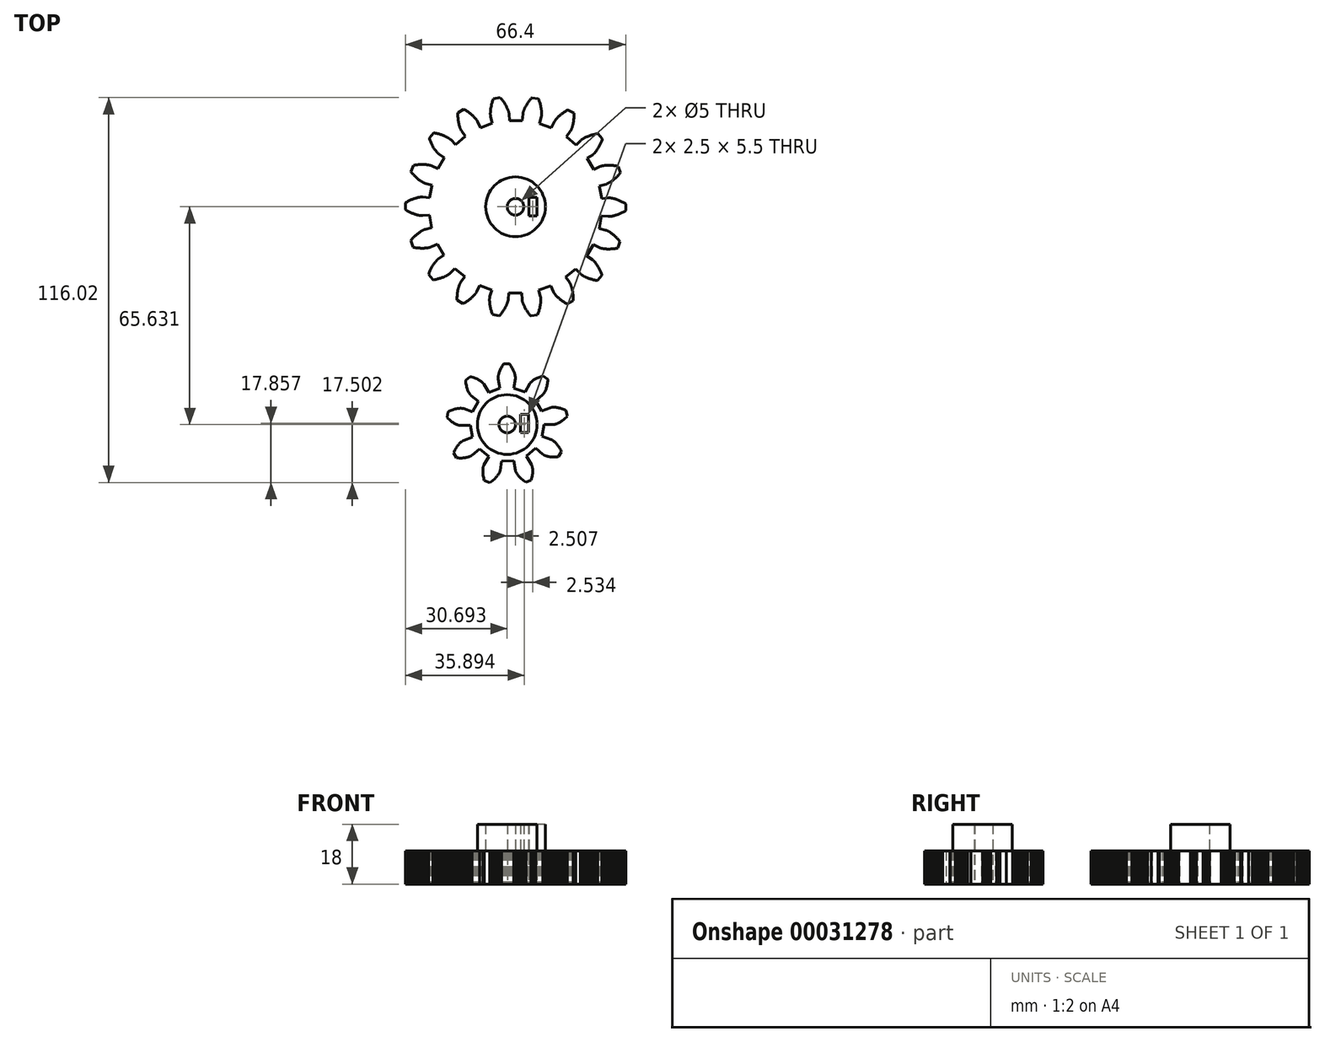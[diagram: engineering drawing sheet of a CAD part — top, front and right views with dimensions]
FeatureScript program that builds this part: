
annotation { "Feature Type Name" : "Feature", "Feature Type Description" : "" }
export const myFeature = defineFeature(function(context is Context, id is Id, definition is map)
    precondition{}
    {
        {
            var Q0;
            Q0=qCreatedBy(makeId("Top.planeOp"),FACE);
            var sketch = newSketch(context, id + "F0", { "sketchPlane" : qUnion([Q0])});
            skLineSegment(sketch, "E0", {"start": v(8.62, -40.5) * mm, "end": v(11.54, -40.5) * mm});
            skLineSegment(sketch, "E1", {"start": v(11.54, -40.5) * mm, "end": v(11.56, -40.5) * mm});
            skLineSegment(sketch, "E2", {"start": v(11.56, -40.5) * mm, "end": v(11.6, -40.5) * mm});
            skLineSegment(sketch, "E3", {"start": v(11.6, -40.5) * mm, "end": v(11.66, -40.5) * mm});
            skLineSegment(sketch, "E4", {"start": v(11.66, -40.5) * mm, "end": v(11.74, -40.48) * mm});
            skLineSegment(sketch, "E5", {"start": v(11.74, -40.48) * mm, "end": v(11.85, -40.46) * mm});
            skLineSegment(sketch, "E6", {"start": v(11.85, -40.46) * mm, "end": v(11.97, -40.43) * mm});
            skLineSegment(sketch, "E7", {"start": v(11.97, -40.43) * mm, "end": v(12.1, -40.4) * mm});
            skLineSegment(sketch, "E8", {"start": v(12.1, -40.4) * mm, "end": v(12.27, -40.34) * mm});
            skLineSegment(sketch, "E9", {"start": v(12.27, -40.34) * mm, "end": v(12.45, -40.28) * mm});
            skLineSegment(sketch, "E10", {"start": v(12.45, -40.28) * mm, "end": v(12.64, -40.2) * mm});
            skLineSegment(sketch, "E11", {"start": v(12.64, -40.2) * mm, "end": v(12.85, -40.1) * mm});
            skLineSegment(sketch, "E12", {"start": v(12.85, -40.1) * mm, "end": v(13.08, -40) * mm});
            skLineSegment(sketch, "E13", {"start": v(13.08, -40) * mm, "end": v(13.32, -39.86) * mm});
            skLineSegment(sketch, "E14", {"start": v(13.32, -39.86) * mm, "end": v(13.57, -39.7) * mm});
            skLineSegment(sketch, "E15", {"start": v(13.57, -39.7) * mm, "end": v(13.83, -39.54) * mm});
            skLineSegment(sketch, "E16", {"start": v(13.83, -39.54) * mm, "end": v(14.1, -39.34) * mm});
            skLineSegment(sketch, "E17", {"start": v(14.1, -39.34) * mm, "end": v(14.4, -39.12) * mm});
            skLineSegment(sketch, "E18", {"start": v(14.4, -39.12) * mm, "end": v(14.68, -38.88) * mm});
            skLineSegment(sketch, "E19", {"start": v(14.68, -38.88) * mm, "end": v(14.98, -38.61) * mm});
            skLineSegment(sketch, "E20", {"start": v(14.98, -38.61) * mm, "end": v(15.28, -38.32) * mm});
            skLineSegment(sketch, "E21", {"start": v(15.28, -38.32) * mm, "end": v(15.58, -38) * mm});
            skLineSegment(sketch, "E22", {"start": v(15.58, -38) * mm, "end": v(15.26, -36.29) * mm});
            skLineSegment(sketch, "E23", {"start": v(15.26, -36.29) * mm, "end": v(14.87, -36.1) * mm});
            skLineSegment(sketch, "E24", {"start": v(14.87, -36.1) * mm, "end": v(14.48, -35.93) * mm});
            skLineSegment(sketch, "E25", {"start": v(14.48, -35.93) * mm, "end": v(14.1, -35.8) * mm});
            skLineSegment(sketch, "E26", {"start": v(14.1, -35.8) * mm, "end": v(13.74, -35.67) * mm});
            skLineSegment(sketch, "E27", {"start": v(13.74, -35.67) * mm, "end": v(13.4, -35.57) * mm});
            skLineSegment(sketch, "E28", {"start": v(13.4, -35.57) * mm, "end": v(13.07, -35.49) * mm});
            skLineSegment(sketch, "E29", {"start": v(13.07, -35.49) * mm, "end": v(12.77, -35.42) * mm});
            skLineSegment(sketch, "E30", {"start": v(12.77, -35.42) * mm, "end": v(12.48, -35.37) * mm});
            skLineSegment(sketch, "E31", {"start": v(12.48, -35.37) * mm, "end": v(12.2, -35.34) * mm});
            skLineSegment(sketch, "E32", {"start": v(12.2, -35.34) * mm, "end": v(11.95, -35.31) * mm});
            skLineSegment(sketch, "E33", {"start": v(11.95, -35.31) * mm, "end": v(11.72, -35.3) * mm});
            skLineSegment(sketch, "E34", {"start": v(11.72, -35.3) * mm, "end": v(11.51, -35.3) * mm});
            skLineSegment(sketch, "E35", {"start": v(11.51, -35.3) * mm, "end": v(11.32, -35.3) * mm});
            skLineSegment(sketch, "E36", {"start": v(11.32, -35.3) * mm, "end": v(11.15, -35.31) * mm});
            skLineSegment(sketch, "E37", {"start": v(11.15, -35.31) * mm, "end": v(11, -35.33) * mm});
            skLineSegment(sketch, "E38", {"start": v(11, -35.33) * mm, "end": v(10.88, -35.34) * mm});
            skLineSegment(sketch, "E39", {"start": v(10.88, -35.34) * mm, "end": v(10.78, -35.36) * mm});
            skLineSegment(sketch, "E40", {"start": v(10.78, -35.36) * mm, "end": v(10.7, -35.38) * mm});
            skLineSegment(sketch, "E41", {"start": v(10.7, -35.38) * mm, "end": v(10.64, -35.4) * mm});
            skLineSegment(sketch, "E42", {"start": v(10.64, -35.4) * mm, "end": v(10.6, -35.4) * mm});
            skLineSegment(sketch, "E43", {"start": v(10.6, -35.4) * mm, "end": v(10.58, -35.41) * mm});
            skLineSegment(sketch, "E44", {"start": v(10.58, -35.41) * mm, "end": v(7.86, -36.47) * mm});
            skLineSegment(sketch, "E45", {"start": v(7.86, -36.47) * mm, "end": v(6.01, -33.36) * mm});
            skLineSegment(sketch, "E46", {"start": v(6.01, -33.36) * mm, "end": v(8.25, -31.48) * mm});
            skLineSegment(sketch, "E47", {"start": v(8.25, -31.48) * mm, "end": v(8.27, -31.47) * mm});
            skLineSegment(sketch, "E48", {"start": v(8.27, -31.47) * mm, "end": v(8.3, -31.44) * mm});
            skLineSegment(sketch, "E49", {"start": v(8.3, -31.44) * mm, "end": v(8.34, -31.4) * mm});
            skLineSegment(sketch, "E50", {"start": v(8.34, -31.4) * mm, "end": v(8.4, -31.33) * mm});
            skLineSegment(sketch, "E51", {"start": v(8.4, -31.33) * mm, "end": v(8.46, -31.25) * mm});
            skLineSegment(sketch, "E52", {"start": v(8.46, -31.25) * mm, "end": v(8.53, -31.15) * mm});
            skLineSegment(sketch, "E53", {"start": v(8.53, -31.15) * mm, "end": v(8.62, -31.03) * mm});
            skLineSegment(sketch, "E54", {"start": v(8.62, -31.03) * mm, "end": v(8.7, -30.88) * mm});
            skLineSegment(sketch, "E55", {"start": v(8.7, -30.88) * mm, "end": v(8.8, -30.72) * mm});
            skLineSegment(sketch, "E56", {"start": v(8.8, -30.72) * mm, "end": v(8.9, -30.54) * mm});
            skLineSegment(sketch, "E57", {"start": v(8.9, -30.54) * mm, "end": v(9, -30.33) * mm});
            skLineSegment(sketch, "E58", {"start": v(9, -30.33) * mm, "end": v(9.1, -30.1) * mm});
            skLineSegment(sketch, "E59", {"start": v(9.1, -30.1) * mm, "end": v(9.2, -29.84) * mm});
            skLineSegment(sketch, "E60", {"start": v(9.2, -29.84) * mm, "end": v(9.3, -29.56) * mm});
            skLineSegment(sketch, "E61", {"start": v(9.3, -29.56) * mm, "end": v(9.39, -29.26) * mm});
            skLineSegment(sketch, "E62", {"start": v(9.39, -29.26) * mm, "end": v(9.47, -28.93) * mm});
            skLineSegment(sketch, "E63", {"start": v(9.47, -28.93) * mm, "end": v(9.55, -28.58) * mm});
            skLineSegment(sketch, "E64", {"start": v(9.55, -28.58) * mm, "end": v(9.61, -28.21) * mm});
            skLineSegment(sketch, "E65", {"start": v(9.61, -28.21) * mm, "end": v(9.67, -27.81) * mm});
            skLineSegment(sketch, "E66", {"start": v(9.67, -27.81) * mm, "end": v(9.71, -27.4) * mm});
            skLineSegment(sketch, "E67", {"start": v(9.71, -27.4) * mm, "end": v(9.74, -26.95) * mm});
            skLineSegment(sketch, "E68", {"start": v(9.74, -26.95) * mm, "end": v(8.4, -25.85) * mm});
            skLineSegment(sketch, "E69", {"start": v(8.4, -25.85) * mm, "end": v(7.97, -25.96) * mm});
            skLineSegment(sketch, "E70", {"start": v(7.97, -25.96) * mm, "end": v(7.56, -26.09) * mm});
            skLineSegment(sketch, "E71", {"start": v(7.56, -26.09) * mm, "end": v(7.19, -26.22) * mm});
            skLineSegment(sketch, "E72", {"start": v(7.19, -26.22) * mm, "end": v(6.83, -26.36) * mm});
            skLineSegment(sketch, "E73", {"start": v(6.83, -26.36) * mm, "end": v(6.5, -26.5) * mm});
            skLineSegment(sketch, "E74", {"start": v(6.5, -26.5) * mm, "end": v(6.2, -26.65) * mm});
            skLineSegment(sketch, "E75", {"start": v(6.2, -26.65) * mm, "end": v(5.92, -26.8) * mm});
            skLineSegment(sketch, "E76", {"start": v(5.92, -26.8) * mm, "end": v(5.67, -26.94) * mm});
            skLineSegment(sketch, "E77", {"start": v(5.67, -26.94) * mm, "end": v(5.44, -27.09) * mm});
            skLineSegment(sketch, "E78", {"start": v(5.44, -27.09) * mm, "end": v(5.23, -27.23) * mm});
            skLineSegment(sketch, "E79", {"start": v(5.23, -27.23) * mm, "end": v(5.04, -27.37) * mm});
            skLineSegment(sketch, "E80", {"start": v(5.04, -27.37) * mm, "end": v(4.88, -27.5) * mm});
            skLineSegment(sketch, "E81", {"start": v(4.88, -27.5) * mm, "end": v(4.74, -27.63) * mm});
            skLineSegment(sketch, "E82", {"start": v(4.74, -27.63) * mm, "end": v(4.62, -27.75) * mm});
            skLineSegment(sketch, "E83", {"start": v(4.62, -27.75) * mm, "end": v(4.52, -27.85) * mm});
            skLineSegment(sketch, "E84", {"start": v(4.52, -27.85) * mm, "end": v(4.43, -27.94) * mm});
            skLineSegment(sketch, "E85", {"start": v(4.43, -27.94) * mm, "end": v(4.37, -28.02) * mm});
            skLineSegment(sketch, "E86", {"start": v(4.37, -28.02) * mm, "end": v(4.31, -28.1) * mm});
            skLineSegment(sketch, "E87", {"start": v(4.31, -28.1) * mm, "end": v(4.28, -28.14) * mm});
            skLineSegment(sketch, "E88", {"start": v(4.28, -28.14) * mm, "end": v(4.26, -28.18) * mm});
            skLineSegment(sketch, "E89", {"start": v(4.26, -28.18) * mm, "end": v(4.25, -28.2) * mm});
            skLineSegment(sketch, "E90", {"start": v(4.25, -28.2) * mm, "end": v(2.84, -30.75) * mm});
            skLineSegment(sketch, "E91", {"start": v(2.84, -30.75) * mm, "end": v(-0.58, -29.55) * mm});
            skLineSegment(sketch, "E92", {"start": v(-0.58, -29.55) * mm, "end": v(-0.07, -26.68) * mm});
            skLineSegment(sketch, "E93", {"start": v(-0.07, -26.68) * mm, "end": v(-0.07, -26.66) * mm});
            skLineSegment(sketch, "E94", {"start": v(-0.07, -26.66) * mm, "end": v(-0.06, -26.62) * mm});
            skLineSegment(sketch, "E95", {"start": v(-0.06, -26.62) * mm, "end": v(-0.06, -26.55) * mm});
            skLineSegment(sketch, "E96", {"start": v(-0.06, -26.55) * mm, "end": v(-0.06, -26.47) * mm});
            skLineSegment(sketch, "E97", {"start": v(-0.06, -26.47) * mm, "end": v(-0.06, -26.37) * mm});
            skLineSegment(sketch, "E98", {"start": v(-0.06, -26.37) * mm, "end": v(-0.07, -26.24) * mm});
            skLineSegment(sketch, "E99", {"start": v(-0.07, -26.24) * mm, "end": v(-0.08, -26.1) * mm});
            skLineSegment(sketch, "E100", {"start": v(-0.08, -26.1) * mm, "end": v(-0.1, -25.93) * mm});
            skLineSegment(sketch, "E101", {"start": v(-0.1, -25.93) * mm, "end": v(-0.13, -25.74) * mm});
            skLineSegment(sketch, "E102", {"start": v(-0.13, -25.74) * mm, "end": v(-0.18, -25.54) * mm});
            skLineSegment(sketch, "E103", {"start": v(-0.18, -25.54) * mm, "end": v(-0.24, -25.31) * mm});
            skLineSegment(sketch, "E104", {"start": v(-0.24, -25.31) * mm, "end": v(-0.3, -25.07) * mm});
            skLineSegment(sketch, "E105", {"start": v(-0.3, -25.07) * mm, "end": v(-0.4, -24.81) * mm});
            skLineSegment(sketch, "E106", {"start": v(-0.4, -24.81) * mm, "end": v(-0.5, -24.54) * mm});
            skLineSegment(sketch, "E107", {"start": v(-0.5, -24.54) * mm, "end": v(-0.63, -24.25) * mm});
            skLineSegment(sketch, "E108", {"start": v(-0.63, -24.25) * mm, "end": v(-0.77, -23.94) * mm});
            skLineSegment(sketch, "E109", {"start": v(-0.77, -23.94) * mm, "end": v(-0.94, -23.62) * mm});
            skLineSegment(sketch, "E110", {"start": v(-0.94, -23.62) * mm, "end": v(-1.13, -23.3) * mm});
            skLineSegment(sketch, "E111", {"start": v(-1.13, -23.3) * mm, "end": v(-1.34, -22.96) * mm});
            skLineSegment(sketch, "E112", {"start": v(-1.34, -22.96) * mm, "end": v(-1.58, -22.6) * mm});
            skLineSegment(sketch, "E113", {"start": v(-1.58, -22.6) * mm, "end": v(-1.84, -22.26) * mm});
            skLineSegment(sketch, "E114", {"start": v(-1.84, -22.26) * mm, "end": v(-3.58, -22.27) * mm});
            skLineSegment(sketch, "E115", {"start": v(-3.58, -22.27) * mm, "end": v(-3.83, -22.63) * mm});
            skLineSegment(sketch, "E116", {"start": v(-3.83, -22.63) * mm, "end": v(-4.06, -22.99) * mm});
            skLineSegment(sketch, "E117", {"start": v(-4.06, -22.99) * mm, "end": v(-4.27, -23.33) * mm});
            skLineSegment(sketch, "E118", {"start": v(-4.27, -23.33) * mm, "end": v(-4.45, -23.66) * mm});
            skLineSegment(sketch, "E119", {"start": v(-4.45, -23.66) * mm, "end": v(-4.6, -23.98) * mm});
            skLineSegment(sketch, "E120", {"start": v(-4.6, -23.98) * mm, "end": v(-4.75, -24.3) * mm});
            skLineSegment(sketch, "E121", {"start": v(-4.75, -24.3) * mm, "end": v(-4.86, -24.58) * mm});
            skLineSegment(sketch, "E122", {"start": v(-4.86, -24.58) * mm, "end": v(-4.96, -24.86) * mm});
            skLineSegment(sketch, "E123", {"start": v(-4.96, -24.86) * mm, "end": v(-5.05, -25.12) * mm});
            skLineSegment(sketch, "E124", {"start": v(-5.05, -25.12) * mm, "end": v(-5.11, -25.37) * mm});
            skLineSegment(sketch, "E125", {"start": v(-5.11, -25.37) * mm, "end": v(-5.17, -25.6) * mm});
            skLineSegment(sketch, "E126", {"start": v(-5.17, -25.6) * mm, "end": v(-5.2, -25.8) * mm});
            skLineSegment(sketch, "E127", {"start": v(-5.2, -25.8) * mm, "end": v(-5.23, -25.98) * mm});
            skLineSegment(sketch, "E128", {"start": v(-5.23, -25.98) * mm, "end": v(-5.25, -26.15) * mm});
            skLineSegment(sketch, "E129", {"start": v(-5.25, -26.15) * mm, "end": v(-5.26, -26.3) * mm});
            skLineSegment(sketch, "E130", {"start": v(-5.26, -26.3) * mm, "end": v(-5.27, -26.42) * mm});
            skLineSegment(sketch, "E131", {"start": v(-5.27, -26.42) * mm, "end": v(-5.27, -26.53) * mm});
            skLineSegment(sketch, "E132", {"start": v(-5.27, -26.53) * mm, "end": v(-5.26, -26.61) * mm});
            skLineSegment(sketch, "E133", {"start": v(-5.26, -26.61) * mm, "end": v(-5.26, -26.67) * mm});
            skLineSegment(sketch, "E134", {"start": v(-5.26, -26.67) * mm, "end": v(-5.25, -26.71) * mm});
            skLineSegment(sketch, "E135", {"start": v(-5.25, -26.71) * mm, "end": v(-5.25, -26.73) * mm});
            skLineSegment(sketch, "E136", {"start": v(-5.25, -26.73) * mm, "end": v(-4.68, -29.6) * mm});
            skLineSegment(sketch, "E137", {"start": v(-4.68, -29.6) * mm, "end": v(-8.07, -30.87) * mm});
            skLineSegment(sketch, "E138", {"start": v(-8.07, -30.87) * mm, "end": v(-9.53, -28.34) * mm});
            skLineSegment(sketch, "E139", {"start": v(-9.53, -28.34) * mm, "end": v(-9.54, -28.33) * mm});
            skLineSegment(sketch, "E140", {"start": v(-9.54, -28.33) * mm, "end": v(-9.56, -28.3) * mm});
            skLineSegment(sketch, "E141", {"start": v(-9.56, -28.3) * mm, "end": v(-9.6, -28.24) * mm});
            skLineSegment(sketch, "E142", {"start": v(-9.6, -28.24) * mm, "end": v(-9.65, -28.18) * mm});
            skLineSegment(sketch, "E143", {"start": v(-9.65, -28.18) * mm, "end": v(-9.72, -28.1) * mm});
            skLineSegment(sketch, "E144", {"start": v(-9.72, -28.1) * mm, "end": v(-9.8, -28) * mm});
            skLineSegment(sketch, "E145", {"start": v(-9.8, -28) * mm, "end": v(-9.91, -27.9) * mm});
            skLineSegment(sketch, "E146", {"start": v(-9.91, -27.9) * mm, "end": v(-10.04, -27.8) * mm});
            skLineSegment(sketch, "E147", {"start": v(-10.04, -27.8) * mm, "end": v(-10.18, -27.67) * mm});
            skLineSegment(sketch, "E148", {"start": v(-10.18, -27.67) * mm, "end": v(-10.35, -27.54) * mm});
            skLineSegment(sketch, "E149", {"start": v(-10.35, -27.54) * mm, "end": v(-10.54, -27.4) * mm});
            skLineSegment(sketch, "E150", {"start": v(-10.54, -27.4) * mm, "end": v(-10.75, -27.27) * mm});
            skLineSegment(sketch, "E151", {"start": v(-10.75, -27.27) * mm, "end": v(-10.98, -27.13) * mm});
            skLineSegment(sketch, "E152", {"start": v(-10.98, -27.13) * mm, "end": v(-11.24, -26.98) * mm});
            skLineSegment(sketch, "E153", {"start": v(-11.24, -26.98) * mm, "end": v(-11.52, -26.84) * mm});
            skLineSegment(sketch, "E154", {"start": v(-11.52, -26.84) * mm, "end": v(-11.83, -26.7) * mm});
            skLineSegment(sketch, "E155", {"start": v(-11.83, -26.7) * mm, "end": v(-12.16, -26.57) * mm});
            skLineSegment(sketch, "E156", {"start": v(-12.16, -26.57) * mm, "end": v(-12.51, -26.43) * mm});
            skLineSegment(sketch, "E157", {"start": v(-12.51, -26.43) * mm, "end": v(-12.9, -26.31) * mm});
            skLineSegment(sketch, "E158", {"start": v(-12.9, -26.31) * mm, "end": v(-13.3, -26.2) * mm});
            skLineSegment(sketch, "E159", {"start": v(-13.3, -26.2) * mm, "end": v(-13.73, -26.1) * mm});
            skLineSegment(sketch, "E160", {"start": v(-13.73, -26.1) * mm, "end": v(-15.05, -27.23) * mm});
            skLineSegment(sketch, "E161", {"start": v(-15.05, -27.23) * mm, "end": v(-15.01, -27.67) * mm});
            skLineSegment(sketch, "E162", {"start": v(-15.01, -27.67) * mm, "end": v(-14.96, -28.09) * mm});
            skLineSegment(sketch, "E163", {"start": v(-14.96, -28.09) * mm, "end": v(-14.9, -28.48) * mm});
            skLineSegment(sketch, "E164", {"start": v(-14.9, -28.48) * mm, "end": v(-14.82, -28.85) * mm});
            skLineSegment(sketch, "E165", {"start": v(-14.82, -28.85) * mm, "end": v(-14.74, -29.2) * mm});
            skLineSegment(sketch, "E166", {"start": v(-14.74, -29.2) * mm, "end": v(-14.65, -29.52) * mm});
            skLineSegment(sketch, "E167", {"start": v(-14.65, -29.52) * mm, "end": v(-14.55, -29.82) * mm});
            skLineSegment(sketch, "E168", {"start": v(-14.55, -29.82) * mm, "end": v(-14.45, -30.1) * mm});
            skLineSegment(sketch, "E169", {"start": v(-14.45, -30.1) * mm, "end": v(-14.34, -30.35) * mm});
            skLineSegment(sketch, "E170", {"start": v(-14.34, -30.35) * mm, "end": v(-14.24, -30.58) * mm});
            skLineSegment(sketch, "E171", {"start": v(-14.24, -30.58) * mm, "end": v(-14.13, -30.79) * mm});
            skLineSegment(sketch, "E172", {"start": v(-14.13, -30.79) * mm, "end": v(-14.03, -30.97) * mm});
            skLineSegment(sketch, "E173", {"start": v(-14.03, -30.97) * mm, "end": v(-13.93, -31.13) * mm});
            skLineSegment(sketch, "E174", {"start": v(-13.93, -31.13) * mm, "end": v(-13.84, -31.27) * mm});
            skLineSegment(sketch, "E175", {"start": v(-13.84, -31.27) * mm, "end": v(-13.75, -31.4) * mm});
            skLineSegment(sketch, "E176", {"start": v(-13.75, -31.4) * mm, "end": v(-13.68, -31.5) * mm});
            skLineSegment(sketch, "E177", {"start": v(-13.68, -31.5) * mm, "end": v(-13.6, -31.57) * mm});
            skLineSegment(sketch, "E178", {"start": v(-13.6, -31.57) * mm, "end": v(-13.55, -31.63) * mm});
            skLineSegment(sketch, "E179", {"start": v(-13.55, -31.63) * mm, "end": v(-13.5, -31.68) * mm});
            skLineSegment(sketch, "E180", {"start": v(-13.5, -31.68) * mm, "end": v(-13.48, -31.7) * mm});
            skLineSegment(sketch, "E181", {"start": v(-13.48, -31.7) * mm, "end": v(-13.46, -31.72) * mm});
            skLineSegment(sketch, "E182", {"start": v(-13.46, -31.72) * mm, "end": v(-11.18, -33.55) * mm});
            skLineSegment(sketch, "E183", {"start": v(-11.18, -33.55) * mm, "end": v(-12.96, -36.7) * mm});
            skLineSegment(sketch, "E184", {"start": v(-12.96, -36.7) * mm, "end": v(-15.7, -35.7) * mm});
            skLineSegment(sketch, "E185", {"start": v(-15.7, -35.7) * mm, "end": v(-15.72, -35.7) * mm});
            skLineSegment(sketch, "E186", {"start": v(-15.72, -35.7) * mm, "end": v(-15.76, -35.69) * mm});
            skLineSegment(sketch, "E187", {"start": v(-15.76, -35.69) * mm, "end": v(-15.82, -35.67) * mm});
            skLineSegment(sketch, "E188", {"start": v(-15.82, -35.67) * mm, "end": v(-15.9, -35.66) * mm});
            skLineSegment(sketch, "E189", {"start": v(-15.9, -35.66) * mm, "end": v(-16, -35.64) * mm});
            skLineSegment(sketch, "E190", {"start": v(-16, -35.64) * mm, "end": v(-16.13, -35.63) * mm});
            skLineSegment(sketch, "E191", {"start": v(-16.13, -35.63) * mm, "end": v(-16.28, -35.61) * mm});
            skLineSegment(sketch, "E192", {"start": v(-16.28, -35.61) * mm, "end": v(-16.45, -35.6) * mm});
            skLineSegment(sketch, "E193", {"start": v(-16.45, -35.6) * mm, "end": v(-16.64, -35.6) * mm});
            skLineSegment(sketch, "E194", {"start": v(-16.64, -35.6) * mm, "end": v(-16.85, -35.61) * mm});
            skLineSegment(sketch, "E195", {"start": v(-16.85, -35.61) * mm, "end": v(-17.08, -35.63) * mm});
            skLineSegment(sketch, "E196", {"start": v(-17.08, -35.63) * mm, "end": v(-17.33, -35.66) * mm});
            skLineSegment(sketch, "E197", {"start": v(-17.33, -35.66) * mm, "end": v(-17.6, -35.7) * mm});
            skLineSegment(sketch, "E198", {"start": v(-17.6, -35.7) * mm, "end": v(-17.89, -35.76) * mm});
            skLineSegment(sketch, "E199", {"start": v(-17.89, -35.76) * mm, "end": v(-18.2, -35.83) * mm});
            skLineSegment(sketch, "E200", {"start": v(-18.2, -35.83) * mm, "end": v(-18.52, -35.92) * mm});
            skLineSegment(sketch, "E201", {"start": v(-18.52, -35.92) * mm, "end": v(-18.86, -36.03) * mm});
            skLineSegment(sketch, "E202", {"start": v(-18.86, -36.03) * mm, "end": v(-19.22, -36.16) * mm});
            skLineSegment(sketch, "E203", {"start": v(-19.22, -36.16) * mm, "end": v(-19.59, -36.3) * mm});
            skLineSegment(sketch, "E204", {"start": v(-19.59, -36.3) * mm, "end": v(-19.97, -36.48) * mm});
            skLineSegment(sketch, "E205", {"start": v(-19.97, -36.48) * mm, "end": v(-20.37, -36.68) * mm});
            skLineSegment(sketch, "E206", {"start": v(-20.37, -36.68) * mm, "end": v(-20.65, -38.4) * mm});
            skLineSegment(sketch, "E207", {"start": v(-20.65, -38.4) * mm, "end": v(-20.34, -38.7) * mm});
            skLineSegment(sketch, "E208", {"start": v(-20.34, -38.7) * mm, "end": v(-20.03, -39) * mm});
            skLineSegment(sketch, "E209", {"start": v(-20.03, -39) * mm, "end": v(-19.73, -39.26) * mm});
            skLineSegment(sketch, "E210", {"start": v(-19.73, -39.26) * mm, "end": v(-19.43, -39.5) * mm});
            skLineSegment(sketch, "E211", {"start": v(-19.43, -39.5) * mm, "end": v(-19.15, -39.7) * mm});
            skLineSegment(sketch, "E212", {"start": v(-19.15, -39.7) * mm, "end": v(-18.87, -39.9) * mm});
            skLineSegment(sketch, "E213", {"start": v(-18.87, -39.9) * mm, "end": v(-18.6, -40.06) * mm});
            skLineSegment(sketch, "E214", {"start": v(-18.6, -40.06) * mm, "end": v(-18.34, -40.21) * mm});
            skLineSegment(sketch, "E215", {"start": v(-18.34, -40.21) * mm, "end": v(-18.1, -40.34) * mm});
            skLineSegment(sketch, "E216", {"start": v(-18.1, -40.34) * mm, "end": v(-17.87, -40.44) * mm});
            skLineSegment(sketch, "E217", {"start": v(-17.87, -40.44) * mm, "end": v(-17.66, -40.54) * mm});
            skLineSegment(sketch, "E218", {"start": v(-17.66, -40.54) * mm, "end": v(-17.46, -40.61) * mm});
            skLineSegment(sketch, "E219", {"start": v(-17.46, -40.61) * mm, "end": v(-17.28, -40.67) * mm});
            skLineSegment(sketch, "E220", {"start": v(-17.28, -40.67) * mm, "end": v(-17.12, -40.72) * mm});
            skLineSegment(sketch, "E221", {"start": v(-17.12, -40.72) * mm, "end": v(-16.98, -40.75) * mm});
            skLineSegment(sketch, "E222", {"start": v(-16.98, -40.75) * mm, "end": v(-16.86, -40.78) * mm});
            skLineSegment(sketch, "E223", {"start": v(-16.86, -40.78) * mm, "end": v(-16.75, -40.8) * mm});
            skLineSegment(sketch, "E224", {"start": v(-16.75, -40.8) * mm, "end": v(-16.67, -40.8) * mm});
            skLineSegment(sketch, "E225", {"start": v(-16.67, -40.8) * mm, "end": v(-16.6, -40.81) * mm});
            skLineSegment(sketch, "E226", {"start": v(-16.6, -40.81) * mm, "end": v(-16.57, -40.82) * mm});
            skLineSegment(sketch, "E227", {"start": v(-16.57, -40.82) * mm, "end": v(-16.55, -40.82) * mm});
            skLineSegment(sketch, "E228", {"start": v(-16.55, -40.82) * mm, "end": v(-13.63, -40.75) * mm});
            skLineSegment(sketch, "E229", {"start": v(-13.63, -40.75) * mm, "end": v(-12.96, -44.31) * mm});
            skLineSegment(sketch, "E230", {"start": v(-12.96, -44.31) * mm, "end": v(-15.7, -45.31) * mm});
            skLineSegment(sketch, "E231", {"start": v(-15.7, -45.31) * mm, "end": v(-15.72, -45.32) * mm});
            skLineSegment(sketch, "E232", {"start": v(-15.72, -45.32) * mm, "end": v(-15.76, -45.34) * mm});
            skLineSegment(sketch, "E233", {"start": v(-15.76, -45.34) * mm, "end": v(-15.82, -45.36) * mm});
            skLineSegment(sketch, "E234", {"start": v(-15.82, -45.36) * mm, "end": v(-15.89, -45.4) * mm});
            skLineSegment(sketch, "E235", {"start": v(-15.89, -45.4) * mm, "end": v(-15.98, -45.46) * mm});
            skLineSegment(sketch, "E236", {"start": v(-15.98, -45.46) * mm, "end": v(-16.08, -45.53) * mm});
            skLineSegment(sketch, "E237", {"start": v(-16.08, -45.53) * mm, "end": v(-16.2, -45.61) * mm});
            skLineSegment(sketch, "E238", {"start": v(-16.2, -45.61) * mm, "end": v(-16.34, -45.71) * mm});
            skLineSegment(sketch, "E239", {"start": v(-16.34, -45.71) * mm, "end": v(-16.48, -45.84) * mm});
            skLineSegment(sketch, "E240", {"start": v(-16.48, -45.84) * mm, "end": v(-16.64, -45.98) * mm});
            skLineSegment(sketch, "E241", {"start": v(-16.64, -45.98) * mm, "end": v(-16.8, -46.14) * mm});
            skLineSegment(sketch, "E242", {"start": v(-16.8, -46.14) * mm, "end": v(-16.98, -46.32) * mm});
            skLineSegment(sketch, "E243", {"start": v(-16.98, -46.32) * mm, "end": v(-17.16, -46.53) * mm});
            skLineSegment(sketch, "E244", {"start": v(-17.16, -46.53) * mm, "end": v(-17.34, -46.76) * mm});
            skLineSegment(sketch, "E245", {"start": v(-17.34, -46.76) * mm, "end": v(-17.53, -47) * mm});
            skLineSegment(sketch, "E246", {"start": v(-17.53, -47) * mm, "end": v(-17.72, -47.29) * mm});
            skLineSegment(sketch, "E247", {"start": v(-17.72, -47.29) * mm, "end": v(-17.91, -47.59) * mm});
            skLineSegment(sketch, "E248", {"start": v(-17.91, -47.59) * mm, "end": v(-18.1, -47.92) * mm});
            skLineSegment(sketch, "E249", {"start": v(-18.1, -47.92) * mm, "end": v(-18.3, -48.27) * mm});
            skLineSegment(sketch, "E250", {"start": v(-18.3, -48.27) * mm, "end": v(-18.47, -48.65) * mm});
            skLineSegment(sketch, "E251", {"start": v(-18.47, -48.65) * mm, "end": v(-18.65, -49.06) * mm});
            skLineSegment(sketch, "E252", {"start": v(-18.65, -49.06) * mm, "end": v(-17.76, -50.55) * mm});
            skLineSegment(sketch, "E253", {"start": v(-17.76, -50.55) * mm, "end": v(-17.32, -50.6) * mm});
            skLineSegment(sketch, "E254", {"start": v(-17.32, -50.6) * mm, "end": v(-16.9, -50.61) * mm});
            skLineSegment(sketch, "E255", {"start": v(-16.9, -50.61) * mm, "end": v(-16.5, -50.62) * mm});
            skLineSegment(sketch, "E256", {"start": v(-16.5, -50.62) * mm, "end": v(-16.12, -50.61) * mm});
            skLineSegment(sketch, "E257", {"start": v(-16.12, -50.61) * mm, "end": v(-15.77, -50.59) * mm});
            skLineSegment(sketch, "E258", {"start": v(-15.77, -50.59) * mm, "end": v(-15.43, -50.56) * mm});
            skLineSegment(sketch, "E259", {"start": v(-15.43, -50.56) * mm, "end": v(-15.12, -50.51) * mm});
            skLineSegment(sketch, "E260", {"start": v(-15.12, -50.51) * mm, "end": v(-14.83, -50.46) * mm});
            skLineSegment(sketch, "E261", {"start": v(-14.83, -50.46) * mm, "end": v(-14.56, -50.4) * mm});
            skLineSegment(sketch, "E262", {"start": v(-14.56, -50.4) * mm, "end": v(-14.32, -50.34) * mm});
            skLineSegment(sketch, "E263", {"start": v(-14.32, -50.34) * mm, "end": v(-14.1, -50.27) * mm});
            skLineSegment(sketch, "E264", {"start": v(-14.1, -50.27) * mm, "end": v(-13.9, -50.2) * mm});
            skLineSegment(sketch, "E265", {"start": v(-13.9, -50.2) * mm, "end": v(-13.72, -50.13) * mm});
            skLineSegment(sketch, "E266", {"start": v(-13.72, -50.13) * mm, "end": v(-13.57, -50.06) * mm});
            skLineSegment(sketch, "E267", {"start": v(-13.57, -50.06) * mm, "end": v(-13.44, -50) * mm});
            skLineSegment(sketch, "E268", {"start": v(-13.44, -50) * mm, "end": v(-13.32, -49.94) * mm});
            skLineSegment(sketch, "E269", {"start": v(-13.32, -49.94) * mm, "end": v(-13.23, -49.89) * mm});
            skLineSegment(sketch, "E270", {"start": v(-13.23, -49.89) * mm, "end": v(-13.16, -49.84) * mm});
            skLineSegment(sketch, "E271", {"start": v(-13.16, -49.84) * mm, "end": v(-13.11, -49.8) * mm});
            skLineSegment(sketch, "E272", {"start": v(-13.11, -49.8) * mm, "end": v(-13.08, -49.78) * mm});
            skLineSegment(sketch, "E273", {"start": v(-13.08, -49.78) * mm, "end": v(-13.06, -49.77) * mm});
            skLineSegment(sketch, "E274", {"start": v(-13.06, -49.77) * mm, "end": v(-10.87, -47.84) * mm});
            skLineSegment(sketch, "E275", {"start": v(-10.87, -47.84) * mm, "end": v(-8.07, -50.14) * mm});
            skLineSegment(sketch, "E276", {"start": v(-8.07, -50.14) * mm, "end": v(-9.53, -52.67) * mm});
            skLineSegment(sketch, "E277", {"start": v(-9.53, -52.67) * mm, "end": v(-9.54, -52.69) * mm});
            skLineSegment(sketch, "E278", {"start": v(-9.54, -52.69) * mm, "end": v(-9.56, -52.73) * mm});
            skLineSegment(sketch, "E279", {"start": v(-9.56, -52.73) * mm, "end": v(-9.58, -52.78) * mm});
            skLineSegment(sketch, "E280", {"start": v(-9.58, -52.78) * mm, "end": v(-9.61, -52.86) * mm});
            skLineSegment(sketch, "E281", {"start": v(-9.61, -52.86) * mm, "end": v(-9.65, -52.96) * mm});
            skLineSegment(sketch, "E282", {"start": v(-9.65, -52.96) * mm, "end": v(-9.68, -53.08) * mm});
            skLineSegment(sketch, "E283", {"start": v(-9.68, -53.08) * mm, "end": v(-9.72, -53.22) * mm});
            skLineSegment(sketch, "E284", {"start": v(-9.72, -53.22) * mm, "end": v(-9.75, -53.39) * mm});
            skLineSegment(sketch, "E285", {"start": v(-9.75, -53.39) * mm, "end": v(-9.79, -53.57) * mm});
            skLineSegment(sketch, "E286", {"start": v(-9.79, -53.57) * mm, "end": v(-9.82, -53.78) * mm});
            skLineSegment(sketch, "E287", {"start": v(-9.82, -53.78) * mm, "end": v(-9.84, -54.01) * mm});
            skLineSegment(sketch, "E288", {"start": v(-9.84, -54.01) * mm, "end": v(-9.85, -54.26) * mm});
            skLineSegment(sketch, "E289", {"start": v(-9.85, -54.26) * mm, "end": v(-9.86, -54.54) * mm});
            skLineSegment(sketch, "E290", {"start": v(-9.86, -54.54) * mm, "end": v(-9.85, -54.83) * mm});
            skLineSegment(sketch, "E291", {"start": v(-9.85, -54.83) * mm, "end": v(-9.84, -55.15) * mm});
            skLineSegment(sketch, "E292", {"start": v(-9.84, -55.15) * mm, "end": v(-9.8, -55.48) * mm});
            skLineSegment(sketch, "E293", {"start": v(-9.8, -55.48) * mm, "end": v(-9.76, -55.84) * mm});
            skLineSegment(sketch, "E294", {"start": v(-9.76, -55.84) * mm, "end": v(-9.7, -56.2) * mm});
            skLineSegment(sketch, "E295", {"start": v(-9.7, -56.2) * mm, "end": v(-9.6, -56.6) * mm});
            skLineSegment(sketch, "E296", {"start": v(-9.6, -56.6) * mm, "end": v(-9.5, -57) * mm});
            skLineSegment(sketch, "E297", {"start": v(-9.5, -57) * mm, "end": v(-9.38, -57.43) * mm});
            skLineSegment(sketch, "E298", {"start": v(-9.38, -57.43) * mm, "end": v(-7.74, -58) * mm});
            skLineSegment(sketch, "E299", {"start": v(-7.74, -58) * mm, "end": v(-7.38, -57.76) * mm});
            skLineSegment(sketch, "E300", {"start": v(-7.38, -57.76) * mm, "end": v(-7.04, -57.5) * mm});
            skLineSegment(sketch, "E301", {"start": v(-7.04, -57.5) * mm, "end": v(-6.73, -57.25) * mm});
            skLineSegment(sketch, "E302", {"start": v(-6.73, -57.25) * mm, "end": v(-6.44, -57) * mm});
            skLineSegment(sketch, "E303", {"start": v(-6.44, -57) * mm, "end": v(-6.18, -56.75) * mm});
            skLineSegment(sketch, "E304", {"start": v(-6.18, -56.75) * mm, "end": v(-5.95, -56.51) * mm});
            skLineSegment(sketch, "E305", {"start": v(-5.95, -56.51) * mm, "end": v(-5.74, -56.28) * mm});
            skLineSegment(sketch, "E306", {"start": v(-5.74, -56.28) * mm, "end": v(-5.55, -56.05) * mm});
            skLineSegment(sketch, "E307", {"start": v(-5.55, -56.05) * mm, "end": v(-5.38, -55.83) * mm});
            skLineSegment(sketch, "E308", {"start": v(-5.38, -55.83) * mm, "end": v(-5.24, -55.63) * mm});
            skLineSegment(sketch, "E309", {"start": v(-5.24, -55.63) * mm, "end": v(-5.11, -55.43) * mm});
            skLineSegment(sketch, "E310", {"start": v(-5.11, -55.43) * mm, "end": v(-5, -55.25) * mm});
            skLineSegment(sketch, "E311", {"start": v(-5, -55.25) * mm, "end": v(-4.91, -55.09) * mm});
            skLineSegment(sketch, "E312", {"start": v(-4.91, -55.09) * mm, "end": v(-4.84, -54.94) * mm});
            skLineSegment(sketch, "E313", {"start": v(-4.84, -54.94) * mm, "end": v(-4.78, -54.8) * mm});
            skLineSegment(sketch, "E314", {"start": v(-4.78, -54.8) * mm, "end": v(-4.73, -54.69) * mm});
            skLineSegment(sketch, "E315", {"start": v(-4.73, -54.69) * mm, "end": v(-4.7, -54.59) * mm});
            skLineSegment(sketch, "E316", {"start": v(-4.7, -54.59) * mm, "end": v(-4.67, -54.5) * mm});
            skLineSegment(sketch, "E317", {"start": v(-4.67, -54.5) * mm, "end": v(-4.65, -54.45) * mm});
            skLineSegment(sketch, "E318", {"start": v(-4.65, -54.45) * mm, "end": v(-4.64, -54.4) * mm});
            skLineSegment(sketch, "E319", {"start": v(-4.64, -54.4) * mm, "end": v(-4.64, -54.39) * mm});
            skLineSegment(sketch, "E320", {"start": v(-4.64, -54.39) * mm, "end": v(-4.2, -51.5) * mm});
            skLineSegment(sketch, "E321", {"start": v(-4.2, -51.5) * mm, "end": v(-0.58, -51.46) * mm});
            skLineSegment(sketch, "E322", {"start": v(-0.58, -51.46) * mm, "end": v(-0.07, -54.34) * mm});
            skLineSegment(sketch, "E323", {"start": v(-0.07, -54.34) * mm, "end": v(-0.06, -54.36) * mm});
            skLineSegment(sketch, "E324", {"start": v(-0.06, -54.36) * mm, "end": v(-0.05, -54.4) * mm});
            skLineSegment(sketch, "E325", {"start": v(-0.05, -54.4) * mm, "end": v(-0.04, -54.46) * mm});
            skLineSegment(sketch, "E326", {"start": v(-0.04, -54.46) * mm, "end": v(0, -54.54) * mm});
            skLineSegment(sketch, "E327", {"start": v(0, -54.54) * mm, "end": v(0.03, -54.63) * mm});
            skLineSegment(sketch, "E328", {"start": v(0.03, -54.63) * mm, "end": v(0.08, -54.75) * mm});
            skLineSegment(sketch, "E329", {"start": v(0.08, -54.75) * mm, "end": v(0.14, -54.88) * mm});
            skLineSegment(sketch, "E330", {"start": v(0.14, -54.88) * mm, "end": v(0.22, -55.03) * mm});
            skLineSegment(sketch, "E331", {"start": v(0.22, -55.03) * mm, "end": v(0.31, -55.2) * mm});
            skLineSegment(sketch, "E332", {"start": v(0.31, -55.2) * mm, "end": v(0.43, -55.37) * mm});
            skLineSegment(sketch, "E333", {"start": v(0.43, -55.37) * mm, "end": v(0.56, -55.56) * mm});
            skLineSegment(sketch, "E334", {"start": v(0.56, -55.56) * mm, "end": v(0.7, -55.77) * mm});
            skLineSegment(sketch, "E335", {"start": v(0.7, -55.77) * mm, "end": v(0.88, -55.98) * mm});
            skLineSegment(sketch, "E336", {"start": v(0.88, -55.98) * mm, "end": v(1.07, -56.2) * mm});
            skLineSegment(sketch, "E337", {"start": v(1.07, -56.2) * mm, "end": v(1.29, -56.43) * mm});
            skLineSegment(sketch, "E338", {"start": v(1.29, -56.43) * mm, "end": v(1.53, -56.67) * mm});
            skLineSegment(sketch, "E339", {"start": v(1.53, -56.67) * mm, "end": v(1.8, -56.9) * mm});
            skLineSegment(sketch, "E340", {"start": v(1.8, -56.9) * mm, "end": v(2.08, -57.15) * mm});
            skLineSegment(sketch, "E341", {"start": v(2.08, -57.15) * mm, "end": v(2.4, -57.4) * mm});
            skLineSegment(sketch, "E342", {"start": v(2.4, -57.4) * mm, "end": v(2.74, -57.65) * mm});
            skLineSegment(sketch, "E343", {"start": v(2.74, -57.65) * mm, "end": v(3.1, -57.89) * mm});
            skLineSegment(sketch, "E344", {"start": v(3.1, -57.89) * mm, "end": v(4.73, -57.28) * mm});
            skLineSegment(sketch, "E345", {"start": v(4.73, -57.28) * mm, "end": v(4.85, -56.85) * mm});
            skLineSegment(sketch, "E346", {"start": v(4.85, -56.85) * mm, "end": v(4.95, -56.44) * mm});
            skLineSegment(sketch, "E347", {"start": v(4.95, -56.44) * mm, "end": v(5.02, -56.05) * mm});
            skLineSegment(sketch, "E348", {"start": v(5.02, -56.05) * mm, "end": v(5.08, -55.67) * mm});
            skLineSegment(sketch, "E349", {"start": v(5.08, -55.67) * mm, "end": v(5.12, -55.32) * mm});
            skLineSegment(sketch, "E350", {"start": v(5.12, -55.32) * mm, "end": v(5.14, -54.98) * mm});
            skLineSegment(sketch, "E351", {"start": v(5.14, -54.98) * mm, "end": v(5.15, -54.67) * mm});
            skLineSegment(sketch, "E352", {"start": v(5.15, -54.67) * mm, "end": v(5.15, -54.37) * mm});
            skLineSegment(sketch, "E353", {"start": v(5.15, -54.37) * mm, "end": v(5.14, -54.1) * mm});
            skLineSegment(sketch, "E354", {"start": v(5.14, -54.1) * mm, "end": v(5.12, -53.85) * mm});
            skLineSegment(sketch, "E355", {"start": v(5.12, -53.85) * mm, "end": v(5.1, -53.62) * mm});
            skLineSegment(sketch, "E356", {"start": v(5.1, -53.62) * mm, "end": v(5.06, -53.4) * mm});
            skLineSegment(sketch, "E357", {"start": v(5.06, -53.4) * mm, "end": v(5.02, -53.22) * mm});
            skLineSegment(sketch, "E358", {"start": v(5.02, -53.22) * mm, "end": v(4.98, -53.06) * mm});
            skLineSegment(sketch, "E359", {"start": v(4.98, -53.06) * mm, "end": v(4.94, -52.92) * mm});
            skLineSegment(sketch, "E360", {"start": v(4.94, -52.92) * mm, "end": v(4.9, -52.8) * mm});
            skLineSegment(sketch, "E361", {"start": v(4.9, -52.8) * mm, "end": v(4.87, -52.7) * mm});
            skLineSegment(sketch, "E362", {"start": v(4.87, -52.7) * mm, "end": v(4.84, -52.62) * mm});
            skLineSegment(sketch, "E363", {"start": v(4.84, -52.62) * mm, "end": v(4.81, -52.57) * mm});
            skLineSegment(sketch, "E364", {"start": v(4.81, -52.57) * mm, "end": v(4.8, -52.53) * mm});
            skLineSegment(sketch, "E365", {"start": v(4.8, -52.53) * mm, "end": v(4.78, -52.51) * mm});
            skLineSegment(sketch, "E366", {"start": v(4.78, -52.51) * mm, "end": v(3.27, -50.02) * mm});
            skLineSegment(sketch, "E367", {"start": v(3.27, -50.02) * mm, "end": v(6.01, -47.66) * mm});
            skLineSegment(sketch, "E368", {"start": v(6.01, -47.66) * mm, "end": v(8.25, -49.54) * mm});
            skLineSegment(sketch, "E369", {"start": v(8.25, -49.54) * mm, "end": v(8.27, -49.55) * mm});
            skLineSegment(sketch, "E370", {"start": v(8.27, -49.55) * mm, "end": v(8.3, -49.57) * mm});
            skLineSegment(sketch, "E371", {"start": v(8.3, -49.57) * mm, "end": v(8.35, -49.6) * mm});
            skLineSegment(sketch, "E372", {"start": v(8.35, -49.6) * mm, "end": v(8.42, -49.65) * mm});
            skLineSegment(sketch, "E373", {"start": v(8.42, -49.65) * mm, "end": v(8.52, -49.7) * mm});
            skLineSegment(sketch, "E374", {"start": v(8.52, -49.7) * mm, "end": v(8.63, -49.76) * mm});
            skLineSegment(sketch, "E375", {"start": v(8.63, -49.76) * mm, "end": v(8.76, -49.82) * mm});
            skLineSegment(sketch, "E376", {"start": v(8.76, -49.82) * mm, "end": v(8.92, -49.88) * mm});
            skLineSegment(sketch, "E377", {"start": v(8.92, -49.88) * mm, "end": v(9.1, -49.95) * mm});
            skLineSegment(sketch, "E378", {"start": v(9.1, -49.95) * mm, "end": v(9.3, -50.01) * mm});
            skLineSegment(sketch, "E379", {"start": v(9.3, -50.01) * mm, "end": v(9.52, -50.07) * mm});
            skLineSegment(sketch, "E380", {"start": v(9.52, -50.07) * mm, "end": v(9.76, -50.13) * mm});
            skLineSegment(sketch, "E381", {"start": v(9.76, -50.13) * mm, "end": v(10.03, -50.18) * mm});
            skLineSegment(sketch, "E382", {"start": v(10.03, -50.18) * mm, "end": v(10.32, -50.23) * mm});
            skLineSegment(sketch, "E383", {"start": v(10.32, -50.23) * mm, "end": v(10.64, -50.27) * mm});
            skLineSegment(sketch, "E384", {"start": v(10.64, -50.27) * mm, "end": v(10.97, -50.3) * mm});
            skLineSegment(sketch, "E385", {"start": v(10.97, -50.3) * mm, "end": v(11.33, -50.3) * mm});
            skLineSegment(sketch, "E386", {"start": v(11.33, -50.3) * mm, "end": v(11.7, -50.3) * mm});
            skLineSegment(sketch, "E387", {"start": v(11.7, -50.3) * mm, "end": v(12.1, -50.3) * mm});
            skLineSegment(sketch, "E388", {"start": v(12.1, -50.3) * mm, "end": v(12.53, -50.26) * mm});
            skLineSegment(sketch, "E389", {"start": v(12.53, -50.26) * mm, "end": v(12.97, -50.21) * mm});
            skLineSegment(sketch, "E390", {"start": v(12.97, -50.21) * mm, "end": v(13.82, -48.7) * mm});
            skLineSegment(sketch, "E391", {"start": v(13.82, -48.7) * mm, "end": v(13.63, -48.3) * mm});
            skLineSegment(sketch, "E392", {"start": v(13.63, -48.3) * mm, "end": v(13.44, -47.92) * mm});
            skLineSegment(sketch, "E393", {"start": v(13.44, -47.92) * mm, "end": v(13.25, -47.57) * mm});
            skLineSegment(sketch, "E394", {"start": v(13.25, -47.57) * mm, "end": v(13.05, -47.25) * mm});
            skLineSegment(sketch, "E395", {"start": v(13.05, -47.25) * mm, "end": v(12.85, -46.95) * mm});
            skLineSegment(sketch, "E396", {"start": v(12.85, -46.95) * mm, "end": v(12.66, -46.68) * mm});
            skLineSegment(sketch, "E397", {"start": v(12.66, -46.68) * mm, "end": v(12.46, -46.43) * mm});
            skLineSegment(sketch, "E398", {"start": v(12.46, -46.43) * mm, "end": v(12.27, -46.2) * mm});
            skLineSegment(sketch, "E399", {"start": v(12.27, -46.2) * mm, "end": v(12.09, -46) * mm});
            skLineSegment(sketch, "E400", {"start": v(12.09, -46) * mm, "end": v(11.9, -45.82) * mm});
            skLineSegment(sketch, "E401", {"start": v(11.9, -45.82) * mm, "end": v(11.74, -45.66) * mm});
            skLineSegment(sketch, "E402", {"start": v(11.74, -45.66) * mm, "end": v(11.58, -45.53) * mm});
            skLineSegment(sketch, "E403", {"start": v(11.58, -45.53) * mm, "end": v(11.43, -45.4) * mm});
            skLineSegment(sketch, "E404", {"start": v(11.43, -45.4) * mm, "end": v(11.3, -45.3) * mm});
            skLineSegment(sketch, "E405", {"start": v(11.3, -45.3) * mm, "end": v(11.18, -45.23) * mm});
            skLineSegment(sketch, "E406", {"start": v(11.18, -45.23) * mm, "end": v(11.07, -45.16) * mm});
            skLineSegment(sketch, "E407", {"start": v(11.07, -45.16) * mm, "end": v(10.98, -45.1) * mm});
            skLineSegment(sketch, "E408", {"start": v(10.98, -45.1) * mm, "end": v(10.9, -45.07) * mm});
            skLineSegment(sketch, "E409", {"start": v(10.9, -45.07) * mm, "end": v(10.85, -45.04) * mm});
            skLineSegment(sketch, "E410", {"start": v(10.85, -45.04) * mm, "end": v(10.81, -45.03) * mm});
            skLineSegment(sketch, "E411", {"start": v(10.81, -45.03) * mm, "end": v(10.8, -45.02) * mm});
            skLineSegment(sketch, "E412", {"start": v(10.8, -45.02) * mm, "end": v(8.03, -44.08) * mm});
            skLineSegment(sketch, "E413", {"start": v(8.03, -44.08) * mm, "end": v(8.62, -40.5) * mm});
            skLineSegment(sketch, "E414", {"start": v(-0.51, -40.5) * mm, "end": v(-4.5, -40.5) * mm});
            skLineSegment(sketch, "E415", {"start": v(-2.5, -42.5) * mm, "end": v(-2.5, -38.52) * mm});
            skLineSegment(sketch, "E416", {"start": v(25.93, 22.4) * mm, "end": v(27.94, 22.19) * mm});
            skLineSegment(sketch, "E417", {"start": v(27.94, 22.19) * mm, "end": v(27.95, 22.19) * mm});
            skLineSegment(sketch, "E418", {"start": v(27.95, 22.19) * mm, "end": v(27.98, 22.18) * mm});
            skLineSegment(sketch, "E419", {"start": v(27.98, 22.18) * mm, "end": v(28.01, 22.18) * mm});
            skLineSegment(sketch, "E420", {"start": v(28.01, 22.18) * mm, "end": v(28.06, 22.18) * mm});
            skLineSegment(sketch, "E421", {"start": v(28.06, 22.18) * mm, "end": v(28.11, 22.18) * mm});
            skLineSegment(sketch, "E422", {"start": v(28.11, 22.18) * mm, "end": v(28.18, 22.18) * mm});
            skLineSegment(sketch, "E423", {"start": v(28.18, 22.18) * mm, "end": v(28.26, 22.19) * mm});
            skLineSegment(sketch, "E424", {"start": v(28.26, 22.19) * mm, "end": v(28.35, 22.2) * mm});
            skLineSegment(sketch, "E425", {"start": v(28.35, 22.2) * mm, "end": v(28.45, 22.2) * mm});
            skLineSegment(sketch, "E426", {"start": v(28.45, 22.2) * mm, "end": v(28.56, 22.21) * mm});
            skLineSegment(sketch, "E427", {"start": v(28.56, 22.21) * mm, "end": v(28.68, 22.22) * mm});
            skLineSegment(sketch, "E428", {"start": v(28.68, 22.22) * mm, "end": v(28.8, 22.24) * mm});
            skLineSegment(sketch, "E429", {"start": v(28.8, 22.24) * mm, "end": v(28.95, 22.26) * mm});
            skLineSegment(sketch, "E430", {"start": v(28.95, 22.26) * mm, "end": v(29.1, 22.3) * mm});
            skLineSegment(sketch, "E431", {"start": v(29.1, 22.3) * mm, "end": v(29.26, 22.32) * mm});
            skLineSegment(sketch, "E432", {"start": v(29.26, 22.32) * mm, "end": v(29.43, 22.36) * mm});
            skLineSegment(sketch, "E433", {"start": v(29.43, 22.36) * mm, "end": v(29.6, 22.4) * mm});
            skLineSegment(sketch, "E434", {"start": v(29.6, 22.4) * mm, "end": v(29.8, 22.45) * mm});
            skLineSegment(sketch, "E435", {"start": v(29.8, 22.45) * mm, "end": v(29.99, 22.5) * mm});
            skLineSegment(sketch, "E436", {"start": v(29.99, 22.5) * mm, "end": v(30.2, 22.57) * mm});
            skLineSegment(sketch, "E437", {"start": v(30.2, 22.57) * mm, "end": v(30.41, 22.64) * mm});
            skLineSegment(sketch, "E438", {"start": v(30.41, 22.64) * mm, "end": v(30.64, 22.71) * mm});
            skLineSegment(sketch, "E439", {"start": v(30.64, 22.71) * mm, "end": v(30.87, 22.8) * mm});
            skLineSegment(sketch, "E440", {"start": v(30.87, 22.8) * mm, "end": v(31.1, 22.89) * mm});
            skLineSegment(sketch, "E441", {"start": v(31.1, 22.89) * mm, "end": v(31.36, 23) * mm});
            skLineSegment(sketch, "E442", {"start": v(31.36, 23) * mm, "end": v(31.61, 23.1) * mm});
            skLineSegment(sketch, "E443", {"start": v(31.61, 23.1) * mm, "end": v(31.88, 23.22) * mm});
            skLineSegment(sketch, "E444", {"start": v(31.88, 23.22) * mm, "end": v(32.15, 23.35) * mm});
            skLineSegment(sketch, "E445", {"start": v(32.15, 23.35) * mm, "end": v(32.42, 23.49) * mm});
            skLineSegment(sketch, "E446", {"start": v(32.42, 23.49) * mm, "end": v(32.7, 23.64) * mm});
            skLineSegment(sketch, "E447", {"start": v(32.7, 23.64) * mm, "end": v(33, 23.8) * mm});
            skLineSegment(sketch, "E448", {"start": v(33, 23.8) * mm, "end": v(33.19, 23.97) * mm});
            skLineSegment(sketch, "E449", {"start": v(33.19, 23.97) * mm, "end": v(33.2, 25.98) * mm});
            skLineSegment(sketch, "E450", {"start": v(33.2, 25.98) * mm, "end": v(33, 26.15) * mm});
            skLineSegment(sketch, "E451", {"start": v(33, 26.15) * mm, "end": v(32.72, 26.32) * mm});
            skLineSegment(sketch, "E452", {"start": v(32.72, 26.32) * mm, "end": v(32.44, 26.47) * mm});
            skLineSegment(sketch, "E453", {"start": v(32.44, 26.47) * mm, "end": v(32.16, 26.61) * mm});
            skLineSegment(sketch, "E454", {"start": v(32.16, 26.61) * mm, "end": v(31.9, 26.74) * mm});
            skLineSegment(sketch, "E455", {"start": v(31.9, 26.74) * mm, "end": v(31.63, 26.86) * mm});
            skLineSegment(sketch, "E456", {"start": v(31.63, 26.86) * mm, "end": v(31.37, 26.98) * mm});
            skLineSegment(sketch, "E457", {"start": v(31.37, 26.98) * mm, "end": v(31.13, 27.08) * mm});
            skLineSegment(sketch, "E458", {"start": v(31.13, 27.08) * mm, "end": v(30.89, 27.18) * mm});
            skLineSegment(sketch, "E459", {"start": v(30.89, 27.18) * mm, "end": v(30.66, 27.26) * mm});
            skLineSegment(sketch, "E460", {"start": v(30.66, 27.26) * mm, "end": v(30.43, 27.34) * mm});
            skLineSegment(sketch, "E461", {"start": v(30.43, 27.34) * mm, "end": v(30.22, 27.41) * mm});
            skLineSegment(sketch, "E462", {"start": v(30.22, 27.41) * mm, "end": v(30.01, 27.48) * mm});
            skLineSegment(sketch, "E463", {"start": v(30.01, 27.48) * mm, "end": v(29.81, 27.53) * mm});
            skLineSegment(sketch, "E464", {"start": v(29.81, 27.53) * mm, "end": v(29.63, 27.58) * mm});
            skLineSegment(sketch, "E465", {"start": v(29.63, 27.58) * mm, "end": v(29.45, 27.63) * mm});
            skLineSegment(sketch, "E466", {"start": v(29.45, 27.63) * mm, "end": v(29.28, 27.66) * mm});
            skLineSegment(sketch, "E467", {"start": v(29.28, 27.66) * mm, "end": v(29.12, 27.7) * mm});
            skLineSegment(sketch, "E468", {"start": v(29.12, 27.7) * mm, "end": v(28.97, 27.73) * mm});
            skLineSegment(sketch, "E469", {"start": v(28.97, 27.73) * mm, "end": v(28.83, 27.75) * mm});
            skLineSegment(sketch, "E470", {"start": v(28.83, 27.75) * mm, "end": v(28.7, 27.77) * mm});
            skLineSegment(sketch, "E471", {"start": v(28.7, 27.77) * mm, "end": v(28.58, 27.78) * mm});
            skLineSegment(sketch, "E472", {"start": v(28.58, 27.78) * mm, "end": v(28.47, 27.8) * mm});
            skLineSegment(sketch, "E473", {"start": v(28.47, 27.8) * mm, "end": v(28.37, 27.8) * mm});
            skLineSegment(sketch, "E474", {"start": v(28.37, 27.8) * mm, "end": v(28.29, 27.8) * mm});
            skLineSegment(sketch, "E475", {"start": v(28.29, 27.8) * mm, "end": v(28.2, 27.81) * mm});
            skLineSegment(sketch, "E476", {"start": v(28.2, 27.81) * mm, "end": v(28.14, 27.81) * mm});
            skLineSegment(sketch, "E477", {"start": v(28.14, 27.81) * mm, "end": v(28.08, 27.81) * mm});
            skLineSegment(sketch, "E478", {"start": v(28.08, 27.81) * mm, "end": v(28.04, 27.81) * mm});
            skLineSegment(sketch, "E479", {"start": v(28.04, 27.81) * mm, "end": v(28, 27.81) * mm});
            skLineSegment(sketch, "E480", {"start": v(28, 27.81) * mm, "end": v(27.98, 27.81) * mm});
            skLineSegment(sketch, "E481", {"start": v(27.98, 27.81) * mm, "end": v(27.96, 27.81) * mm});
            skLineSegment(sketch, "E482", {"start": v(27.96, 27.81) * mm, "end": v(25.95, 27.62) * mm});
            skLineSegment(sketch, "E483", {"start": v(25.95, 27.62) * mm, "end": v(25.3, 31.43) * mm});
            skLineSegment(sketch, "E484", {"start": v(25.3, 31.43) * mm, "end": v(27.25, 31.92) * mm});
            skLineSegment(sketch, "E485", {"start": v(27.25, 31.92) * mm, "end": v(27.27, 31.92) * mm});
            skLineSegment(sketch, "E486", {"start": v(27.27, 31.92) * mm, "end": v(27.3, 31.93) * mm});
            skLineSegment(sketch, "E487", {"start": v(27.3, 31.93) * mm, "end": v(27.33, 31.94) * mm});
            skLineSegment(sketch, "E488", {"start": v(27.33, 31.94) * mm, "end": v(27.37, 31.96) * mm});
            skLineSegment(sketch, "E489", {"start": v(27.37, 31.96) * mm, "end": v(27.43, 31.98) * mm});
            skLineSegment(sketch, "E490", {"start": v(27.43, 31.98) * mm, "end": v(27.49, 32) * mm});
            skLineSegment(sketch, "E491", {"start": v(27.49, 32) * mm, "end": v(27.56, 32.03) * mm});
            skLineSegment(sketch, "E492", {"start": v(27.56, 32.03) * mm, "end": v(27.64, 32.06) * mm});
            skLineSegment(sketch, "E493", {"start": v(27.64, 32.06) * mm, "end": v(27.73, 32.1) * mm});
            skLineSegment(sketch, "E494", {"start": v(27.73, 32.1) * mm, "end": v(27.83, 32.15) * mm});
            skLineSegment(sketch, "E495", {"start": v(27.83, 32.15) * mm, "end": v(27.94, 32.2) * mm});
            skLineSegment(sketch, "E496", {"start": v(27.94, 32.2) * mm, "end": v(28.05, 32.27) * mm});
            skLineSegment(sketch, "E497", {"start": v(28.05, 32.27) * mm, "end": v(28.18, 32.34) * mm});
            skLineSegment(sketch, "E498", {"start": v(28.18, 32.34) * mm, "end": v(28.31, 32.41) * mm});
            skLineSegment(sketch, "E499", {"start": v(28.31, 32.41) * mm, "end": v(28.45, 32.5) * mm});
            skLineSegment(sketch, "E500", {"start": v(28.45, 32.5) * mm, "end": v(28.6, 32.59) * mm});
            skLineSegment(sketch, "E501", {"start": v(28.6, 32.59) * mm, "end": v(28.75, 32.7) * mm});
            skLineSegment(sketch, "E502", {"start": v(28.75, 32.7) * mm, "end": v(28.91, 32.8) * mm});
            skLineSegment(sketch, "E503", {"start": v(28.91, 32.8) * mm, "end": v(29.08, 32.92) * mm});
            skLineSegment(sketch, "E504", {"start": v(29.08, 32.92) * mm, "end": v(29.25, 33.05) * mm});
            skLineSegment(sketch, "E505", {"start": v(29.25, 33.05) * mm, "end": v(29.43, 33.19) * mm});
            skLineSegment(sketch, "E506", {"start": v(29.43, 33.19) * mm, "end": v(29.61, 33.33) * mm});
            skLineSegment(sketch, "E507", {"start": v(29.61, 33.33) * mm, "end": v(29.8, 33.5) * mm});
            skLineSegment(sketch, "E508", {"start": v(29.8, 33.5) * mm, "end": v(30, 33.66) * mm});
            skLineSegment(sketch, "E509", {"start": v(30, 33.66) * mm, "end": v(30.2, 33.84) * mm});
            skLineSegment(sketch, "E510", {"start": v(30.2, 33.84) * mm, "end": v(30.4, 34.03) * mm});
            skLineSegment(sketch, "E511", {"start": v(30.4, 34.03) * mm, "end": v(30.6, 34.24) * mm});
            skLineSegment(sketch, "E512", {"start": v(30.6, 34.24) * mm, "end": v(30.81, 34.45) * mm});
            skLineSegment(sketch, "E513", {"start": v(30.81, 34.45) * mm, "end": v(31.03, 34.68) * mm});
            skLineSegment(sketch, "E514", {"start": v(31.03, 34.68) * mm, "end": v(31.24, 34.92) * mm});
            skLineSegment(sketch, "E515", {"start": v(31.24, 34.92) * mm, "end": v(31.46, 35.17) * mm});
            skLineSegment(sketch, "E516", {"start": v(31.46, 35.17) * mm, "end": v(31.58, 35.4) * mm});
            skLineSegment(sketch, "E517", {"start": v(31.58, 35.4) * mm, "end": v(30.9, 37.28) * mm});
            skLineSegment(sketch, "E518", {"start": v(30.9, 37.28) * mm, "end": v(30.67, 37.38) * mm});
            skLineSegment(sketch, "E519", {"start": v(30.67, 37.38) * mm, "end": v(30.34, 37.44) * mm});
            skLineSegment(sketch, "E520", {"start": v(30.34, 37.44) * mm, "end": v(30.02, 37.48) * mm});
            skLineSegment(sketch, "E521", {"start": v(30.02, 37.48) * mm, "end": v(29.71, 37.52) * mm});
            skLineSegment(sketch, "E522", {"start": v(29.71, 37.52) * mm, "end": v(29.41, 37.55) * mm});
            skLineSegment(sketch, "E523", {"start": v(29.41, 37.55) * mm, "end": v(29.13, 37.58) * mm});
            skLineSegment(sketch, "E524", {"start": v(29.13, 37.58) * mm, "end": v(28.85, 37.6) * mm});
            skLineSegment(sketch, "E525", {"start": v(28.85, 37.6) * mm, "end": v(28.58, 37.6) * mm});
            skLineSegment(sketch, "E526", {"start": v(28.58, 37.6) * mm, "end": v(28.32, 37.62) * mm});
            skLineSegment(sketch, "E527", {"start": v(28.32, 37.62) * mm, "end": v(28.07, 37.62) * mm});
            skLineSegment(sketch, "E528", {"start": v(28.07, 37.62) * mm, "end": v(27.84, 37.62) * mm});
            skLineSegment(sketch, "E529", {"start": v(27.84, 37.62) * mm, "end": v(27.61, 37.6) * mm});
            skLineSegment(sketch, "E530", {"start": v(27.61, 37.6) * mm, "end": v(27.4, 37.6) * mm});
            skLineSegment(sketch, "E531", {"start": v(27.4, 37.6) * mm, "end": v(27.2, 37.58) * mm});
            skLineSegment(sketch, "E532", {"start": v(27.2, 37.58) * mm, "end": v(27, 37.57) * mm});
            skLineSegment(sketch, "E533", {"start": v(27, 37.57) * mm, "end": v(26.82, 37.55) * mm});
            skLineSegment(sketch, "E534", {"start": v(26.82, 37.55) * mm, "end": v(26.64, 37.53) * mm});
            skLineSegment(sketch, "E535", {"start": v(26.64, 37.53) * mm, "end": v(26.48, 37.5) * mm});
            skLineSegment(sketch, "E536", {"start": v(26.48, 37.5) * mm, "end": v(26.33, 37.48) * mm});
            skLineSegment(sketch, "E537", {"start": v(26.33, 37.48) * mm, "end": v(26.2, 37.45) * mm});
            skLineSegment(sketch, "E538", {"start": v(26.2, 37.45) * mm, "end": v(26.07, 37.42) * mm});
            skLineSegment(sketch, "E539", {"start": v(26.07, 37.42) * mm, "end": v(25.95, 37.4) * mm});
            skLineSegment(sketch, "E540", {"start": v(25.95, 37.4) * mm, "end": v(25.84, 37.37) * mm});
            skLineSegment(sketch, "E541", {"start": v(25.84, 37.37) * mm, "end": v(25.75, 37.35) * mm});
            skLineSegment(sketch, "E542", {"start": v(25.75, 37.35) * mm, "end": v(25.66, 37.32) * mm});
            skLineSegment(sketch, "E543", {"start": v(25.66, 37.32) * mm, "end": v(25.59, 37.3) * mm});
            skLineSegment(sketch, "E544", {"start": v(25.59, 37.3) * mm, "end": v(25.52, 37.28) * mm});
            skLineSegment(sketch, "E545", {"start": v(25.52, 37.28) * mm, "end": v(25.47, 37.26) * mm});
            skLineSegment(sketch, "E546", {"start": v(25.47, 37.26) * mm, "end": v(25.43, 37.24) * mm});
            skLineSegment(sketch, "E547", {"start": v(25.43, 37.24) * mm, "end": v(25.4, 37.23) * mm});
            skLineSegment(sketch, "E548", {"start": v(25.4, 37.23) * mm, "end": v(25.37, 37.22) * mm});
            skLineSegment(sketch, "E549", {"start": v(25.37, 37.22) * mm, "end": v(25.35, 37.21) * mm});
            skLineSegment(sketch, "E550", {"start": v(25.35, 37.21) * mm, "end": v(23.53, 36.34) * mm});
            skLineSegment(sketch, "E551", {"start": v(23.53, 36.34) * mm, "end": v(21.61, 39.7) * mm});
            skLineSegment(sketch, "E552", {"start": v(21.61, 39.7) * mm, "end": v(23.29, 40.83) * mm});
            skLineSegment(sketch, "E553", {"start": v(23.29, 40.83) * mm, "end": v(23.3, 40.84) * mm});
            skLineSegment(sketch, "E554", {"start": v(23.3, 40.84) * mm, "end": v(23.32, 40.85) * mm});
            skLineSegment(sketch, "E555", {"start": v(23.32, 40.85) * mm, "end": v(23.35, 40.88) * mm});
            skLineSegment(sketch, "E556", {"start": v(23.35, 40.88) * mm, "end": v(23.38, 40.9) * mm});
            skLineSegment(sketch, "E557", {"start": v(23.38, 40.9) * mm, "end": v(23.43, 40.94) * mm});
            skLineSegment(sketch, "E558", {"start": v(23.43, 40.94) * mm, "end": v(23.48, 40.99) * mm});
            skLineSegment(sketch, "E559", {"start": v(23.48, 40.99) * mm, "end": v(23.54, 41.04) * mm});
            skLineSegment(sketch, "E560", {"start": v(23.54, 41.04) * mm, "end": v(23.6, 41.1) * mm});
            skLineSegment(sketch, "E561", {"start": v(23.6, 41.1) * mm, "end": v(23.67, 41.17) * mm});
            skLineSegment(sketch, "E562", {"start": v(23.67, 41.17) * mm, "end": v(23.75, 41.25) * mm});
            skLineSegment(sketch, "E563", {"start": v(23.75, 41.25) * mm, "end": v(23.83, 41.34) * mm});
            skLineSegment(sketch, "E564", {"start": v(23.83, 41.34) * mm, "end": v(23.92, 41.43) * mm});
            skLineSegment(sketch, "E565", {"start": v(23.92, 41.43) * mm, "end": v(24.01, 41.54) * mm});
            skLineSegment(sketch, "E566", {"start": v(24.01, 41.54) * mm, "end": v(24.11, 41.66) * mm});
            skLineSegment(sketch, "E567", {"start": v(24.11, 41.66) * mm, "end": v(24.21, 41.78) * mm});
            skLineSegment(sketch, "E568", {"start": v(24.21, 41.78) * mm, "end": v(24.32, 41.92) * mm});
            skLineSegment(sketch, "E569", {"start": v(24.32, 41.92) * mm, "end": v(24.43, 42.07) * mm});
            skLineSegment(sketch, "E570", {"start": v(24.43, 42.07) * mm, "end": v(24.54, 42.22) * mm});
            skLineSegment(sketch, "E571", {"start": v(24.54, 42.22) * mm, "end": v(24.66, 42.4) * mm});
            skLineSegment(sketch, "E572", {"start": v(24.66, 42.4) * mm, "end": v(24.78, 42.57) * mm});
            skLineSegment(sketch, "E573", {"start": v(24.78, 42.57) * mm, "end": v(24.9, 42.77) * mm});
            skLineSegment(sketch, "E574", {"start": v(24.9, 42.77) * mm, "end": v(25.02, 42.97) * mm});
            skLineSegment(sketch, "E575", {"start": v(25.02, 42.97) * mm, "end": v(25.14, 43.18) * mm});
            skLineSegment(sketch, "E576", {"start": v(25.14, 43.18) * mm, "end": v(25.27, 43.4) * mm});
            skLineSegment(sketch, "E577", {"start": v(25.27, 43.4) * mm, "end": v(25.4, 43.64) * mm});
            skLineSegment(sketch, "E578", {"start": v(25.4, 43.64) * mm, "end": v(25.52, 43.9) * mm});
            skLineSegment(sketch, "E579", {"start": v(25.52, 43.9) * mm, "end": v(25.64, 44.16) * mm});
            skLineSegment(sketch, "E580", {"start": v(25.64, 44.16) * mm, "end": v(25.77, 44.43) * mm});
            skLineSegment(sketch, "E581", {"start": v(25.77, 44.43) * mm, "end": v(25.89, 44.71) * mm});
            skLineSegment(sketch, "E582", {"start": v(25.89, 44.71) * mm, "end": v(26, 45.01) * mm});
            skLineSegment(sketch, "E583", {"start": v(26, 45.01) * mm, "end": v(26.13, 45.32) * mm});
            skLineSegment(sketch, "E584", {"start": v(26.13, 45.32) * mm, "end": v(26.16, 45.58) * mm});
            skLineSegment(sketch, "E585", {"start": v(26.16, 45.58) * mm, "end": v(24.88, 47.12) * mm});
            skLineSegment(sketch, "E586", {"start": v(24.88, 47.12) * mm, "end": v(24.62, 47.13) * mm});
            skLineSegment(sketch, "E587", {"start": v(24.62, 47.13) * mm, "end": v(24.3, 47.07) * mm});
            skLineSegment(sketch, "E588", {"start": v(24.3, 47.07) * mm, "end": v(23.98, 47) * mm});
            skLineSegment(sketch, "E589", {"start": v(23.98, 47) * mm, "end": v(23.68, 46.94) * mm});
            skLineSegment(sketch, "E590", {"start": v(23.68, 46.94) * mm, "end": v(23.39, 46.86) * mm});
            skLineSegment(sketch, "E591", {"start": v(23.39, 46.86) * mm, "end": v(23.1, 46.79) * mm});
            skLineSegment(sketch, "E592", {"start": v(23.1, 46.79) * mm, "end": v(22.84, 46.71) * mm});
            skLineSegment(sketch, "E593", {"start": v(22.84, 46.71) * mm, "end": v(22.59, 46.63) * mm});
            skLineSegment(sketch, "E594", {"start": v(22.59, 46.63) * mm, "end": v(22.34, 46.55) * mm});
            skLineSegment(sketch, "E595", {"start": v(22.34, 46.55) * mm, "end": v(22.1, 46.47) * mm});
            skLineSegment(sketch, "E596", {"start": v(22.1, 46.47) * mm, "end": v(21.89, 46.38) * mm});
            skLineSegment(sketch, "E597", {"start": v(21.89, 46.38) * mm, "end": v(21.68, 46.3) * mm});
            skLineSegment(sketch, "E598", {"start": v(21.68, 46.3) * mm, "end": v(21.48, 46.22) * mm});
            skLineSegment(sketch, "E599", {"start": v(21.48, 46.22) * mm, "end": v(21.3, 46.13) * mm});
            skLineSegment(sketch, "E600", {"start": v(21.3, 46.13) * mm, "end": v(21.11, 46.05) * mm});
            skLineSegment(sketch, "E601", {"start": v(21.11, 46.05) * mm, "end": v(20.95, 45.97) * mm});
            skLineSegment(sketch, "E602", {"start": v(20.95, 45.97) * mm, "end": v(20.8, 45.9) * mm});
            skLineSegment(sketch, "E603", {"start": v(20.8, 45.9) * mm, "end": v(20.65, 45.81) * mm});
            skLineSegment(sketch, "E604", {"start": v(20.65, 45.81) * mm, "end": v(20.52, 45.74) * mm});
            skLineSegment(sketch, "E605", {"start": v(20.52, 45.74) * mm, "end": v(20.4, 45.67) * mm});
            skLineSegment(sketch, "E606", {"start": v(20.4, 45.67) * mm, "end": v(20.29, 45.6) * mm});
            skLineSegment(sketch, "E607", {"start": v(20.29, 45.6) * mm, "end": v(20.19, 45.53) * mm});
            skLineSegment(sketch, "E608", {"start": v(20.19, 45.53) * mm, "end": v(20.1, 45.47) * mm});
            skLineSegment(sketch, "E609", {"start": v(20.1, 45.47) * mm, "end": v(20.01, 45.41) * mm});
            skLineSegment(sketch, "E610", {"start": v(20.01, 45.41) * mm, "end": v(19.94, 45.36) * mm});
            skLineSegment(sketch, "E611", {"start": v(19.94, 45.36) * mm, "end": v(19.88, 45.31) * mm});
            skLineSegment(sketch, "E612", {"start": v(19.88, 45.31) * mm, "end": v(19.83, 45.27) * mm});
            skLineSegment(sketch, "E613", {"start": v(19.83, 45.27) * mm, "end": v(19.78, 45.24) * mm});
            skLineSegment(sketch, "E614", {"start": v(19.78, 45.24) * mm, "end": v(19.75, 45.2) * mm});
            skLineSegment(sketch, "E615", {"start": v(19.75, 45.2) * mm, "end": v(19.72, 45.18) * mm});
            skLineSegment(sketch, "E616", {"start": v(19.72, 45.18) * mm, "end": v(19.7, 45.17) * mm});
            skLineSegment(sketch, "E617", {"start": v(19.7, 45.17) * mm, "end": v(19.7, 45.15) * mm});
            skLineSegment(sketch, "E618", {"start": v(19.7, 45.15) * mm, "end": v(18.27, 43.71) * mm});
            skLineSegment(sketch, "E619", {"start": v(18.27, 43.71) * mm, "end": v(15.32, 46.21) * mm});
            skLineSegment(sketch, "E620", {"start": v(15.32, 46.21) * mm, "end": v(16.51, 47.85) * mm});
            skLineSegment(sketch, "E621", {"start": v(16.51, 47.85) * mm, "end": v(16.52, 47.86) * mm});
            skLineSegment(sketch, "E622", {"start": v(16.52, 47.86) * mm, "end": v(16.53, 47.88) * mm});
            skLineSegment(sketch, "E623", {"start": v(16.53, 47.88) * mm, "end": v(16.55, 47.91) * mm});
            skLineSegment(sketch, "E624", {"start": v(16.55, 47.91) * mm, "end": v(16.58, 47.95) * mm});
            skLineSegment(sketch, "E625", {"start": v(16.58, 47.95) * mm, "end": v(16.6, 48) * mm});
            skLineSegment(sketch, "E626", {"start": v(16.6, 48) * mm, "end": v(16.64, 48.06) * mm});
            skLineSegment(sketch, "E627", {"start": v(16.64, 48.06) * mm, "end": v(16.67, 48.13) * mm});
            skLineSegment(sketch, "E628", {"start": v(16.67, 48.13) * mm, "end": v(16.71, 48.2) * mm});
            skLineSegment(sketch, "E629", {"start": v(16.71, 48.2) * mm, "end": v(16.76, 48.3) * mm});
            skLineSegment(sketch, "E630", {"start": v(16.76, 48.3) * mm, "end": v(16.8, 48.4) * mm});
            skLineSegment(sketch, "E631", {"start": v(16.8, 48.4) * mm, "end": v(16.85, 48.5) * mm});
            skLineSegment(sketch, "E632", {"start": v(16.85, 48.5) * mm, "end": v(16.9, 48.63) * mm});
            skLineSegment(sketch, "E633", {"start": v(16.9, 48.63) * mm, "end": v(16.95, 48.76) * mm});
            skLineSegment(sketch, "E634", {"start": v(16.95, 48.76) * mm, "end": v(17, 48.9) * mm});
            skLineSegment(sketch, "E635", {"start": v(17, 48.9) * mm, "end": v(17.05, 49.06) * mm});
            skLineSegment(sketch, "E636", {"start": v(17.05, 49.06) * mm, "end": v(17.1, 49.22) * mm});
            skLineSegment(sketch, "E637", {"start": v(17.1, 49.22) * mm, "end": v(17.16, 49.4) * mm});
            skLineSegment(sketch, "E638", {"start": v(17.16, 49.4) * mm, "end": v(17.21, 49.59) * mm});
            skLineSegment(sketch, "E639", {"start": v(17.21, 49.59) * mm, "end": v(17.26, 49.79) * mm});
            skLineSegment(sketch, "E640", {"start": v(17.26, 49.79) * mm, "end": v(17.31, 50) * mm});
            skLineSegment(sketch, "E641", {"start": v(17.31, 50) * mm, "end": v(17.36, 50.22) * mm});
            skLineSegment(sketch, "E642", {"start": v(17.36, 50.22) * mm, "end": v(17.4, 50.45) * mm});
            skLineSegment(sketch, "E643", {"start": v(17.4, 50.45) * mm, "end": v(17.45, 50.7) * mm});
            skLineSegment(sketch, "E644", {"start": v(17.45, 50.7) * mm, "end": v(17.49, 50.95) * mm});
            skLineSegment(sketch, "E645", {"start": v(17.49, 50.95) * mm, "end": v(17.53, 51.21) * mm});
            skLineSegment(sketch, "E646", {"start": v(17.53, 51.21) * mm, "end": v(17.56, 51.49) * mm});
            skLineSegment(sketch, "E647", {"start": v(17.56, 51.49) * mm, "end": v(17.59, 51.78) * mm});
            skLineSegment(sketch, "E648", {"start": v(17.59, 51.78) * mm, "end": v(17.6, 52.08) * mm});
            skLineSegment(sketch, "E649", {"start": v(17.6, 52.08) * mm, "end": v(17.63, 52.39) * mm});
            skLineSegment(sketch, "E650", {"start": v(17.63, 52.39) * mm, "end": v(17.64, 52.7) * mm});
            skLineSegment(sketch, "E651", {"start": v(17.64, 52.7) * mm, "end": v(17.65, 53.04) * mm});
            skLineSegment(sketch, "E652", {"start": v(17.65, 53.04) * mm, "end": v(17.59, 53.3) * mm});
            skLineSegment(sketch, "E653", {"start": v(17.59, 53.3) * mm, "end": v(15.86, 54.3) * mm});
            skLineSegment(sketch, "E654", {"start": v(15.86, 54.3) * mm, "end": v(15.61, 54.22) * mm});
            skLineSegment(sketch, "E655", {"start": v(15.61, 54.22) * mm, "end": v(15.33, 54.06) * mm});
            skLineSegment(sketch, "E656", {"start": v(15.33, 54.06) * mm, "end": v(15.05, 53.89) * mm});
            skLineSegment(sketch, "E657", {"start": v(15.05, 53.89) * mm, "end": v(14.8, 53.72) * mm});
            skLineSegment(sketch, "E658", {"start": v(14.8, 53.72) * mm, "end": v(14.54, 53.55) * mm});
            skLineSegment(sketch, "E659", {"start": v(14.54, 53.55) * mm, "end": v(14.3, 53.39) * mm});
            skLineSegment(sketch, "E660", {"start": v(14.3, 53.39) * mm, "end": v(14.08, 53.22) * mm});
            skLineSegment(sketch, "E661", {"start": v(14.08, 53.22) * mm, "end": v(13.87, 53.06) * mm});
            skLineSegment(sketch, "E662", {"start": v(13.87, 53.06) * mm, "end": v(13.67, 52.9) * mm});
            skLineSegment(sketch, "E663", {"start": v(13.67, 52.9) * mm, "end": v(13.47, 52.74) * mm});
            skLineSegment(sketch, "E664", {"start": v(13.47, 52.74) * mm, "end": v(13.3, 52.59) * mm});
            skLineSegment(sketch, "E665", {"start": v(13.3, 52.59) * mm, "end": v(13.13, 52.44) * mm});
            skLineSegment(sketch, "E666", {"start": v(13.13, 52.44) * mm, "end": v(12.97, 52.3) * mm});
            skLineSegment(sketch, "E667", {"start": v(12.97, 52.3) * mm, "end": v(12.82, 52.15) * mm});
            skLineSegment(sketch, "E668", {"start": v(12.82, 52.15) * mm, "end": v(12.68, 52.01) * mm});
            skLineSegment(sketch, "E669", {"start": v(12.68, 52.01) * mm, "end": v(12.56, 51.88) * mm});
            skLineSegment(sketch, "E670", {"start": v(12.56, 51.88) * mm, "end": v(12.44, 51.75) * mm});
            skLineSegment(sketch, "E671", {"start": v(12.44, 51.75) * mm, "end": v(12.33, 51.63) * mm});
            skLineSegment(sketch, "E672", {"start": v(12.33, 51.63) * mm, "end": v(12.23, 51.51) * mm});
            skLineSegment(sketch, "E673", {"start": v(12.23, 51.51) * mm, "end": v(12.14, 51.4) * mm});
            skLineSegment(sketch, "E674", {"start": v(12.14, 51.4) * mm, "end": v(12.06, 51.3) * mm});
            skLineSegment(sketch, "E675", {"start": v(12.06, 51.3) * mm, "end": v(11.99, 51.2) * mm});
            skLineSegment(sketch, "E676", {"start": v(11.99, 51.2) * mm, "end": v(11.92, 51.12) * mm});
            skLineSegment(sketch, "E677", {"start": v(11.92, 51.12) * mm, "end": v(11.87, 51.04) * mm});
            skLineSegment(sketch, "E678", {"start": v(11.87, 51.04) * mm, "end": v(11.82, 50.96) * mm});
            skLineSegment(sketch, "E679", {"start": v(11.82, 50.96) * mm, "end": v(11.77, 50.9) * mm});
            skLineSegment(sketch, "E680", {"start": v(11.77, 50.9) * mm, "end": v(11.74, 50.84) * mm});
            skLineSegment(sketch, "E681", {"start": v(11.74, 50.84) * mm, "end": v(11.71, 50.79) * mm});
            skLineSegment(sketch, "E682", {"start": v(11.71, 50.79) * mm, "end": v(11.69, 50.75) * mm});
            skLineSegment(sketch, "E683", {"start": v(11.69, 50.75) * mm, "end": v(11.67, 50.72) * mm});
            skLineSegment(sketch, "E684", {"start": v(11.67, 50.72) * mm, "end": v(11.66, 50.7) * mm});
            skLineSegment(sketch, "E685", {"start": v(11.66, 50.7) * mm, "end": v(11.65, 50.68) * mm});
            skLineSegment(sketch, "E686", {"start": v(11.65, 50.68) * mm, "end": v(10.81, 48.84) * mm});
            skLineSegment(sketch, "E687", {"start": v(10.81, 48.84) * mm, "end": v(7.19, 50.18) * mm});
            skLineSegment(sketch, "E688", {"start": v(7.19, 50.18) * mm, "end": v(7.74, 52.12) * mm});
            skLineSegment(sketch, "E689", {"start": v(7.74, 52.12) * mm, "end": v(7.75, 52.14) * mm});
            skLineSegment(sketch, "E690", {"start": v(7.75, 52.14) * mm, "end": v(7.75, 52.16) * mm});
            skLineSegment(sketch, "E691", {"start": v(7.75, 52.16) * mm, "end": v(7.76, 52.2) * mm});
            skLineSegment(sketch, "E692", {"start": v(7.76, 52.2) * mm, "end": v(7.77, 52.24) * mm});
            skLineSegment(sketch, "E693", {"start": v(7.77, 52.24) * mm, "end": v(7.78, 52.3) * mm});
            skLineSegment(sketch, "E694", {"start": v(7.78, 52.3) * mm, "end": v(7.79, 52.37) * mm});
            skLineSegment(sketch, "E695", {"start": v(7.79, 52.37) * mm, "end": v(7.8, 52.44) * mm});
            skLineSegment(sketch, "E696", {"start": v(7.8, 52.44) * mm, "end": v(7.8, 52.53) * mm});
            skLineSegment(sketch, "E697", {"start": v(7.8, 52.53) * mm, "end": v(7.82, 52.63) * mm});
            skLineSegment(sketch, "E698", {"start": v(7.82, 52.63) * mm, "end": v(7.83, 52.74) * mm});
            skLineSegment(sketch, "E699", {"start": v(7.83, 52.74) * mm, "end": v(7.83, 52.86) * mm});
            skLineSegment(sketch, "E700", {"start": v(7.83, 52.86) * mm, "end": v(7.84, 53) * mm});
            skLineSegment(sketch, "E701", {"start": v(7.84, 53) * mm, "end": v(7.84, 53.13) * mm});
            skLineSegment(sketch, "E702", {"start": v(7.84, 53.13) * mm, "end": v(7.84, 53.29) * mm});
            skLineSegment(sketch, "E703", {"start": v(7.84, 53.29) * mm, "end": v(7.84, 53.45) * mm});
            skLineSegment(sketch, "E704", {"start": v(7.84, 53.45) * mm, "end": v(7.83, 53.62) * mm});
            skLineSegment(sketch, "E705", {"start": v(7.83, 53.62) * mm, "end": v(7.82, 53.8) * mm});
            skLineSegment(sketch, "E706", {"start": v(7.82, 53.8) * mm, "end": v(7.8, 54) * mm});
            skLineSegment(sketch, "E707", {"start": v(7.8, 54) * mm, "end": v(7.79, 54.2) * mm});
            skLineSegment(sketch, "E708", {"start": v(7.79, 54.2) * mm, "end": v(7.76, 54.42) * mm});
            skLineSegment(sketch, "E709", {"start": v(7.76, 54.42) * mm, "end": v(7.73, 54.64) * mm});
            skLineSegment(sketch, "E710", {"start": v(7.73, 54.64) * mm, "end": v(7.7, 54.87) * mm});
            skLineSegment(sketch, "E711", {"start": v(7.7, 54.87) * mm, "end": v(7.65, 55.12) * mm});
            skLineSegment(sketch, "E712", {"start": v(7.65, 55.12) * mm, "end": v(7.6, 55.37) * mm});
            skLineSegment(sketch, "E713", {"start": v(7.6, 55.37) * mm, "end": v(7.55, 55.63) * mm});
            skLineSegment(sketch, "E714", {"start": v(7.55, 55.63) * mm, "end": v(7.48, 55.9) * mm});
            skLineSegment(sketch, "E715", {"start": v(7.48, 55.9) * mm, "end": v(7.4, 56.18) * mm});
            skLineSegment(sketch, "E716", {"start": v(7.4, 56.18) * mm, "end": v(7.33, 56.47) * mm});
            skLineSegment(sketch, "E717", {"start": v(7.33, 56.47) * mm, "end": v(7.24, 56.77) * mm});
            skLineSegment(sketch, "E718", {"start": v(7.24, 56.77) * mm, "end": v(7.14, 57.08) * mm});
            skLineSegment(sketch, "E719", {"start": v(7.14, 57.08) * mm, "end": v(7.03, 57.4) * mm});
            skLineSegment(sketch, "E720", {"start": v(7.03, 57.4) * mm, "end": v(6.9, 57.6) * mm});
            skLineSegment(sketch, "E721", {"start": v(6.9, 57.6) * mm, "end": v(4.92, 57.96) * mm});
            skLineSegment(sketch, "E722", {"start": v(4.92, 57.96) * mm, "end": v(4.72, 57.8) * mm});
            skLineSegment(sketch, "E723", {"start": v(4.72, 57.8) * mm, "end": v(4.5, 57.55) * mm});
            skLineSegment(sketch, "E724", {"start": v(4.5, 57.55) * mm, "end": v(4.3, 57.3) * mm});
            skLineSegment(sketch, "E725", {"start": v(4.3, 57.3) * mm, "end": v(4.12, 57.05) * mm});
            skLineSegment(sketch, "E726", {"start": v(4.12, 57.05) * mm, "end": v(3.94, 56.81) * mm});
            skLineSegment(sketch, "E727", {"start": v(3.94, 56.81) * mm, "end": v(3.78, 56.57) * mm});
            skLineSegment(sketch, "E728", {"start": v(3.78, 56.57) * mm, "end": v(3.62, 56.34) * mm});
            skLineSegment(sketch, "E729", {"start": v(3.62, 56.34) * mm, "end": v(3.48, 56.12) * mm});
            skLineSegment(sketch, "E730", {"start": v(3.48, 56.12) * mm, "end": v(3.34, 55.9) * mm});
            skLineSegment(sketch, "E731", {"start": v(3.34, 55.9) * mm, "end": v(3.22, 55.68) * mm});
            skLineSegment(sketch, "E732", {"start": v(3.22, 55.68) * mm, "end": v(3.1, 55.48) * mm});
            skLineSegment(sketch, "E733", {"start": v(3.1, 55.48) * mm, "end": v(3, 55.28) * mm});
            skLineSegment(sketch, "E734", {"start": v(3, 55.28) * mm, "end": v(2.9, 55.09) * mm});
            skLineSegment(sketch, "E735", {"start": v(2.9, 55.09) * mm, "end": v(2.8, 54.9) * mm});
            skLineSegment(sketch, "E736", {"start": v(2.8, 54.9) * mm, "end": v(2.72, 54.73) * mm});
            skLineSegment(sketch, "E737", {"start": v(2.72, 54.73) * mm, "end": v(2.65, 54.56) * mm});
            skLineSegment(sketch, "E738", {"start": v(2.65, 54.56) * mm, "end": v(2.58, 54.4) * mm});
            skLineSegment(sketch, "E739", {"start": v(2.58, 54.4) * mm, "end": v(2.52, 54.25) * mm});
            skLineSegment(sketch, "E740", {"start": v(2.52, 54.25) * mm, "end": v(2.47, 54.1) * mm});
            skLineSegment(sketch, "E741", {"start": v(2.47, 54.1) * mm, "end": v(2.42, 53.97) * mm});
            skLineSegment(sketch, "E742", {"start": v(2.42, 53.97) * mm, "end": v(2.38, 53.85) * mm});
            skLineSegment(sketch, "E743", {"start": v(2.38, 53.85) * mm, "end": v(2.34, 53.73) * mm});
            skLineSegment(sketch, "E744", {"start": v(2.34, 53.73) * mm, "end": v(2.31, 53.63) * mm});
            skLineSegment(sketch, "E745", {"start": v(2.31, 53.63) * mm, "end": v(2.29, 53.53) * mm});
            skLineSegment(sketch, "E746", {"start": v(2.29, 53.53) * mm, "end": v(2.27, 53.45) * mm});
            skLineSegment(sketch, "E747", {"start": v(2.27, 53.45) * mm, "end": v(2.25, 53.37) * mm});
            skLineSegment(sketch, "E748", {"start": v(2.25, 53.37) * mm, "end": v(2.24, 53.3) * mm});
            skLineSegment(sketch, "E749", {"start": v(2.24, 53.3) * mm, "end": v(2.23, 53.25) * mm});
            skLineSegment(sketch, "E750", {"start": v(2.23, 53.25) * mm, "end": v(2.22, 53.2) * mm});
            skLineSegment(sketch, "E751", {"start": v(2.22, 53.2) * mm, "end": v(2.21, 53.17) * mm});
            skLineSegment(sketch, "E752", {"start": v(2.21, 53.17) * mm, "end": v(2.2, 53.14) * mm});
            skLineSegment(sketch, "E753", {"start": v(2.2, 53.14) * mm, "end": v(2.2, 53.13) * mm});
            skLineSegment(sketch, "E754", {"start": v(2.2, 53.13) * mm, "end": v(2.05, 51.11) * mm});
            skLineSegment(sketch, "E755", {"start": v(2.05, 51.11) * mm, "end": v(-1.82, 51.13) * mm});
            skLineSegment(sketch, "E756", {"start": v(-1.82, 51.13) * mm, "end": v(-1.96, 53.14) * mm});
            skLineSegment(sketch, "E757", {"start": v(-1.96, 53.14) * mm, "end": v(-1.96, 53.16) * mm});
            skLineSegment(sketch, "E758", {"start": v(-1.96, 53.16) * mm, "end": v(-1.96, 53.18) * mm});
            skLineSegment(sketch, "E759", {"start": v(-1.96, 53.18) * mm, "end": v(-1.97, 53.22) * mm});
            skLineSegment(sketch, "E760", {"start": v(-1.97, 53.22) * mm, "end": v(-1.98, 53.27) * mm});
            skLineSegment(sketch, "E761", {"start": v(-1.98, 53.27) * mm, "end": v(-1.99, 53.32) * mm});
            skLineSegment(sketch, "E762", {"start": v(-1.99, 53.32) * mm, "end": v(-2, 53.39) * mm});
            skLineSegment(sketch, "E763", {"start": v(-2, 53.39) * mm, "end": v(-2.02, 53.46) * mm});
            skLineSegment(sketch, "E764", {"start": v(-2.02, 53.46) * mm, "end": v(-2.04, 53.55) * mm});
            skLineSegment(sketch, "E765", {"start": v(-2.04, 53.55) * mm, "end": v(-2.06, 53.65) * mm});
            skLineSegment(sketch, "E766", {"start": v(-2.06, 53.65) * mm, "end": v(-2.1, 53.75) * mm});
            skLineSegment(sketch, "E767", {"start": v(-2.1, 53.75) * mm, "end": v(-2.12, 53.87) * mm});
            skLineSegment(sketch, "E768", {"start": v(-2.12, 53.87) * mm, "end": v(-2.16, 54) * mm});
            skLineSegment(sketch, "E769", {"start": v(-2.16, 54) * mm, "end": v(-2.21, 54.13) * mm});
            skLineSegment(sketch, "E770", {"start": v(-2.21, 54.13) * mm, "end": v(-2.26, 54.27) * mm});
            skLineSegment(sketch, "E771", {"start": v(-2.26, 54.27) * mm, "end": v(-2.32, 54.42) * mm});
            skLineSegment(sketch, "E772", {"start": v(-2.32, 54.42) * mm, "end": v(-2.39, 54.58) * mm});
            skLineSegment(sketch, "E773", {"start": v(-2.39, 54.58) * mm, "end": v(-2.46, 54.75) * mm});
            skLineSegment(sketch, "E774", {"start": v(-2.46, 54.75) * mm, "end": v(-2.54, 54.93) * mm});
            skLineSegment(sketch, "E775", {"start": v(-2.54, 54.93) * mm, "end": v(-2.63, 55.11) * mm});
            skLineSegment(sketch, "E776", {"start": v(-2.63, 55.11) * mm, "end": v(-2.73, 55.3) * mm});
            skLineSegment(sketch, "E777", {"start": v(-2.73, 55.3) * mm, "end": v(-2.83, 55.5) * mm});
            skLineSegment(sketch, "E778", {"start": v(-2.83, 55.5) * mm, "end": v(-2.94, 55.71) * mm});
            skLineSegment(sketch, "E779", {"start": v(-2.94, 55.71) * mm, "end": v(-3.07, 55.93) * mm});
            skLineSegment(sketch, "E780", {"start": v(-3.07, 55.93) * mm, "end": v(-3.2, 56.15) * mm});
            skLineSegment(sketch, "E781", {"start": v(-3.2, 56.15) * mm, "end": v(-3.34, 56.37) * mm});
            skLineSegment(sketch, "E782", {"start": v(-3.34, 56.37) * mm, "end": v(-3.5, 56.6) * mm});
            skLineSegment(sketch, "E783", {"start": v(-3.5, 56.6) * mm, "end": v(-3.66, 56.84) * mm});
            skLineSegment(sketch, "E784", {"start": v(-3.66, 56.84) * mm, "end": v(-3.84, 57.09) * mm});
            skLineSegment(sketch, "E785", {"start": v(-3.84, 57.09) * mm, "end": v(-4.02, 57.34) * mm});
            skLineSegment(sketch, "E786", {"start": v(-4.02, 57.34) * mm, "end": v(-4.22, 57.6) * mm});
            skLineSegment(sketch, "E787", {"start": v(-4.22, 57.6) * mm, "end": v(-4.43, 57.85) * mm});
            skLineSegment(sketch, "E788", {"start": v(-4.43, 57.85) * mm, "end": v(-4.63, 58) * mm});
            skLineSegment(sketch, "E789", {"start": v(-4.63, 58) * mm, "end": v(-6.6, 57.67) * mm});
            skLineSegment(sketch, "E790", {"start": v(-6.6, 57.67) * mm, "end": v(-6.75, 57.45) * mm});
            skLineSegment(sketch, "E791", {"start": v(-6.75, 57.45) * mm, "end": v(-6.86, 57.14) * mm});
            skLineSegment(sketch, "E792", {"start": v(-6.86, 57.14) * mm, "end": v(-6.96, 56.83) * mm});
            skLineSegment(sketch, "E793", {"start": v(-6.96, 56.83) * mm, "end": v(-7.05, 56.54) * mm});
            skLineSegment(sketch, "E794", {"start": v(-7.05, 56.54) * mm, "end": v(-7.13, 56.25) * mm});
            skLineSegment(sketch, "E795", {"start": v(-7.13, 56.25) * mm, "end": v(-7.2, 55.97) * mm});
            skLineSegment(sketch, "E796", {"start": v(-7.2, 55.97) * mm, "end": v(-7.27, 55.7) * mm});
            skLineSegment(sketch, "E797", {"start": v(-7.27, 55.7) * mm, "end": v(-7.33, 55.44) * mm});
            skLineSegment(sketch, "E798", {"start": v(-7.33, 55.44) * mm, "end": v(-7.39, 55.18) * mm});
            skLineSegment(sketch, "E799", {"start": v(-7.39, 55.18) * mm, "end": v(-7.43, 54.94) * mm});
            skLineSegment(sketch, "E800", {"start": v(-7.43, 54.94) * mm, "end": v(-7.47, 54.7) * mm});
            skLineSegment(sketch, "E801", {"start": v(-7.47, 54.7) * mm, "end": v(-7.5, 54.48) * mm});
            skLineSegment(sketch, "E802", {"start": v(-7.5, 54.48) * mm, "end": v(-7.53, 54.27) * mm});
            skLineSegment(sketch, "E803", {"start": v(-7.53, 54.27) * mm, "end": v(-7.55, 54.07) * mm});
            skLineSegment(sketch, "E804", {"start": v(-7.55, 54.07) * mm, "end": v(-7.57, 53.87) * mm});
            skLineSegment(sketch, "E805", {"start": v(-7.57, 53.87) * mm, "end": v(-7.58, 53.69) * mm});
            skLineSegment(sketch, "E806", {"start": v(-7.58, 53.69) * mm, "end": v(-7.59, 53.52) * mm});
            skLineSegment(sketch, "E807", {"start": v(-7.59, 53.52) * mm, "end": v(-7.6, 53.35) * mm});
            skLineSegment(sketch, "E808", {"start": v(-7.6, 53.35) * mm, "end": v(-7.6, 53.2) * mm});
            skLineSegment(sketch, "E809", {"start": v(-7.6, 53.2) * mm, "end": v(-7.6, 53.06) * mm});
            skLineSegment(sketch, "E810", {"start": v(-7.6, 53.06) * mm, "end": v(-7.59, 52.93) * mm});
            skLineSegment(sketch, "E811", {"start": v(-7.59, 52.93) * mm, "end": v(-7.58, 52.8) * mm});
            skLineSegment(sketch, "E812", {"start": v(-7.58, 52.8) * mm, "end": v(-7.57, 52.7) * mm});
            skLineSegment(sketch, "E813", {"start": v(-7.57, 52.7) * mm, "end": v(-7.57, 52.6) * mm});
            skLineSegment(sketch, "E814", {"start": v(-7.57, 52.6) * mm, "end": v(-7.56, 52.51) * mm});
            skLineSegment(sketch, "E815", {"start": v(-7.56, 52.51) * mm, "end": v(-7.55, 52.44) * mm});
            skLineSegment(sketch, "E816", {"start": v(-7.55, 52.44) * mm, "end": v(-7.54, 52.37) * mm});
            skLineSegment(sketch, "E817", {"start": v(-7.54, 52.37) * mm, "end": v(-7.53, 52.31) * mm});
            skLineSegment(sketch, "E818", {"start": v(-7.53, 52.31) * mm, "end": v(-7.52, 52.27) * mm});
            skLineSegment(sketch, "E819", {"start": v(-7.52, 52.27) * mm, "end": v(-7.51, 52.23) * mm});
            skLineSegment(sketch, "E820", {"start": v(-7.51, 52.23) * mm, "end": v(-7.5, 52.2) * mm});
            skLineSegment(sketch, "E821", {"start": v(-7.5, 52.2) * mm, "end": v(-7.5, 52.2) * mm});
            skLineSegment(sketch, "E822", {"start": v(-7.5, 52.2) * mm, "end": v(-6.96, 50.24) * mm});
            skLineSegment(sketch, "E823", {"start": v(-6.96, 50.24) * mm, "end": v(-10.6, 48.94) * mm});
            skLineSegment(sketch, "E824", {"start": v(-10.6, 48.94) * mm, "end": v(-11.43, 50.78) * mm});
            skLineSegment(sketch, "E825", {"start": v(-11.43, 50.78) * mm, "end": v(-11.43, 50.8) * mm});
            skLineSegment(sketch, "E826", {"start": v(-11.43, 50.8) * mm, "end": v(-11.44, 50.82) * mm});
            skLineSegment(sketch, "E827", {"start": v(-11.44, 50.82) * mm, "end": v(-11.46, 50.85) * mm});
            skLineSegment(sketch, "E828", {"start": v(-11.46, 50.85) * mm, "end": v(-11.48, 50.9) * mm});
            skLineSegment(sketch, "E829", {"start": v(-11.48, 50.9) * mm, "end": v(-11.51, 50.94) * mm});
            skLineSegment(sketch, "E830", {"start": v(-11.51, 50.94) * mm, "end": v(-11.55, 51) * mm});
            skLineSegment(sketch, "E831", {"start": v(-11.55, 51) * mm, "end": v(-11.59, 51.07) * mm});
            skLineSegment(sketch, "E832", {"start": v(-11.59, 51.07) * mm, "end": v(-11.64, 51.14) * mm});
            skLineSegment(sketch, "E833", {"start": v(-11.64, 51.14) * mm, "end": v(-11.7, 51.22) * mm});
            skLineSegment(sketch, "E834", {"start": v(-11.7, 51.22) * mm, "end": v(-11.76, 51.31) * mm});
            skLineSegment(sketch, "E835", {"start": v(-11.76, 51.31) * mm, "end": v(-11.83, 51.4) * mm});
            skLineSegment(sketch, "E836", {"start": v(-11.83, 51.4) * mm, "end": v(-11.9, 51.51) * mm});
            skLineSegment(sketch, "E837", {"start": v(-11.9, 51.51) * mm, "end": v(-12, 51.62) * mm});
            skLineSegment(sketch, "E838", {"start": v(-12, 51.62) * mm, "end": v(-12.1, 51.74) * mm});
            skLineSegment(sketch, "E839", {"start": v(-12.1, 51.74) * mm, "end": v(-12.2, 51.86) * mm});
            skLineSegment(sketch, "E840", {"start": v(-12.2, 51.86) * mm, "end": v(-12.32, 51.99) * mm});
            skLineSegment(sketch, "E841", {"start": v(-12.32, 51.99) * mm, "end": v(-12.44, 52.12) * mm});
            skLineSegment(sketch, "E842", {"start": v(-12.44, 52.12) * mm, "end": v(-12.58, 52.26) * mm});
            skLineSegment(sketch, "E843", {"start": v(-12.58, 52.26) * mm, "end": v(-12.73, 52.4) * mm});
            skLineSegment(sketch, "E844", {"start": v(-12.73, 52.4) * mm, "end": v(-12.88, 52.55) * mm});
            skLineSegment(sketch, "E845", {"start": v(-12.88, 52.55) * mm, "end": v(-13.05, 52.7) * mm});
            skLineSegment(sketch, "E846", {"start": v(-13.05, 52.7) * mm, "end": v(-13.23, 52.86) * mm});
            skLineSegment(sketch, "E847", {"start": v(-13.23, 52.86) * mm, "end": v(-13.42, 53.02) * mm});
            skLineSegment(sketch, "E848", {"start": v(-13.42, 53.02) * mm, "end": v(-13.62, 53.18) * mm});
            skLineSegment(sketch, "E849", {"start": v(-13.62, 53.18) * mm, "end": v(-13.83, 53.34) * mm});
            skLineSegment(sketch, "E850", {"start": v(-13.83, 53.34) * mm, "end": v(-14.05, 53.51) * mm});
            skLineSegment(sketch, "E851", {"start": v(-14.05, 53.51) * mm, "end": v(-14.3, 53.68) * mm});
            skLineSegment(sketch, "E852", {"start": v(-14.3, 53.68) * mm, "end": v(-14.54, 53.85) * mm});
            skLineSegment(sketch, "E853", {"start": v(-14.54, 53.85) * mm, "end": v(-14.8, 54.02) * mm});
            skLineSegment(sketch, "E854", {"start": v(-14.8, 54.02) * mm, "end": v(-15.07, 54.2) * mm});
            skLineSegment(sketch, "E855", {"start": v(-15.07, 54.2) * mm, "end": v(-15.35, 54.36) * mm});
            skLineSegment(sketch, "E856", {"start": v(-15.35, 54.36) * mm, "end": v(-15.6, 54.44) * mm});
            skLineSegment(sketch, "E857", {"start": v(-15.6, 54.44) * mm, "end": v(-17.34, 53.45) * mm});
            skLineSegment(sketch, "E858", {"start": v(-17.34, 53.45) * mm, "end": v(-17.4, 53.2) * mm});
            skLineSegment(sketch, "E859", {"start": v(-17.4, 53.2) * mm, "end": v(-17.4, 52.86) * mm});
            skLineSegment(sketch, "E860", {"start": v(-17.4, 52.86) * mm, "end": v(-17.38, 52.54) * mm});
            skLineSegment(sketch, "E861", {"start": v(-17.38, 52.54) * mm, "end": v(-17.37, 52.23) * mm});
            skLineSegment(sketch, "E862", {"start": v(-17.37, 52.23) * mm, "end": v(-17.35, 51.93) * mm});
            skLineSegment(sketch, "E863", {"start": v(-17.35, 51.93) * mm, "end": v(-17.32, 51.64) * mm});
            skLineSegment(sketch, "E864", {"start": v(-17.32, 51.64) * mm, "end": v(-17.3, 51.37) * mm});
            skLineSegment(sketch, "E865", {"start": v(-17.3, 51.37) * mm, "end": v(-17.26, 51.1) * mm});
            skLineSegment(sketch, "E866", {"start": v(-17.26, 51.1) * mm, "end": v(-17.22, 50.85) * mm});
            skLineSegment(sketch, "E867", {"start": v(-17.22, 50.85) * mm, "end": v(-17.18, 50.6) * mm});
            skLineSegment(sketch, "E868", {"start": v(-17.18, 50.6) * mm, "end": v(-17.14, 50.37) * mm});
            skLineSegment(sketch, "E869", {"start": v(-17.14, 50.37) * mm, "end": v(-17.1, 50.15) * mm});
            skLineSegment(sketch, "E870", {"start": v(-17.1, 50.15) * mm, "end": v(-17.04, 49.94) * mm});
            skLineSegment(sketch, "E871", {"start": v(-17.04, 49.94) * mm, "end": v(-17, 49.74) * mm});
            skLineSegment(sketch, "E872", {"start": v(-17, 49.74) * mm, "end": v(-16.94, 49.55) * mm});
            skLineSegment(sketch, "E873", {"start": v(-16.94, 49.55) * mm, "end": v(-16.9, 49.37) * mm});
            skLineSegment(sketch, "E874", {"start": v(-16.9, 49.37) * mm, "end": v(-16.84, 49.2) * mm});
            skLineSegment(sketch, "E875", {"start": v(-16.84, 49.2) * mm, "end": v(-16.79, 49.06) * mm});
            skLineSegment(sketch, "E876", {"start": v(-16.79, 49.06) * mm, "end": v(-16.74, 48.91) * mm});
            skLineSegment(sketch, "E877", {"start": v(-16.74, 48.91) * mm, "end": v(-16.69, 48.78) * mm});
            skLineSegment(sketch, "E878", {"start": v(-16.69, 48.78) * mm, "end": v(-16.64, 48.66) * mm});
            skLineSegment(sketch, "E879", {"start": v(-16.64, 48.66) * mm, "end": v(-16.6, 48.55) * mm});
            skLineSegment(sketch, "E880", {"start": v(-16.6, 48.55) * mm, "end": v(-16.55, 48.45) * mm});
            skLineSegment(sketch, "E881", {"start": v(-16.55, 48.45) * mm, "end": v(-16.5, 48.36) * mm});
            skLineSegment(sketch, "E882", {"start": v(-16.5, 48.36) * mm, "end": v(-16.47, 48.28) * mm});
            skLineSegment(sketch, "E883", {"start": v(-16.47, 48.28) * mm, "end": v(-16.43, 48.2) * mm});
            skLineSegment(sketch, "E884", {"start": v(-16.43, 48.2) * mm, "end": v(-16.4, 48.15) * mm});
            skLineSegment(sketch, "E885", {"start": v(-16.4, 48.15) * mm, "end": v(-16.37, 48.1) * mm});
            skLineSegment(sketch, "E886", {"start": v(-16.37, 48.1) * mm, "end": v(-16.35, 48.06) * mm});
            skLineSegment(sketch, "E887", {"start": v(-16.35, 48.06) * mm, "end": v(-16.33, 48.03) * mm});
            skLineSegment(sketch, "E888", {"start": v(-16.33, 48.03) * mm, "end": v(-16.32, 48) * mm});
            skLineSegment(sketch, "E889", {"start": v(-16.32, 48) * mm, "end": v(-16.3, 48) * mm});
            skLineSegment(sketch, "E890", {"start": v(-16.3, 48) * mm, "end": v(-15.13, 46.35) * mm});
            skLineSegment(sketch, "E891", {"start": v(-15.13, 46.35) * mm, "end": v(-18.1, 43.88) * mm});
            skLineSegment(sketch, "E892", {"start": v(-18.1, 43.88) * mm, "end": v(-19.51, 45.33) * mm});
            skLineSegment(sketch, "E893", {"start": v(-19.51, 45.33) * mm, "end": v(-19.52, 45.34) * mm});
            skLineSegment(sketch, "E894", {"start": v(-19.52, 45.34) * mm, "end": v(-19.54, 45.36) * mm});
            skLineSegment(sketch, "E895", {"start": v(-19.54, 45.36) * mm, "end": v(-19.57, 45.38) * mm});
            skLineSegment(sketch, "E896", {"start": v(-19.57, 45.38) * mm, "end": v(-19.6, 45.41) * mm});
            skLineSegment(sketch, "E897", {"start": v(-19.6, 45.41) * mm, "end": v(-19.65, 45.45) * mm});
            skLineSegment(sketch, "E898", {"start": v(-19.65, 45.45) * mm, "end": v(-19.7, 45.5) * mm});
            skLineSegment(sketch, "E899", {"start": v(-19.7, 45.5) * mm, "end": v(-19.76, 45.54) * mm});
            skLineSegment(sketch, "E900", {"start": v(-19.76, 45.54) * mm, "end": v(-19.83, 45.6) * mm});
            skLineSegment(sketch, "E901", {"start": v(-19.83, 45.6) * mm, "end": v(-19.91, 45.65) * mm});
            skLineSegment(sketch, "E902", {"start": v(-19.91, 45.65) * mm, "end": v(-20, 45.71) * mm});
            skLineSegment(sketch, "E903", {"start": v(-20, 45.71) * mm, "end": v(-20.1, 45.78) * mm});
            skLineSegment(sketch, "E904", {"start": v(-20.1, 45.78) * mm, "end": v(-20.22, 45.85) * mm});
            skLineSegment(sketch, "E905", {"start": v(-20.22, 45.85) * mm, "end": v(-20.34, 45.92) * mm});
            skLineSegment(sketch, "E906", {"start": v(-20.34, 45.92) * mm, "end": v(-20.47, 46) * mm});
            skLineSegment(sketch, "E907", {"start": v(-20.47, 46) * mm, "end": v(-20.61, 46.07) * mm});
            skLineSegment(sketch, "E908", {"start": v(-20.61, 46.07) * mm, "end": v(-20.76, 46.16) * mm});
            skLineSegment(sketch, "E909", {"start": v(-20.76, 46.16) * mm, "end": v(-20.93, 46.24) * mm});
            skLineSegment(sketch, "E910", {"start": v(-20.93, 46.24) * mm, "end": v(-21.1, 46.32) * mm});
            skLineSegment(sketch, "E911", {"start": v(-21.1, 46.32) * mm, "end": v(-21.29, 46.4) * mm});
            skLineSegment(sketch, "E912", {"start": v(-21.29, 46.4) * mm, "end": v(-21.49, 46.5) * mm});
            skLineSegment(sketch, "E913", {"start": v(-21.49, 46.5) * mm, "end": v(-21.7, 46.58) * mm});
            skLineSegment(sketch, "E914", {"start": v(-21.7, 46.58) * mm, "end": v(-21.92, 46.66) * mm});
            skLineSegment(sketch, "E915", {"start": v(-21.92, 46.66) * mm, "end": v(-22.15, 46.75) * mm});
            skLineSegment(sketch, "E916", {"start": v(-22.15, 46.75) * mm, "end": v(-22.4, 46.83) * mm});
            skLineSegment(sketch, "E917", {"start": v(-22.4, 46.83) * mm, "end": v(-22.65, 46.91) * mm});
            skLineSegment(sketch, "E918", {"start": v(-22.65, 46.91) * mm, "end": v(-22.92, 47) * mm});
            skLineSegment(sketch, "E919", {"start": v(-22.92, 47) * mm, "end": v(-23.2, 47.07) * mm});
            skLineSegment(sketch, "E920", {"start": v(-23.2, 47.07) * mm, "end": v(-23.49, 47.14) * mm});
            skLineSegment(sketch, "E921", {"start": v(-23.49, 47.14) * mm, "end": v(-23.79, 47.22) * mm});
            skLineSegment(sketch, "E922", {"start": v(-23.79, 47.22) * mm, "end": v(-24.1, 47.28) * mm});
            skLineSegment(sketch, "E923", {"start": v(-24.1, 47.28) * mm, "end": v(-24.43, 47.35) * mm});
            skLineSegment(sketch, "E924", {"start": v(-24.43, 47.35) * mm, "end": v(-24.69, 47.34) * mm});
            skLineSegment(sketch, "E925", {"start": v(-24.69, 47.34) * mm, "end": v(-25.98, 45.8) * mm});
            skLineSegment(sketch, "E926", {"start": v(-25.98, 45.8) * mm, "end": v(-25.95, 45.55) * mm});
            skLineSegment(sketch, "E927", {"start": v(-25.95, 45.55) * mm, "end": v(-25.83, 45.24) * mm});
            skLineSegment(sketch, "E928", {"start": v(-25.83, 45.24) * mm, "end": v(-25.71, 44.94) * mm});
            skLineSegment(sketch, "E929", {"start": v(-25.71, 44.94) * mm, "end": v(-25.6, 44.66) * mm});
            skLineSegment(sketch, "E930", {"start": v(-25.6, 44.66) * mm, "end": v(-25.47, 44.38) * mm});
            skLineSegment(sketch, "E931", {"start": v(-25.47, 44.38) * mm, "end": v(-25.35, 44.12) * mm});
            skLineSegment(sketch, "E932", {"start": v(-25.35, 44.12) * mm, "end": v(-25.23, 43.87) * mm});
            skLineSegment(sketch, "E933", {"start": v(-25.23, 43.87) * mm, "end": v(-25.1, 43.63) * mm});
            skLineSegment(sketch, "E934", {"start": v(-25.1, 43.63) * mm, "end": v(-24.98, 43.4) * mm});
            skLineSegment(sketch, "E935", {"start": v(-24.98, 43.4) * mm, "end": v(-24.86, 43.19) * mm});
            skLineSegment(sketch, "E936", {"start": v(-24.86, 43.19) * mm, "end": v(-24.74, 42.99) * mm});
            skLineSegment(sketch, "E937", {"start": v(-24.74, 42.99) * mm, "end": v(-24.62, 42.8) * mm});
            skLineSegment(sketch, "E938", {"start": v(-24.62, 42.8) * mm, "end": v(-24.5, 42.61) * mm});
            skLineSegment(sketch, "E939", {"start": v(-24.5, 42.61) * mm, "end": v(-24.39, 42.44) * mm});
            skLineSegment(sketch, "E940", {"start": v(-24.39, 42.44) * mm, "end": v(-24.28, 42.28) * mm});
            skLineSegment(sketch, "E941", {"start": v(-24.28, 42.28) * mm, "end": v(-24.17, 42.13) * mm});
            skLineSegment(sketch, "E942", {"start": v(-24.17, 42.13) * mm, "end": v(-24.06, 42) * mm});
            skLineSegment(sketch, "E943", {"start": v(-24.06, 42) * mm, "end": v(-23.96, 41.87) * mm});
            skLineSegment(sketch, "E944", {"start": v(-23.96, 41.87) * mm, "end": v(-23.87, 41.75) * mm});
            skLineSegment(sketch, "E945", {"start": v(-23.87, 41.75) * mm, "end": v(-23.77, 41.64) * mm});
            skLineSegment(sketch, "E946", {"start": v(-23.77, 41.64) * mm, "end": v(-23.69, 41.55) * mm});
            skLineSegment(sketch, "E947", {"start": v(-23.69, 41.55) * mm, "end": v(-23.6, 41.46) * mm});
            skLineSegment(sketch, "E948", {"start": v(-23.6, 41.46) * mm, "end": v(-23.53, 41.38) * mm});
            skLineSegment(sketch, "E949", {"start": v(-23.53, 41.38) * mm, "end": v(-23.46, 41.3) * mm});
            skLineSegment(sketch, "E950", {"start": v(-23.46, 41.3) * mm, "end": v(-23.4, 41.25) * mm});
            skLineSegment(sketch, "E951", {"start": v(-23.4, 41.25) * mm, "end": v(-23.34, 41.2) * mm});
            skLineSegment(sketch, "E952", {"start": v(-23.34, 41.2) * mm, "end": v(-23.29, 41.15) * mm});
            skLineSegment(sketch, "E953", {"start": v(-23.29, 41.15) * mm, "end": v(-23.24, 41.11) * mm});
            skLineSegment(sketch, "E954", {"start": v(-23.24, 41.11) * mm, "end": v(-23.2, 41.08) * mm});
            skLineSegment(sketch, "E955", {"start": v(-23.2, 41.08) * mm, "end": v(-23.18, 41.06) * mm});
            skLineSegment(sketch, "E956", {"start": v(-23.18, 41.06) * mm, "end": v(-23.16, 41.05) * mm});
            skLineSegment(sketch, "E957", {"start": v(-23.16, 41.05) * mm, "end": v(-23.15, 41.04) * mm});
            skLineSegment(sketch, "E958", {"start": v(-23.15, 41.04) * mm, "end": v(-21.48, 39.9) * mm});
            skLineSegment(sketch, "E959", {"start": v(-21.48, 39.9) * mm, "end": v(-23.43, 36.55) * mm});
            skLineSegment(sketch, "E960", {"start": v(-23.43, 36.55) * mm, "end": v(-25.25, 37.44) * mm});
            skLineSegment(sketch, "E961", {"start": v(-25.25, 37.44) * mm, "end": v(-25.26, 37.44) * mm});
            skLineSegment(sketch, "E962", {"start": v(-25.26, 37.44) * mm, "end": v(-25.28, 37.45) * mm});
            skLineSegment(sketch, "E963", {"start": v(-25.28, 37.45) * mm, "end": v(-25.32, 37.47) * mm});
            skLineSegment(sketch, "E964", {"start": v(-25.32, 37.47) * mm, "end": v(-25.36, 37.48) * mm});
            skLineSegment(sketch, "E965", {"start": v(-25.36, 37.48) * mm, "end": v(-25.41, 37.5) * mm});
            skLineSegment(sketch, "E966", {"start": v(-25.41, 37.5) * mm, "end": v(-25.48, 37.52) * mm});
            skLineSegment(sketch, "E967", {"start": v(-25.48, 37.52) * mm, "end": v(-25.55, 37.55) * mm});
            skLineSegment(sketch, "E968", {"start": v(-25.55, 37.55) * mm, "end": v(-25.64, 37.57) * mm});
            skLineSegment(sketch, "E969", {"start": v(-25.64, 37.57) * mm, "end": v(-25.73, 37.6) * mm});
            skLineSegment(sketch, "E970", {"start": v(-25.73, 37.6) * mm, "end": v(-25.84, 37.63) * mm});
            skLineSegment(sketch, "E971", {"start": v(-25.84, 37.63) * mm, "end": v(-25.96, 37.66) * mm});
            skLineSegment(sketch, "E972", {"start": v(-25.96, 37.66) * mm, "end": v(-26.08, 37.68) * mm});
            skLineSegment(sketch, "E973", {"start": v(-26.08, 37.68) * mm, "end": v(-26.22, 37.71) * mm});
            skLineSegment(sketch, "E974", {"start": v(-26.22, 37.71) * mm, "end": v(-26.37, 37.74) * mm});
            skLineSegment(sketch, "E975", {"start": v(-26.37, 37.74) * mm, "end": v(-26.53, 37.76) * mm});
            skLineSegment(sketch, "E976", {"start": v(-26.53, 37.76) * mm, "end": v(-26.7, 37.79) * mm});
            skLineSegment(sketch, "E977", {"start": v(-26.7, 37.79) * mm, "end": v(-26.89, 37.8) * mm});
            skLineSegment(sketch, "E978", {"start": v(-26.89, 37.8) * mm, "end": v(-27.08, 37.83) * mm});
            skLineSegment(sketch, "E979", {"start": v(-27.08, 37.83) * mm, "end": v(-27.29, 37.84) * mm});
            skLineSegment(sketch, "E980", {"start": v(-27.29, 37.84) * mm, "end": v(-27.5, 37.85) * mm});
            skLineSegment(sketch, "E981", {"start": v(-27.5, 37.85) * mm, "end": v(-27.73, 37.86) * mm});
            skLineSegment(sketch, "E982", {"start": v(-27.73, 37.86) * mm, "end": v(-27.96, 37.87) * mm});
            skLineSegment(sketch, "E983", {"start": v(-27.96, 37.87) * mm, "end": v(-28.2, 37.87) * mm});
            skLineSegment(sketch, "E984", {"start": v(-28.2, 37.87) * mm, "end": v(-28.47, 37.86) * mm});
            skLineSegment(sketch, "E985", {"start": v(-28.47, 37.86) * mm, "end": v(-28.74, 37.85) * mm});
            skLineSegment(sketch, "E986", {"start": v(-28.74, 37.85) * mm, "end": v(-29.01, 37.84) * mm});
            skLineSegment(sketch, "E987", {"start": v(-29.01, 37.84) * mm, "end": v(-29.3, 37.81) * mm});
            skLineSegment(sketch, "E988", {"start": v(-29.3, 37.81) * mm, "end": v(-29.6, 37.78) * mm});
            skLineSegment(sketch, "E989", {"start": v(-29.6, 37.78) * mm, "end": v(-29.9, 37.75) * mm});
            skLineSegment(sketch, "E990", {"start": v(-29.9, 37.75) * mm, "end": v(-30.23, 37.7) * mm});
            skLineSegment(sketch, "E991", {"start": v(-30.23, 37.7) * mm, "end": v(-30.56, 37.65) * mm});
            skLineSegment(sketch, "E992", {"start": v(-30.56, 37.65) * mm, "end": v(-30.8, 37.55) * mm});
            skLineSegment(sketch, "E993", {"start": v(-30.8, 37.55) * mm, "end": v(-31.49, 35.67) * mm});
            skLineSegment(sketch, "E994", {"start": v(-31.49, 35.67) * mm, "end": v(-31.37, 35.44) * mm});
            skLineSegment(sketch, "E995", {"start": v(-31.37, 35.44) * mm, "end": v(-31.15, 35.2) * mm});
            skLineSegment(sketch, "E996", {"start": v(-31.15, 35.2) * mm, "end": v(-30.94, 34.95) * mm});
            skLineSegment(sketch, "E997", {"start": v(-30.94, 34.95) * mm, "end": v(-30.73, 34.72) * mm});
            skLineSegment(sketch, "E998", {"start": v(-30.73, 34.72) * mm, "end": v(-30.52, 34.5) * mm});
            skLineSegment(sketch, "E999", {"start": v(-30.52, 34.5) * mm, "end": v(-30.32, 34.3) * mm});
            skLineSegment(sketch, "E1000", {"start": v(-30.32, 34.3) * mm, "end": v(-30.12, 34.11) * mm});
            skLineSegment(sketch, "E1001", {"start": v(-30.12, 34.11) * mm, "end": v(-29.92, 33.93) * mm});
            skLineSegment(sketch, "E1002", {"start": v(-29.92, 33.93) * mm, "end": v(-29.73, 33.76) * mm});
            skLineSegment(sketch, "E1003", {"start": v(-29.73, 33.76) * mm, "end": v(-29.54, 33.6) * mm});
            skLineSegment(sketch, "E1004", {"start": v(-29.54, 33.6) * mm, "end": v(-29.36, 33.45) * mm});
            skLineSegment(sketch, "E1005", {"start": v(-29.36, 33.45) * mm, "end": v(-29.18, 33.3) * mm});
            skLineSegment(sketch, "E1006", {"start": v(-29.18, 33.3) * mm, "end": v(-29, 33.18) * mm});
            skLineSegment(sketch, "E1007", {"start": v(-29, 33.18) * mm, "end": v(-28.84, 33.06) * mm});
            skLineSegment(sketch, "E1008", {"start": v(-28.84, 33.06) * mm, "end": v(-28.68, 32.95) * mm});
            skLineSegment(sketch, "E1009", {"start": v(-28.68, 32.95) * mm, "end": v(-28.53, 32.84) * mm});
            skLineSegment(sketch, "E1010", {"start": v(-28.53, 32.84) * mm, "end": v(-28.38, 32.75) * mm});
            skLineSegment(sketch, "E1011", {"start": v(-28.38, 32.75) * mm, "end": v(-28.24, 32.66) * mm});
            skLineSegment(sketch, "E1012", {"start": v(-28.24, 32.66) * mm, "end": v(-28.11, 32.59) * mm});
            skLineSegment(sketch, "E1013", {"start": v(-28.11, 32.59) * mm, "end": v(-28, 32.52) * mm});
            skLineSegment(sketch, "E1014", {"start": v(-28, 32.52) * mm, "end": v(-27.88, 32.46) * mm});
            skLineSegment(sketch, "E1015", {"start": v(-27.88, 32.46) * mm, "end": v(-27.77, 32.4) * mm});
            skLineSegment(sketch, "E1016", {"start": v(-27.77, 32.4) * mm, "end": v(-27.67, 32.35) * mm});
            skLineSegment(sketch, "E1017", {"start": v(-27.67, 32.35) * mm, "end": v(-27.58, 32.3) * mm});
            skLineSegment(sketch, "E1018", {"start": v(-27.58, 32.3) * mm, "end": v(-27.5, 32.27) * mm});
            skLineSegment(sketch, "E1019", {"start": v(-27.5, 32.27) * mm, "end": v(-27.43, 32.24) * mm});
            skLineSegment(sketch, "E1020", {"start": v(-27.43, 32.24) * mm, "end": v(-27.36, 32.22) * mm});
            skLineSegment(sketch, "E1021", {"start": v(-27.36, 32.22) * mm, "end": v(-27.3, 32.2) * mm});
            skLineSegment(sketch, "E1022", {"start": v(-27.3, 32.2) * mm, "end": v(-27.27, 32.18) * mm});
            skLineSegment(sketch, "E1023", {"start": v(-27.27, 32.18) * mm, "end": v(-27.23, 32.17) * mm});
            skLineSegment(sketch, "E1024", {"start": v(-27.23, 32.17) * mm, "end": v(-27.2, 32.16) * mm});
            skLineSegment(sketch, "E1025", {"start": v(-27.2, 32.16) * mm, "end": v(-27.2, 32.16) * mm});
            skLineSegment(sketch, "E1026", {"start": v(-27.2, 32.16) * mm, "end": v(-25.24, 31.65) * mm});
            skLineSegment(sketch, "E1027", {"start": v(-25.24, 31.65) * mm, "end": v(-25.93, 27.85) * mm});
            skLineSegment(sketch, "E1028", {"start": v(-25.93, 27.85) * mm, "end": v(-27.94, 28.06) * mm});
            skLineSegment(sketch, "E1029", {"start": v(-27.94, 28.06) * mm, "end": v(-27.95, 28.06) * mm});
            skLineSegment(sketch, "E1030", {"start": v(-27.95, 28.06) * mm, "end": v(-27.98, 28.06) * mm});
            skLineSegment(sketch, "E1031", {"start": v(-27.98, 28.06) * mm, "end": v(-28.01, 28.06) * mm});
            skLineSegment(sketch, "E1032", {"start": v(-28.01, 28.06) * mm, "end": v(-28.06, 28.06) * mm});
            skLineSegment(sketch, "E1033", {"start": v(-28.06, 28.06) * mm, "end": v(-28.11, 28.06) * mm});
            skLineSegment(sketch, "E1034", {"start": v(-28.11, 28.06) * mm, "end": v(-28.18, 28.06) * mm});
            skLineSegment(sketch, "E1035", {"start": v(-28.18, 28.06) * mm, "end": v(-28.26, 28.06) * mm});
            skLineSegment(sketch, "E1036", {"start": v(-28.26, 28.06) * mm, "end": v(-28.35, 28.05) * mm});
            skLineSegment(sketch, "E1037", {"start": v(-28.35, 28.05) * mm, "end": v(-28.45, 28.05) * mm});
            skLineSegment(sketch, "E1038", {"start": v(-28.45, 28.05) * mm, "end": v(-28.56, 28.04) * mm});
            skLineSegment(sketch, "E1039", {"start": v(-28.56, 28.04) * mm, "end": v(-28.68, 28.02) * mm});
            skLineSegment(sketch, "E1040", {"start": v(-28.68, 28.02) * mm, "end": v(-28.8, 28) * mm});
            skLineSegment(sketch, "E1041", {"start": v(-28.8, 28) * mm, "end": v(-28.95, 27.98) * mm});
            skLineSegment(sketch, "E1042", {"start": v(-28.95, 27.98) * mm, "end": v(-29.1, 27.96) * mm});
            skLineSegment(sketch, "E1043", {"start": v(-29.1, 27.96) * mm, "end": v(-29.26, 27.92) * mm});
            skLineSegment(sketch, "E1044", {"start": v(-29.26, 27.92) * mm, "end": v(-29.43, 27.89) * mm});
            skLineSegment(sketch, "E1045", {"start": v(-29.43, 27.89) * mm, "end": v(-29.6, 27.85) * mm});
            skLineSegment(sketch, "E1046", {"start": v(-29.6, 27.85) * mm, "end": v(-29.8, 27.8) * mm});
            skLineSegment(sketch, "E1047", {"start": v(-29.8, 27.8) * mm, "end": v(-29.99, 27.74) * mm});
            skLineSegment(sketch, "E1048", {"start": v(-29.99, 27.74) * mm, "end": v(-30.2, 27.68) * mm});
            skLineSegment(sketch, "E1049", {"start": v(-30.2, 27.68) * mm, "end": v(-30.41, 27.61) * mm});
            skLineSegment(sketch, "E1050", {"start": v(-30.41, 27.61) * mm, "end": v(-30.64, 27.53) * mm});
            skLineSegment(sketch, "E1051", {"start": v(-30.64, 27.53) * mm, "end": v(-30.87, 27.45) * mm});
            skLineSegment(sketch, "E1052", {"start": v(-30.87, 27.45) * mm, "end": v(-31.1, 27.36) * mm});
            skLineSegment(sketch, "E1053", {"start": v(-31.1, 27.36) * mm, "end": v(-31.36, 27.26) * mm});
            skLineSegment(sketch, "E1054", {"start": v(-31.36, 27.26) * mm, "end": v(-31.61, 27.15) * mm});
            skLineSegment(sketch, "E1055", {"start": v(-31.61, 27.15) * mm, "end": v(-31.88, 27.03) * mm});
            skLineSegment(sketch, "E1056", {"start": v(-31.88, 27.03) * mm, "end": v(-32.15, 26.9) * mm});
            skLineSegment(sketch, "E1057", {"start": v(-32.15, 26.9) * mm, "end": v(-32.42, 26.76) * mm});
            skLineSegment(sketch, "E1058", {"start": v(-32.42, 26.76) * mm, "end": v(-32.7, 26.6) * mm});
            skLineSegment(sketch, "E1059", {"start": v(-32.7, 26.6) * mm, "end": v(-33, 26.45) * mm});
            skLineSegment(sketch, "E1060", {"start": v(-33, 26.45) * mm, "end": v(-33.19, 26.27) * mm});
            skLineSegment(sketch, "E1061", {"start": v(-33.19, 26.27) * mm, "end": v(-33.2, 24.27) * mm});
            skLineSegment(sketch, "E1062", {"start": v(-33.2, 24.27) * mm, "end": v(-33, 24.1) * mm});
            skLineSegment(sketch, "E1063", {"start": v(-33, 24.1) * mm, "end": v(-32.72, 23.93) * mm});
            skLineSegment(sketch, "E1064", {"start": v(-32.72, 23.93) * mm, "end": v(-32.44, 23.78) * mm});
            skLineSegment(sketch, "E1065", {"start": v(-32.44, 23.78) * mm, "end": v(-32.16, 23.64) * mm});
            skLineSegment(sketch, "E1066", {"start": v(-32.16, 23.64) * mm, "end": v(-31.9, 23.5) * mm});
            skLineSegment(sketch, "E1067", {"start": v(-31.9, 23.5) * mm, "end": v(-31.63, 23.38) * mm});
            skLineSegment(sketch, "E1068", {"start": v(-31.63, 23.38) * mm, "end": v(-31.37, 23.27) * mm});
            skLineSegment(sketch, "E1069", {"start": v(-31.37, 23.27) * mm, "end": v(-31.13, 23.17) * mm});
            skLineSegment(sketch, "E1070", {"start": v(-31.13, 23.17) * mm, "end": v(-30.89, 23.07) * mm});
            skLineSegment(sketch, "E1071", {"start": v(-30.89, 23.07) * mm, "end": v(-30.66, 22.98) * mm});
            skLineSegment(sketch, "E1072", {"start": v(-30.66, 22.98) * mm, "end": v(-30.43, 22.9) * mm});
            skLineSegment(sketch, "E1073", {"start": v(-30.43, 22.9) * mm, "end": v(-30.22, 22.83) * mm});
            skLineSegment(sketch, "E1074", {"start": v(-30.22, 22.83) * mm, "end": v(-30.01, 22.77) * mm});
            skLineSegment(sketch, "E1075", {"start": v(-30.01, 22.77) * mm, "end": v(-29.81, 22.71) * mm});
            skLineSegment(sketch, "E1076", {"start": v(-29.81, 22.71) * mm, "end": v(-29.63, 22.66) * mm});
            skLineSegment(sketch, "E1077", {"start": v(-29.63, 22.66) * mm, "end": v(-29.45, 22.62) * mm});
            skLineSegment(sketch, "E1078", {"start": v(-29.45, 22.62) * mm, "end": v(-29.28, 22.58) * mm});
            skLineSegment(sketch, "E1079", {"start": v(-29.28, 22.58) * mm, "end": v(-29.12, 22.55) * mm});
            skLineSegment(sketch, "E1080", {"start": v(-29.12, 22.55) * mm, "end": v(-28.97, 22.52) * mm});
            skLineSegment(sketch, "E1081", {"start": v(-28.97, 22.52) * mm, "end": v(-28.83, 22.5) * mm});
            skLineSegment(sketch, "E1082", {"start": v(-28.83, 22.5) * mm, "end": v(-28.7, 22.48) * mm});
            skLineSegment(sketch, "E1083", {"start": v(-28.7, 22.48) * mm, "end": v(-28.58, 22.46) * mm});
            skLineSegment(sketch, "E1084", {"start": v(-28.58, 22.46) * mm, "end": v(-28.47, 22.45) * mm});
            skLineSegment(sketch, "E1085", {"start": v(-28.47, 22.45) * mm, "end": v(-28.37, 22.44) * mm});
            skLineSegment(sketch, "E1086", {"start": v(-28.37, 22.44) * mm, "end": v(-28.29, 22.44) * mm});
            skLineSegment(sketch, "E1087", {"start": v(-28.29, 22.44) * mm, "end": v(-28.2, 22.43) * mm});
            skLineSegment(sketch, "E1088", {"start": v(-28.2, 22.43) * mm, "end": v(-28.14, 22.43) * mm});
            skLineSegment(sketch, "E1089", {"start": v(-28.14, 22.43) * mm, "end": v(-28.08, 22.43) * mm});
            skLineSegment(sketch, "E1090", {"start": v(-28.08, 22.43) * mm, "end": v(-28.04, 22.43) * mm});
            skLineSegment(sketch, "E1091", {"start": v(-28.04, 22.43) * mm, "end": v(-28, 22.43) * mm});
            skLineSegment(sketch, "E1092", {"start": v(-28, 22.43) * mm, "end": v(-27.98, 22.43) * mm});
            skLineSegment(sketch, "E1093", {"start": v(-27.98, 22.43) * mm, "end": v(-27.96, 22.44) * mm});
            skLineSegment(sketch, "E1094", {"start": v(-27.96, 22.44) * mm, "end": v(-25.95, 22.63) * mm});
            skLineSegment(sketch, "E1095", {"start": v(-25.95, 22.63) * mm, "end": v(-25.3, 18.82) * mm});
            skLineSegment(sketch, "E1096", {"start": v(-25.3, 18.82) * mm, "end": v(-27.25, 18.33) * mm});
            skLineSegment(sketch, "E1097", {"start": v(-27.25, 18.33) * mm, "end": v(-27.27, 18.32) * mm});
            skLineSegment(sketch, "E1098", {"start": v(-27.27, 18.32) * mm, "end": v(-27.3, 18.32) * mm});
            skLineSegment(sketch, "E1099", {"start": v(-27.3, 18.32) * mm, "end": v(-27.33, 18.3) * mm});
            skLineSegment(sketch, "E1100", {"start": v(-27.33, 18.3) * mm, "end": v(-27.37, 18.3) * mm});
            skLineSegment(sketch, "E1101", {"start": v(-27.37, 18.3) * mm, "end": v(-27.43, 18.27) * mm});
            skLineSegment(sketch, "E1102", {"start": v(-27.43, 18.27) * mm, "end": v(-27.49, 18.25) * mm});
            skLineSegment(sketch, "E1103", {"start": v(-27.49, 18.25) * mm, "end": v(-27.56, 18.22) * mm});
            skLineSegment(sketch, "E1104", {"start": v(-27.56, 18.22) * mm, "end": v(-27.64, 18.18) * mm});
            skLineSegment(sketch, "E1105", {"start": v(-27.64, 18.18) * mm, "end": v(-27.73, 18.14) * mm});
            skLineSegment(sketch, "E1106", {"start": v(-27.73, 18.14) * mm, "end": v(-27.83, 18.1) * mm});
            skLineSegment(sketch, "E1107", {"start": v(-27.83, 18.1) * mm, "end": v(-27.94, 18.04) * mm});
            skLineSegment(sketch, "E1108", {"start": v(-27.94, 18.04) * mm, "end": v(-28.05, 17.98) * mm});
            skLineSegment(sketch, "E1109", {"start": v(-28.05, 17.98) * mm, "end": v(-28.18, 17.9) * mm});
            skLineSegment(sketch, "E1110", {"start": v(-28.18, 17.9) * mm, "end": v(-28.31, 17.83) * mm});
            skLineSegment(sketch, "E1111", {"start": v(-28.31, 17.83) * mm, "end": v(-28.45, 17.75) * mm});
            skLineSegment(sketch, "E1112", {"start": v(-28.45, 17.75) * mm, "end": v(-28.6, 17.66) * mm});
            skLineSegment(sketch, "E1113", {"start": v(-28.6, 17.66) * mm, "end": v(-28.75, 17.56) * mm});
            skLineSegment(sketch, "E1114", {"start": v(-28.75, 17.56) * mm, "end": v(-28.91, 17.45) * mm});
            skLineSegment(sketch, "E1115", {"start": v(-28.91, 17.45) * mm, "end": v(-29.08, 17.33) * mm});
            skLineSegment(sketch, "E1116", {"start": v(-29.08, 17.33) * mm, "end": v(-29.25, 17.2) * mm});
            skLineSegment(sketch, "E1117", {"start": v(-29.25, 17.2) * mm, "end": v(-29.43, 17.06) * mm});
            skLineSegment(sketch, "E1118", {"start": v(-29.43, 17.06) * mm, "end": v(-29.61, 16.91) * mm});
            skLineSegment(sketch, "E1119", {"start": v(-29.61, 16.91) * mm, "end": v(-29.8, 16.75) * mm});
            skLineSegment(sketch, "E1120", {"start": v(-29.8, 16.75) * mm, "end": v(-30, 16.58) * mm});
            skLineSegment(sketch, "E1121", {"start": v(-30, 16.58) * mm, "end": v(-30.2, 16.4) * mm});
            skLineSegment(sketch, "E1122", {"start": v(-30.2, 16.4) * mm, "end": v(-30.4, 16.21) * mm});
            skLineSegment(sketch, "E1123", {"start": v(-30.4, 16.21) * mm, "end": v(-30.6, 16) * mm});
            skLineSegment(sketch, "E1124", {"start": v(-30.6, 16) * mm, "end": v(-30.81, 15.8) * mm});
            skLineSegment(sketch, "E1125", {"start": v(-30.81, 15.8) * mm, "end": v(-31.03, 15.57) * mm});
            skLineSegment(sketch, "E1126", {"start": v(-31.03, 15.57) * mm, "end": v(-31.24, 15.33) * mm});
            skLineSegment(sketch, "E1127", {"start": v(-31.24, 15.33) * mm, "end": v(-31.46, 15.08) * mm});
            skLineSegment(sketch, "E1128", {"start": v(-31.46, 15.08) * mm, "end": v(-31.58, 14.85) * mm});
            skLineSegment(sketch, "E1129", {"start": v(-31.58, 14.85) * mm, "end": v(-30.9, 12.97) * mm});
            skLineSegment(sketch, "E1130", {"start": v(-30.9, 12.97) * mm, "end": v(-30.67, 12.87) * mm});
            skLineSegment(sketch, "E1131", {"start": v(-30.67, 12.87) * mm, "end": v(-30.34, 12.81) * mm});
            skLineSegment(sketch, "E1132", {"start": v(-30.34, 12.81) * mm, "end": v(-30.02, 12.76) * mm});
            skLineSegment(sketch, "E1133", {"start": v(-30.02, 12.76) * mm, "end": v(-29.71, 12.73) * mm});
            skLineSegment(sketch, "E1134", {"start": v(-29.71, 12.73) * mm, "end": v(-29.41, 12.7) * mm});
            skLineSegment(sketch, "E1135", {"start": v(-29.41, 12.7) * mm, "end": v(-29.13, 12.67) * mm});
            skLineSegment(sketch, "E1136", {"start": v(-29.13, 12.67) * mm, "end": v(-28.85, 12.65) * mm});
            skLineSegment(sketch, "E1137", {"start": v(-28.85, 12.65) * mm, "end": v(-28.58, 12.64) * mm});
            skLineSegment(sketch, "E1138", {"start": v(-28.58, 12.64) * mm, "end": v(-28.32, 12.63) * mm});
            skLineSegment(sketch, "E1139", {"start": v(-28.32, 12.63) * mm, "end": v(-28.07, 12.63) * mm});
            skLineSegment(sketch, "E1140", {"start": v(-28.07, 12.63) * mm, "end": v(-27.84, 12.63) * mm});
            skLineSegment(sketch, "E1141", {"start": v(-27.84, 12.63) * mm, "end": v(-27.61, 12.64) * mm});
            skLineSegment(sketch, "E1142", {"start": v(-27.61, 12.64) * mm, "end": v(-27.4, 12.65) * mm});
            skLineSegment(sketch, "E1143", {"start": v(-27.4, 12.65) * mm, "end": v(-27.2, 12.66) * mm});
            skLineSegment(sketch, "E1144", {"start": v(-27.2, 12.66) * mm, "end": v(-27, 12.68) * mm});
            skLineSegment(sketch, "E1145", {"start": v(-27, 12.68) * mm, "end": v(-26.82, 12.7) * mm});
            skLineSegment(sketch, "E1146", {"start": v(-26.82, 12.7) * mm, "end": v(-26.64, 12.72) * mm});
            skLineSegment(sketch, "E1147", {"start": v(-26.64, 12.72) * mm, "end": v(-26.48, 12.74) * mm});
            skLineSegment(sketch, "E1148", {"start": v(-26.48, 12.74) * mm, "end": v(-26.33, 12.77) * mm});
            skLineSegment(sketch, "E1149", {"start": v(-26.33, 12.77) * mm, "end": v(-26.2, 12.8) * mm});
            skLineSegment(sketch, "E1150", {"start": v(-26.2, 12.8) * mm, "end": v(-26.07, 12.82) * mm});
            skLineSegment(sketch, "E1151", {"start": v(-26.07, 12.82) * mm, "end": v(-25.95, 12.85) * mm});
            skLineSegment(sketch, "E1152", {"start": v(-25.95, 12.85) * mm, "end": v(-25.84, 12.88) * mm});
            skLineSegment(sketch, "E1153", {"start": v(-25.84, 12.88) * mm, "end": v(-25.75, 12.9) * mm});
            skLineSegment(sketch, "E1154", {"start": v(-25.75, 12.9) * mm, "end": v(-25.66, 12.93) * mm});
            skLineSegment(sketch, "E1155", {"start": v(-25.66, 12.93) * mm, "end": v(-25.59, 12.95) * mm});
            skLineSegment(sketch, "E1156", {"start": v(-25.59, 12.95) * mm, "end": v(-25.52, 12.97) * mm});
            skLineSegment(sketch, "E1157", {"start": v(-25.52, 12.97) * mm, "end": v(-25.47, 12.99) * mm});
            skLineSegment(sketch, "E1158", {"start": v(-25.47, 12.99) * mm, "end": v(-25.43, 13) * mm});
            skLineSegment(sketch, "E1159", {"start": v(-25.43, 13) * mm, "end": v(-25.4, 13.02) * mm});
            skLineSegment(sketch, "E1160", {"start": v(-25.4, 13.02) * mm, "end": v(-25.37, 13.03) * mm});
            skLineSegment(sketch, "E1161", {"start": v(-25.37, 13.03) * mm, "end": v(-25.35, 13.03) * mm});
            skLineSegment(sketch, "E1162", {"start": v(-25.35, 13.03) * mm, "end": v(-23.53, 13.9) * mm});
            skLineSegment(sketch, "E1163", {"start": v(-23.53, 13.9) * mm, "end": v(-21.61, 10.55) * mm});
            skLineSegment(sketch, "E1164", {"start": v(-21.61, 10.55) * mm, "end": v(-23.29, 9.42) * mm});
            skLineSegment(sketch, "E1165", {"start": v(-23.29, 9.42) * mm, "end": v(-23.3, 9.4) * mm});
            skLineSegment(sketch, "E1166", {"start": v(-23.3, 9.4) * mm, "end": v(-23.32, 9.4) * mm});
            skLineSegment(sketch, "E1167", {"start": v(-23.32, 9.4) * mm, "end": v(-23.35, 9.37) * mm});
            skLineSegment(sketch, "E1168", {"start": v(-23.35, 9.37) * mm, "end": v(-23.38, 9.34) * mm});
            skLineSegment(sketch, "E1169", {"start": v(-23.38, 9.34) * mm, "end": v(-23.43, 9.3) * mm});
            skLineSegment(sketch, "E1170", {"start": v(-23.43, 9.3) * mm, "end": v(-23.48, 9.26) * mm});
            skLineSegment(sketch, "E1171", {"start": v(-23.48, 9.26) * mm, "end": v(-23.54, 9.2) * mm});
            skLineSegment(sketch, "E1172", {"start": v(-23.54, 9.2) * mm, "end": v(-23.6, 9.15) * mm});
            skLineSegment(sketch, "E1173", {"start": v(-23.6, 9.15) * mm, "end": v(-23.67, 9.08) * mm});
            skLineSegment(sketch, "E1174", {"start": v(-23.67, 9.08) * mm, "end": v(-23.75, 9) * mm});
            skLineSegment(sketch, "E1175", {"start": v(-23.75, 9) * mm, "end": v(-23.83, 8.91) * mm});
            skLineSegment(sketch, "E1176", {"start": v(-23.83, 8.91) * mm, "end": v(-23.92, 8.81) * mm});
            skLineSegment(sketch, "E1177", {"start": v(-23.92, 8.81) * mm, "end": v(-24.01, 8.7) * mm});
            skLineSegment(sketch, "E1178", {"start": v(-24.01, 8.7) * mm, "end": v(-24.11, 8.6) * mm});
            skLineSegment(sketch, "E1179", {"start": v(-24.11, 8.6) * mm, "end": v(-24.21, 8.46) * mm});
            skLineSegment(sketch, "E1180", {"start": v(-24.21, 8.46) * mm, "end": v(-24.32, 8.33) * mm});
            skLineSegment(sketch, "E1181", {"start": v(-24.32, 8.33) * mm, "end": v(-24.43, 8.18) * mm});
            skLineSegment(sketch, "E1182", {"start": v(-24.43, 8.18) * mm, "end": v(-24.54, 8.02) * mm});
            skLineSegment(sketch, "E1183", {"start": v(-24.54, 8.02) * mm, "end": v(-24.66, 7.85) * mm});
            skLineSegment(sketch, "E1184", {"start": v(-24.66, 7.85) * mm, "end": v(-24.78, 7.67) * mm});
            skLineSegment(sketch, "E1185", {"start": v(-24.78, 7.67) * mm, "end": v(-24.9, 7.48) * mm});
            skLineSegment(sketch, "E1186", {"start": v(-24.9, 7.48) * mm, "end": v(-25.02, 7.28) * mm});
            skLineSegment(sketch, "E1187", {"start": v(-25.02, 7.28) * mm, "end": v(-25.14, 7.06) * mm});
            skLineSegment(sketch, "E1188", {"start": v(-25.14, 7.06) * mm, "end": v(-25.27, 6.84) * mm});
            skLineSegment(sketch, "E1189", {"start": v(-25.27, 6.84) * mm, "end": v(-25.4, 6.6) * mm});
            skLineSegment(sketch, "E1190", {"start": v(-25.4, 6.6) * mm, "end": v(-25.52, 6.35) * mm});
            skLineSegment(sketch, "E1191", {"start": v(-25.52, 6.35) * mm, "end": v(-25.64, 6.1) * mm});
            skLineSegment(sketch, "E1192", {"start": v(-25.64, 6.1) * mm, "end": v(-25.77, 5.82) * mm});
            skLineSegment(sketch, "E1193", {"start": v(-25.77, 5.82) * mm, "end": v(-25.89, 5.53) * mm});
            skLineSegment(sketch, "E1194", {"start": v(-25.89, 5.53) * mm, "end": v(-26, 5.24) * mm});
            skLineSegment(sketch, "E1195", {"start": v(-26, 5.24) * mm, "end": v(-26.13, 4.93) * mm});
            skLineSegment(sketch, "E1196", {"start": v(-26.13, 4.93) * mm, "end": v(-26.16, 4.67) * mm});
            skLineSegment(sketch, "E1197", {"start": v(-26.16, 4.67) * mm, "end": v(-24.88, 3.13) * mm});
            skLineSegment(sketch, "E1198", {"start": v(-24.88, 3.13) * mm, "end": v(-24.62, 3.12) * mm});
            skLineSegment(sketch, "E1199", {"start": v(-24.62, 3.12) * mm, "end": v(-24.3, 3.18) * mm});
            skLineSegment(sketch, "E1200", {"start": v(-24.3, 3.18) * mm, "end": v(-23.98, 3.24) * mm});
            skLineSegment(sketch, "E1201", {"start": v(-23.98, 3.24) * mm, "end": v(-23.68, 3.31) * mm});
            skLineSegment(sketch, "E1202", {"start": v(-23.68, 3.31) * mm, "end": v(-23.39, 3.38) * mm});
            skLineSegment(sketch, "E1203", {"start": v(-23.39, 3.38) * mm, "end": v(-23.1, 3.46) * mm});
            skLineSegment(sketch, "E1204", {"start": v(-23.1, 3.46) * mm, "end": v(-22.84, 3.54) * mm});
            skLineSegment(sketch, "E1205", {"start": v(-22.84, 3.54) * mm, "end": v(-22.59, 3.62) * mm});
            skLineSegment(sketch, "E1206", {"start": v(-22.59, 3.62) * mm, "end": v(-22.34, 3.7) * mm});
            skLineSegment(sketch, "E1207", {"start": v(-22.34, 3.7) * mm, "end": v(-22.1, 3.78) * mm});
            skLineSegment(sketch, "E1208", {"start": v(-22.1, 3.78) * mm, "end": v(-21.89, 3.86) * mm});
            skLineSegment(sketch, "E1209", {"start": v(-21.89, 3.86) * mm, "end": v(-21.68, 3.95) * mm});
            skLineSegment(sketch, "E1210", {"start": v(-21.68, 3.95) * mm, "end": v(-21.48, 4.03) * mm});
            skLineSegment(sketch, "E1211", {"start": v(-21.48, 4.03) * mm, "end": v(-21.3, 4.11) * mm});
            skLineSegment(sketch, "E1212", {"start": v(-21.3, 4.11) * mm, "end": v(-21.11, 4.2) * mm});
            skLineSegment(sketch, "E1213", {"start": v(-21.11, 4.2) * mm, "end": v(-20.95, 4.28) * mm});
            skLineSegment(sketch, "E1214", {"start": v(-20.95, 4.28) * mm, "end": v(-20.8, 4.36) * mm});
            skLineSegment(sketch, "E1215", {"start": v(-20.8, 4.36) * mm, "end": v(-20.65, 4.43) * mm});
            skLineSegment(sketch, "E1216", {"start": v(-20.65, 4.43) * mm, "end": v(-20.52, 4.5) * mm});
            skLineSegment(sketch, "E1217", {"start": v(-20.52, 4.5) * mm, "end": v(-20.4, 4.58) * mm});
            skLineSegment(sketch, "E1218", {"start": v(-20.4, 4.58) * mm, "end": v(-20.29, 4.65) * mm});
            skLineSegment(sketch, "E1219", {"start": v(-20.29, 4.65) * mm, "end": v(-20.19, 4.71) * mm});
            skLineSegment(sketch, "E1220", {"start": v(-20.19, 4.71) * mm, "end": v(-20.1, 4.78) * mm});
            skLineSegment(sketch, "E1221", {"start": v(-20.1, 4.78) * mm, "end": v(-20.01, 4.83) * mm});
            skLineSegment(sketch, "E1222", {"start": v(-20.01, 4.83) * mm, "end": v(-19.94, 4.88) * mm});
            skLineSegment(sketch, "E1223", {"start": v(-19.94, 4.88) * mm, "end": v(-19.88, 4.93) * mm});
            skLineSegment(sketch, "E1224", {"start": v(-19.88, 4.93) * mm, "end": v(-19.83, 4.97) * mm});
            skLineSegment(sketch, "E1225", {"start": v(-19.83, 4.97) * mm, "end": v(-19.78, 5.01) * mm});
            skLineSegment(sketch, "E1226", {"start": v(-19.78, 5.01) * mm, "end": v(-19.75, 5.04) * mm});
            skLineSegment(sketch, "E1227", {"start": v(-19.75, 5.04) * mm, "end": v(-19.72, 5.06) * mm});
            skLineSegment(sketch, "E1228", {"start": v(-19.72, 5.06) * mm, "end": v(-19.7, 5.08) * mm});
            skLineSegment(sketch, "E1229", {"start": v(-19.7, 5.08) * mm, "end": v(-19.7, 5.1) * mm});
            skLineSegment(sketch, "E1230", {"start": v(-19.7, 5.1) * mm, "end": v(-18.27, 6.53) * mm});
            skLineSegment(sketch, "E1231", {"start": v(-18.27, 6.53) * mm, "end": v(-15.32, 4.03) * mm});
            skLineSegment(sketch, "E1232", {"start": v(-15.32, 4.03) * mm, "end": v(-16.51, 2.4) * mm});
            skLineSegment(sketch, "E1233", {"start": v(-16.51, 2.4) * mm, "end": v(-16.52, 2.39) * mm});
            skLineSegment(sketch, "E1234", {"start": v(-16.52, 2.39) * mm, "end": v(-16.53, 2.37) * mm});
            skLineSegment(sketch, "E1235", {"start": v(-16.53, 2.37) * mm, "end": v(-16.55, 2.33) * mm});
            skLineSegment(sketch, "E1236", {"start": v(-16.55, 2.33) * mm, "end": v(-16.58, 2.3) * mm});
            skLineSegment(sketch, "E1237", {"start": v(-16.58, 2.3) * mm, "end": v(-16.6, 2.25) * mm});
            skLineSegment(sketch, "E1238", {"start": v(-16.6, 2.25) * mm, "end": v(-16.64, 2.19) * mm});
            skLineSegment(sketch, "E1239", {"start": v(-16.64, 2.19) * mm, "end": v(-16.67, 2.12) * mm});
            skLineSegment(sketch, "E1240", {"start": v(-16.67, 2.12) * mm, "end": v(-16.71, 2.04) * mm});
            skLineSegment(sketch, "E1241", {"start": v(-16.71, 2.04) * mm, "end": v(-16.76, 1.95) * mm});
            skLineSegment(sketch, "E1242", {"start": v(-16.76, 1.95) * mm, "end": v(-16.8, 1.85) * mm});
            skLineSegment(sketch, "E1243", {"start": v(-16.8, 1.85) * mm, "end": v(-16.85, 1.74) * mm});
            skLineSegment(sketch, "E1244", {"start": v(-16.85, 1.74) * mm, "end": v(-16.9, 1.62) * mm});
            skLineSegment(sketch, "E1245", {"start": v(-16.9, 1.62) * mm, "end": v(-16.95, 1.48) * mm});
            skLineSegment(sketch, "E1246", {"start": v(-16.95, 1.48) * mm, "end": v(-17, 1.34) * mm});
            skLineSegment(sketch, "E1247", {"start": v(-17, 1.34) * mm, "end": v(-17.05, 1.19) * mm});
            skLineSegment(sketch, "E1248", {"start": v(-17.05, 1.19) * mm, "end": v(-17.1, 1.02) * mm});
            skLineSegment(sketch, "E1249", {"start": v(-17.1, 1.02) * mm, "end": v(-17.16, 0.85) * mm});
            skLineSegment(sketch, "E1250", {"start": v(-17.16, 0.85) * mm, "end": v(-17.21, 0.66) * mm});
            skLineSegment(sketch, "E1251", {"start": v(-17.21, 0.66) * mm, "end": v(-17.26, 0.46) * mm});
            skLineSegment(sketch, "E1252", {"start": v(-17.26, 0.46) * mm, "end": v(-17.31, 0.25) * mm});
            skLineSegment(sketch, "E1253", {"start": v(-17.31, 0.25) * mm, "end": v(-17.36, 0.03) * mm});
            skLineSegment(sketch, "E1254", {"start": v(-17.36, 0.03) * mm, "end": v(-17.4, -0.2) * mm});
            skLineSegment(sketch, "E1255", {"start": v(-17.4, -0.2) * mm, "end": v(-17.45, -0.45) * mm});
            skLineSegment(sketch, "E1256", {"start": v(-17.45, -0.45) * mm, "end": v(-17.49, -0.7) * mm});
            skLineSegment(sketch, "E1257", {"start": v(-17.49, -0.7) * mm, "end": v(-17.53, -0.97) * mm});
            skLineSegment(sketch, "E1258", {"start": v(-17.53, -0.97) * mm, "end": v(-17.56, -1.24) * mm});
            skLineSegment(sketch, "E1259", {"start": v(-17.56, -1.24) * mm, "end": v(-17.59, -1.53) * mm});
            skLineSegment(sketch, "E1260", {"start": v(-17.59, -1.53) * mm, "end": v(-17.6, -1.83) * mm});
            skLineSegment(sketch, "E1261", {"start": v(-17.6, -1.83) * mm, "end": v(-17.63, -2.14) * mm});
            skLineSegment(sketch, "E1262", {"start": v(-17.63, -2.14) * mm, "end": v(-17.64, -2.46) * mm});
            skLineSegment(sketch, "E1263", {"start": v(-17.64, -2.46) * mm, "end": v(-17.65, -2.8) * mm});
            skLineSegment(sketch, "E1264", {"start": v(-17.65, -2.8) * mm, "end": v(-17.59, -3.04) * mm});
            skLineSegment(sketch, "E1265", {"start": v(-17.59, -3.04) * mm, "end": v(-15.86, -4.05) * mm});
            skLineSegment(sketch, "E1266", {"start": v(-15.86, -4.05) * mm, "end": v(-15.61, -3.98) * mm});
            skLineSegment(sketch, "E1267", {"start": v(-15.61, -3.98) * mm, "end": v(-15.33, -3.8) * mm});
            skLineSegment(sketch, "E1268", {"start": v(-15.33, -3.8) * mm, "end": v(-15.05, -3.64) * mm});
            skLineSegment(sketch, "E1269", {"start": v(-15.05, -3.64) * mm, "end": v(-14.8, -3.47) * mm});
            skLineSegment(sketch, "E1270", {"start": v(-14.8, -3.47) * mm, "end": v(-14.54, -3.3) * mm});
            skLineSegment(sketch, "E1271", {"start": v(-14.54, -3.3) * mm, "end": v(-14.3, -3.14) * mm});
            skLineSegment(sketch, "E1272", {"start": v(-14.3, -3.14) * mm, "end": v(-14.08, -2.97) * mm});
            skLineSegment(sketch, "E1273", {"start": v(-14.08, -2.97) * mm, "end": v(-13.87, -2.81) * mm});
            skLineSegment(sketch, "E1274", {"start": v(-13.87, -2.81) * mm, "end": v(-13.67, -2.65) * mm});
            skLineSegment(sketch, "E1275", {"start": v(-13.67, -2.65) * mm, "end": v(-13.47, -2.5) * mm});
            skLineSegment(sketch, "E1276", {"start": v(-13.47, -2.5) * mm, "end": v(-13.3, -2.34) * mm});
            skLineSegment(sketch, "E1277", {"start": v(-13.3, -2.34) * mm, "end": v(-13.13, -2.2) * mm});
            skLineSegment(sketch, "E1278", {"start": v(-13.13, -2.2) * mm, "end": v(-12.97, -2.04) * mm});
            skLineSegment(sketch, "E1279", {"start": v(-12.97, -2.04) * mm, "end": v(-12.82, -1.9) * mm});
            skLineSegment(sketch, "E1280", {"start": v(-12.82, -1.9) * mm, "end": v(-12.68, -1.76) * mm});
            skLineSegment(sketch, "E1281", {"start": v(-12.68, -1.76) * mm, "end": v(-12.56, -1.63) * mm});
            skLineSegment(sketch, "E1282", {"start": v(-12.56, -1.63) * mm, "end": v(-12.44, -1.5) * mm});
            skLineSegment(sketch, "E1283", {"start": v(-12.44, -1.5) * mm, "end": v(-12.33, -1.38) * mm});
            skLineSegment(sketch, "E1284", {"start": v(-12.33, -1.38) * mm, "end": v(-12.23, -1.27) * mm});
            skLineSegment(sketch, "E1285", {"start": v(-12.23, -1.27) * mm, "end": v(-12.14, -1.16) * mm});
            skLineSegment(sketch, "E1286", {"start": v(-12.14, -1.16) * mm, "end": v(-12.06, -1.06) * mm});
            skLineSegment(sketch, "E1287", {"start": v(-12.06, -1.06) * mm, "end": v(-11.99, -0.96) * mm});
            skLineSegment(sketch, "E1288", {"start": v(-11.99, -0.96) * mm, "end": v(-11.92, -0.87) * mm});
            skLineSegment(sketch, "E1289", {"start": v(-11.92, -0.87) * mm, "end": v(-11.87, -0.79) * mm});
            skLineSegment(sketch, "E1290", {"start": v(-11.87, -0.79) * mm, "end": v(-11.82, -0.72) * mm});
            skLineSegment(sketch, "E1291", {"start": v(-11.82, -0.72) * mm, "end": v(-11.77, -0.65) * mm});
            skLineSegment(sketch, "E1292", {"start": v(-11.77, -0.65) * mm, "end": v(-11.74, -0.6) * mm});
            skLineSegment(sketch, "E1293", {"start": v(-11.74, -0.6) * mm, "end": v(-11.71, -0.54) * mm});
            skLineSegment(sketch, "E1294", {"start": v(-11.71, -0.54) * mm, "end": v(-11.69, -0.5) * mm});
            skLineSegment(sketch, "E1295", {"start": v(-11.69, -0.5) * mm, "end": v(-11.67, -0.47) * mm});
            skLineSegment(sketch, "E1296", {"start": v(-11.67, -0.47) * mm, "end": v(-11.66, -0.45) * mm});
            skLineSegment(sketch, "E1297", {"start": v(-11.66, -0.45) * mm, "end": v(-11.65, -0.44) * mm});
            skLineSegment(sketch, "E1298", {"start": v(-11.65, -0.44) * mm, "end": v(-10.81, 1.4) * mm});
            skLineSegment(sketch, "E1299", {"start": v(-10.81, 1.4) * mm, "end": v(-7.19, 0.06) * mm});
            skLineSegment(sketch, "E1300", {"start": v(-7.19, 0.06) * mm, "end": v(-7.74, -1.88) * mm});
            skLineSegment(sketch, "E1301", {"start": v(-7.74, -1.88) * mm, "end": v(-7.75, -1.9) * mm});
            skLineSegment(sketch, "E1302", {"start": v(-7.75, -1.9) * mm, "end": v(-7.75, -1.92) * mm});
            skLineSegment(sketch, "E1303", {"start": v(-7.75, -1.92) * mm, "end": v(-7.76, -1.95) * mm});
            skLineSegment(sketch, "E1304", {"start": v(-7.76, -1.95) * mm, "end": v(-7.77, -2) * mm});
            skLineSegment(sketch, "E1305", {"start": v(-7.77, -2) * mm, "end": v(-7.78, -2.05) * mm});
            skLineSegment(sketch, "E1306", {"start": v(-7.78, -2.05) * mm, "end": v(-7.79, -2.12) * mm});
            skLineSegment(sketch, "E1307", {"start": v(-7.79, -2.12) * mm, "end": v(-7.8, -2.2) * mm});
            skLineSegment(sketch, "E1308", {"start": v(-7.8, -2.2) * mm, "end": v(-7.8, -2.29) * mm});
            skLineSegment(sketch, "E1309", {"start": v(-7.8, -2.29) * mm, "end": v(-7.82, -2.38) * mm});
            skLineSegment(sketch, "E1310", {"start": v(-7.82, -2.38) * mm, "end": v(-7.83, -2.5) * mm});
            skLineSegment(sketch, "E1311", {"start": v(-7.83, -2.5) * mm, "end": v(-7.83, -2.61) * mm});
            skLineSegment(sketch, "E1312", {"start": v(-7.83, -2.61) * mm, "end": v(-7.84, -2.75) * mm});
            skLineSegment(sketch, "E1313", {"start": v(-7.84, -2.75) * mm, "end": v(-7.84, -2.89) * mm});
            skLineSegment(sketch, "E1314", {"start": v(-7.84, -2.89) * mm, "end": v(-7.84, -3.04) * mm});
            skLineSegment(sketch, "E1315", {"start": v(-7.84, -3.04) * mm, "end": v(-7.84, -3.2) * mm});
            skLineSegment(sketch, "E1316", {"start": v(-7.84, -3.2) * mm, "end": v(-7.83, -3.37) * mm});
            skLineSegment(sketch, "E1317", {"start": v(-7.83, -3.37) * mm, "end": v(-7.82, -3.56) * mm});
            skLineSegment(sketch, "E1318", {"start": v(-7.82, -3.56) * mm, "end": v(-7.8, -3.75) * mm});
            skLineSegment(sketch, "E1319", {"start": v(-7.8, -3.75) * mm, "end": v(-7.79, -3.96) * mm});
            skLineSegment(sketch, "E1320", {"start": v(-7.79, -3.96) * mm, "end": v(-7.76, -4.17) * mm});
            skLineSegment(sketch, "E1321", {"start": v(-7.76, -4.17) * mm, "end": v(-7.73, -4.4) * mm});
            skLineSegment(sketch, "E1322", {"start": v(-7.73, -4.4) * mm, "end": v(-7.7, -4.63) * mm});
            skLineSegment(sketch, "E1323", {"start": v(-7.7, -4.63) * mm, "end": v(-7.65, -4.87) * mm});
            skLineSegment(sketch, "E1324", {"start": v(-7.65, -4.87) * mm, "end": v(-7.6, -5.12) * mm});
            skLineSegment(sketch, "E1325", {"start": v(-7.6, -5.12) * mm, "end": v(-7.55, -5.39) * mm});
            skLineSegment(sketch, "E1326", {"start": v(-7.55, -5.39) * mm, "end": v(-7.48, -5.66) * mm});
            skLineSegment(sketch, "E1327", {"start": v(-7.48, -5.66) * mm, "end": v(-7.4, -5.94) * mm});
            skLineSegment(sketch, "E1328", {"start": v(-7.4, -5.94) * mm, "end": v(-7.33, -6.23) * mm});
            skLineSegment(sketch, "E1329", {"start": v(-7.33, -6.23) * mm, "end": v(-7.24, -6.52) * mm});
            skLineSegment(sketch, "E1330", {"start": v(-7.24, -6.52) * mm, "end": v(-7.14, -6.83) * mm});
            skLineSegment(sketch, "E1331", {"start": v(-7.14, -6.83) * mm, "end": v(-7.03, -7.14) * mm});
            skLineSegment(sketch, "E1332", {"start": v(-7.03, -7.14) * mm, "end": v(-6.9, -7.36) * mm});
            skLineSegment(sketch, "E1333", {"start": v(-6.9, -7.36) * mm, "end": v(-4.92, -7.72) * mm});
            skLineSegment(sketch, "E1334", {"start": v(-4.92, -7.72) * mm, "end": v(-4.72, -7.56) * mm});
            skLineSegment(sketch, "E1335", {"start": v(-4.72, -7.56) * mm, "end": v(-4.5, -7.3) * mm});
            skLineSegment(sketch, "E1336", {"start": v(-4.5, -7.3) * mm, "end": v(-4.3, -7.05) * mm});
            skLineSegment(sketch, "E1337", {"start": v(-4.3, -7.05) * mm, "end": v(-4.12, -6.8) * mm});
            skLineSegment(sketch, "E1338", {"start": v(-4.12, -6.8) * mm, "end": v(-3.94, -6.56) * mm});
            skLineSegment(sketch, "E1339", {"start": v(-3.94, -6.56) * mm, "end": v(-3.78, -6.33) * mm});
            skLineSegment(sketch, "E1340", {"start": v(-3.78, -6.33) * mm, "end": v(-3.62, -6.1) * mm});
            skLineSegment(sketch, "E1341", {"start": v(-3.62, -6.1) * mm, "end": v(-3.48, -5.87) * mm});
            skLineSegment(sketch, "E1342", {"start": v(-3.48, -5.87) * mm, "end": v(-3.34, -5.65) * mm});
            skLineSegment(sketch, "E1343", {"start": v(-3.34, -5.65) * mm, "end": v(-3.22, -5.44) * mm});
            skLineSegment(sketch, "E1344", {"start": v(-3.22, -5.44) * mm, "end": v(-3.1, -5.23) * mm});
            skLineSegment(sketch, "E1345", {"start": v(-3.1, -5.23) * mm, "end": v(-3, -5.03) * mm});
            skLineSegment(sketch, "E1346", {"start": v(-3, -5.03) * mm, "end": v(-2.9, -4.84) * mm});
            skLineSegment(sketch, "E1347", {"start": v(-2.9, -4.84) * mm, "end": v(-2.8, -4.66) * mm});
            skLineSegment(sketch, "E1348", {"start": v(-2.8, -4.66) * mm, "end": v(-2.72, -4.48) * mm});
            skLineSegment(sketch, "E1349", {"start": v(-2.72, -4.48) * mm, "end": v(-2.65, -4.31) * mm});
            skLineSegment(sketch, "E1350", {"start": v(-2.65, -4.31) * mm, "end": v(-2.58, -4.15) * mm});
            skLineSegment(sketch, "E1351", {"start": v(-2.58, -4.15) * mm, "end": v(-2.52, -4) * mm});
            skLineSegment(sketch, "E1352", {"start": v(-2.52, -4) * mm, "end": v(-2.47, -3.86) * mm});
            skLineSegment(sketch, "E1353", {"start": v(-2.47, -3.86) * mm, "end": v(-2.42, -3.73) * mm});
            skLineSegment(sketch, "E1354", {"start": v(-2.42, -3.73) * mm, "end": v(-2.38, -3.6) * mm});
            skLineSegment(sketch, "E1355", {"start": v(-2.38, -3.6) * mm, "end": v(-2.34, -3.49) * mm});
            skLineSegment(sketch, "E1356", {"start": v(-2.34, -3.49) * mm, "end": v(-2.31, -3.38) * mm});
            skLineSegment(sketch, "E1357", {"start": v(-2.31, -3.38) * mm, "end": v(-2.29, -3.28) * mm});
            skLineSegment(sketch, "E1358", {"start": v(-2.29, -3.28) * mm, "end": v(-2.27, -3.2) * mm});
            skLineSegment(sketch, "E1359", {"start": v(-2.27, -3.2) * mm, "end": v(-2.25, -3.12) * mm});
            skLineSegment(sketch, "E1360", {"start": v(-2.25, -3.12) * mm, "end": v(-2.24, -3.06) * mm});
            skLineSegment(sketch, "E1361", {"start": v(-2.24, -3.06) * mm, "end": v(-2.23, -3) * mm});
            skLineSegment(sketch, "E1362", {"start": v(-2.23, -3) * mm, "end": v(-2.22, -2.95) * mm});
            skLineSegment(sketch, "E1363", {"start": v(-2.22, -2.95) * mm, "end": v(-2.21, -2.92) * mm});
            skLineSegment(sketch, "E1364", {"start": v(-2.21, -2.92) * mm, "end": v(-2.2, -2.9) * mm});
            skLineSegment(sketch, "E1365", {"start": v(-2.2, -2.9) * mm, "end": v(-2.2, -2.88) * mm});
            skLineSegment(sketch, "E1366", {"start": v(-2.2, -2.88) * mm, "end": v(-2.05, -0.86) * mm});
            skLineSegment(sketch, "E1367", {"start": v(-2.05, -0.86) * mm, "end": v(1.82, -0.88) * mm});
            skLineSegment(sketch, "E1368", {"start": v(1.82, -0.88) * mm, "end": v(1.96, -2.9) * mm});
            skLineSegment(sketch, "E1369", {"start": v(1.96, -2.9) * mm, "end": v(1.96, -2.91) * mm});
            skLineSegment(sketch, "E1370", {"start": v(1.96, -2.91) * mm, "end": v(1.96, -2.94) * mm});
            skLineSegment(sketch, "E1371", {"start": v(1.96, -2.94) * mm, "end": v(1.97, -2.97) * mm});
            skLineSegment(sketch, "E1372", {"start": v(1.97, -2.97) * mm, "end": v(1.98, -3.02) * mm});
            skLineSegment(sketch, "E1373", {"start": v(1.98, -3.02) * mm, "end": v(1.99, -3.08) * mm});
            skLineSegment(sketch, "E1374", {"start": v(1.99, -3.08) * mm, "end": v(2, -3.14) * mm});
            skLineSegment(sketch, "E1375", {"start": v(2, -3.14) * mm, "end": v(2.02, -3.22) * mm});
            skLineSegment(sketch, "E1376", {"start": v(2.02, -3.22) * mm, "end": v(2.04, -3.3) * mm});
            skLineSegment(sketch, "E1377", {"start": v(2.04, -3.3) * mm, "end": v(2.06, -3.4) * mm});
            skLineSegment(sketch, "E1378", {"start": v(2.06, -3.4) * mm, "end": v(2.1, -3.5) * mm});
            skLineSegment(sketch, "E1379", {"start": v(2.1, -3.5) * mm, "end": v(2.12, -3.62) * mm});
            skLineSegment(sketch, "E1380", {"start": v(2.12, -3.62) * mm, "end": v(2.16, -3.75) * mm});
            skLineSegment(sketch, "E1381", {"start": v(2.16, -3.75) * mm, "end": v(2.21, -3.88) * mm});
            skLineSegment(sketch, "E1382", {"start": v(2.21, -3.88) * mm, "end": v(2.26, -4.02) * mm});
            skLineSegment(sketch, "E1383", {"start": v(2.26, -4.02) * mm, "end": v(2.32, -4.17) * mm});
            skLineSegment(sketch, "E1384", {"start": v(2.32, -4.17) * mm, "end": v(2.39, -4.34) * mm});
            skLineSegment(sketch, "E1385", {"start": v(2.39, -4.34) * mm, "end": v(2.46, -4.5) * mm});
            skLineSegment(sketch, "E1386", {"start": v(2.46, -4.5) * mm, "end": v(2.54, -4.68) * mm});
            skLineSegment(sketch, "E1387", {"start": v(2.54, -4.68) * mm, "end": v(2.63, -4.87) * mm});
            skLineSegment(sketch, "E1388", {"start": v(2.63, -4.87) * mm, "end": v(2.73, -5.06) * mm});
            skLineSegment(sketch, "E1389", {"start": v(2.73, -5.06) * mm, "end": v(2.83, -5.26) * mm});
            skLineSegment(sketch, "E1390", {"start": v(2.83, -5.26) * mm, "end": v(2.94, -5.47) * mm});
            skLineSegment(sketch, "E1391", {"start": v(2.94, -5.47) * mm, "end": v(3.07, -5.68) * mm});
            skLineSegment(sketch, "E1392", {"start": v(3.07, -5.68) * mm, "end": v(3.2, -5.9) * mm});
            skLineSegment(sketch, "E1393", {"start": v(3.2, -5.9) * mm, "end": v(3.34, -6.13) * mm});
            skLineSegment(sketch, "E1394", {"start": v(3.34, -6.13) * mm, "end": v(3.5, -6.36) * mm});
            skLineSegment(sketch, "E1395", {"start": v(3.5, -6.36) * mm, "end": v(3.66, -6.6) * mm});
            skLineSegment(sketch, "E1396", {"start": v(3.66, -6.6) * mm, "end": v(3.84, -6.84) * mm});
            skLineSegment(sketch, "E1397", {"start": v(3.84, -6.84) * mm, "end": v(4.02, -7.1) * mm});
            skLineSegment(sketch, "E1398", {"start": v(4.02, -7.1) * mm, "end": v(4.22, -7.35) * mm});
            skLineSegment(sketch, "E1399", {"start": v(4.22, -7.35) * mm, "end": v(4.43, -7.6) * mm});
            skLineSegment(sketch, "E1400", {"start": v(4.43, -7.6) * mm, "end": v(4.63, -7.76) * mm});
            skLineSegment(sketch, "E1401", {"start": v(4.63, -7.76) * mm, "end": v(6.6, -7.42) * mm});
            skLineSegment(sketch, "E1402", {"start": v(6.6, -7.42) * mm, "end": v(6.75, -7.2) * mm});
            skLineSegment(sketch, "E1403", {"start": v(6.75, -7.2) * mm, "end": v(6.86, -6.9) * mm});
            skLineSegment(sketch, "E1404", {"start": v(6.86, -6.9) * mm, "end": v(6.96, -6.59) * mm});
            skLineSegment(sketch, "E1405", {"start": v(6.96, -6.59) * mm, "end": v(7.05, -6.3) * mm});
            skLineSegment(sketch, "E1406", {"start": v(7.05, -6.3) * mm, "end": v(7.13, -6) * mm});
            skLineSegment(sketch, "E1407", {"start": v(7.13, -6) * mm, "end": v(7.2, -5.72) * mm});
            skLineSegment(sketch, "E1408", {"start": v(7.2, -5.72) * mm, "end": v(7.27, -5.45) * mm});
            skLineSegment(sketch, "E1409", {"start": v(7.27, -5.45) * mm, "end": v(7.33, -5.2) * mm});
            skLineSegment(sketch, "E1410", {"start": v(7.33, -5.2) * mm, "end": v(7.39, -4.94) * mm});
            skLineSegment(sketch, "E1411", {"start": v(7.39, -4.94) * mm, "end": v(7.43, -4.7) * mm});
            skLineSegment(sketch, "E1412", {"start": v(7.43, -4.7) * mm, "end": v(7.47, -4.46) * mm});
            skLineSegment(sketch, "E1413", {"start": v(7.47, -4.46) * mm, "end": v(7.5, -4.24) * mm});
            skLineSegment(sketch, "E1414", {"start": v(7.5, -4.24) * mm, "end": v(7.53, -4.02) * mm});
            skLineSegment(sketch, "E1415", {"start": v(7.53, -4.02) * mm, "end": v(7.55, -3.82) * mm});
            skLineSegment(sketch, "E1416", {"start": v(7.55, -3.82) * mm, "end": v(7.57, -3.63) * mm});
            skLineSegment(sketch, "E1417", {"start": v(7.57, -3.63) * mm, "end": v(7.58, -3.44) * mm});
            skLineSegment(sketch, "E1418", {"start": v(7.58, -3.44) * mm, "end": v(7.59, -3.27) * mm});
            skLineSegment(sketch, "E1419", {"start": v(7.59, -3.27) * mm, "end": v(7.6, -3.1) * mm});
            skLineSegment(sketch, "E1420", {"start": v(7.6, -3.1) * mm, "end": v(7.6, -2.96) * mm});
            skLineSegment(sketch, "E1421", {"start": v(7.6, -2.96) * mm, "end": v(7.6, -2.81) * mm});
            skLineSegment(sketch, "E1422", {"start": v(7.6, -2.81) * mm, "end": v(7.59, -2.68) * mm});
            skLineSegment(sketch, "E1423", {"start": v(7.59, -2.68) * mm, "end": v(7.58, -2.56) * mm});
            skLineSegment(sketch, "E1424", {"start": v(7.58, -2.56) * mm, "end": v(7.57, -2.45) * mm});
            skLineSegment(sketch, "E1425", {"start": v(7.57, -2.45) * mm, "end": v(7.57, -2.35) * mm});
            skLineSegment(sketch, "E1426", {"start": v(7.57, -2.35) * mm, "end": v(7.56, -2.27) * mm});
            skLineSegment(sketch, "E1427", {"start": v(7.56, -2.27) * mm, "end": v(7.55, -2.19) * mm});
            skLineSegment(sketch, "E1428", {"start": v(7.55, -2.19) * mm, "end": v(7.54, -2.12) * mm});
            skLineSegment(sketch, "E1429", {"start": v(7.54, -2.12) * mm, "end": v(7.53, -2.07) * mm});
            skLineSegment(sketch, "E1430", {"start": v(7.53, -2.07) * mm, "end": v(7.52, -2.02) * mm});
            skLineSegment(sketch, "E1431", {"start": v(7.52, -2.02) * mm, "end": v(7.51, -1.98) * mm});
            skLineSegment(sketch, "E1432", {"start": v(7.51, -1.98) * mm, "end": v(7.5, -1.96) * mm});
            skLineSegment(sketch, "E1433", {"start": v(7.5, -1.96) * mm, "end": v(7.5, -1.95) * mm});
            skLineSegment(sketch, "E1434", {"start": v(7.5, -1.95) * mm, "end": v(6.96, 0) * mm});
            skLineSegment(sketch, "E1435", {"start": v(6.96, 0) * mm, "end": v(10.6, 1.3) * mm});
            skLineSegment(sketch, "E1436", {"start": v(10.6, 1.3) * mm, "end": v(11.43, -0.54) * mm});
            skLineSegment(sketch, "E1437", {"start": v(11.43, -0.54) * mm, "end": v(11.43, -0.55) * mm});
            skLineSegment(sketch, "E1438", {"start": v(11.43, -0.55) * mm, "end": v(11.44, -0.57) * mm});
            skLineSegment(sketch, "E1439", {"start": v(11.44, -0.57) * mm, "end": v(11.46, -0.6) * mm});
            skLineSegment(sketch, "E1440", {"start": v(11.46, -0.6) * mm, "end": v(11.48, -0.65) * mm});
            skLineSegment(sketch, "E1441", {"start": v(11.48, -0.65) * mm, "end": v(11.51, -0.7) * mm});
            skLineSegment(sketch, "E1442", {"start": v(11.51, -0.7) * mm, "end": v(11.55, -0.75) * mm});
            skLineSegment(sketch, "E1443", {"start": v(11.55, -0.75) * mm, "end": v(11.59, -0.82) * mm});
            skLineSegment(sketch, "E1444", {"start": v(11.59, -0.82) * mm, "end": v(11.64, -0.9) * mm});
            skLineSegment(sketch, "E1445", {"start": v(11.64, -0.9) * mm, "end": v(11.7, -0.98) * mm});
            skLineSegment(sketch, "E1446", {"start": v(11.7, -0.98) * mm, "end": v(11.76, -1.06) * mm});
            skLineSegment(sketch, "E1447", {"start": v(11.76, -1.06) * mm, "end": v(11.83, -1.16) * mm});
            skLineSegment(sketch, "E1448", {"start": v(11.83, -1.16) * mm, "end": v(11.9, -1.26) * mm});
            skLineSegment(sketch, "E1449", {"start": v(11.9, -1.26) * mm, "end": v(12, -1.37) * mm});
            skLineSegment(sketch, "E1450", {"start": v(12, -1.37) * mm, "end": v(12.1, -1.5) * mm});
            skLineSegment(sketch, "E1451", {"start": v(12.1, -1.5) * mm, "end": v(12.2, -1.61) * mm});
            skLineSegment(sketch, "E1452", {"start": v(12.2, -1.61) * mm, "end": v(12.32, -1.74) * mm});
            skLineSegment(sketch, "E1453", {"start": v(12.32, -1.74) * mm, "end": v(12.44, -1.88) * mm});
            skLineSegment(sketch, "E1454", {"start": v(12.44, -1.88) * mm, "end": v(12.58, -2.01) * mm});
            skLineSegment(sketch, "E1455", {"start": v(12.58, -2.01) * mm, "end": v(12.73, -2.16) * mm});
            skLineSegment(sketch, "E1456", {"start": v(12.73, -2.16) * mm, "end": v(12.88, -2.3) * mm});
            skLineSegment(sketch, "E1457", {"start": v(12.88, -2.3) * mm, "end": v(13.05, -2.46) * mm});
            skLineSegment(sketch, "E1458", {"start": v(13.05, -2.46) * mm, "end": v(13.23, -2.61) * mm});
            skLineSegment(sketch, "E1459", {"start": v(13.23, -2.61) * mm, "end": v(13.42, -2.77) * mm});
            skLineSegment(sketch, "E1460", {"start": v(13.42, -2.77) * mm, "end": v(13.62, -2.93) * mm});
            skLineSegment(sketch, "E1461", {"start": v(13.62, -2.93) * mm, "end": v(13.83, -3.1) * mm});
            skLineSegment(sketch, "E1462", {"start": v(13.83, -3.1) * mm, "end": v(14.05, -3.26) * mm});
            skLineSegment(sketch, "E1463", {"start": v(14.05, -3.26) * mm, "end": v(14.3, -3.43) * mm});
            skLineSegment(sketch, "E1464", {"start": v(14.3, -3.43) * mm, "end": v(14.54, -3.6) * mm});
            skLineSegment(sketch, "E1465", {"start": v(14.54, -3.6) * mm, "end": v(14.8, -3.77) * mm});
            skLineSegment(sketch, "E1466", {"start": v(14.8, -3.77) * mm, "end": v(15.07, -3.94) * mm});
            skLineSegment(sketch, "E1467", {"start": v(15.07, -3.94) * mm, "end": v(15.35, -4.12) * mm});
            skLineSegment(sketch, "E1468", {"start": v(15.35, -4.12) * mm, "end": v(15.6, -4.2) * mm});
            skLineSegment(sketch, "E1469", {"start": v(15.6, -4.2) * mm, "end": v(17.34, -3.2) * mm});
            skLineSegment(sketch, "E1470", {"start": v(17.34, -3.2) * mm, "end": v(17.4, -2.95) * mm});
            skLineSegment(sketch, "E1471", {"start": v(17.4, -2.95) * mm, "end": v(17.4, -2.62) * mm});
            skLineSegment(sketch, "E1472", {"start": v(17.4, -2.62) * mm, "end": v(17.38, -2.3) * mm});
            skLineSegment(sketch, "E1473", {"start": v(17.38, -2.3) * mm, "end": v(17.37, -1.98) * mm});
            skLineSegment(sketch, "E1474", {"start": v(17.37, -1.98) * mm, "end": v(17.35, -1.69) * mm});
            skLineSegment(sketch, "E1475", {"start": v(17.35, -1.69) * mm, "end": v(17.32, -1.4) * mm});
            skLineSegment(sketch, "E1476", {"start": v(17.32, -1.4) * mm, "end": v(17.3, -1.12) * mm});
            skLineSegment(sketch, "E1477", {"start": v(17.3, -1.12) * mm, "end": v(17.26, -0.85) * mm});
            skLineSegment(sketch, "E1478", {"start": v(17.26, -0.85) * mm, "end": v(17.22, -0.6) * mm});
            skLineSegment(sketch, "E1479", {"start": v(17.22, -0.6) * mm, "end": v(17.18, -0.36) * mm});
            skLineSegment(sketch, "E1480", {"start": v(17.18, -0.36) * mm, "end": v(17.14, -0.12) * mm});
            skLineSegment(sketch, "E1481", {"start": v(17.14, -0.12) * mm, "end": v(17.1, 0.1) * mm});
            skLineSegment(sketch, "E1482", {"start": v(17.1, 0.1) * mm, "end": v(17.04, 0.3) * mm});
            skLineSegment(sketch, "E1483", {"start": v(17.04, 0.3) * mm, "end": v(17, 0.5) * mm});
            skLineSegment(sketch, "E1484", {"start": v(17, 0.5) * mm, "end": v(16.94, 0.7) * mm});
            skLineSegment(sketch, "E1485", {"start": v(16.94, 0.7) * mm, "end": v(16.9, 0.87) * mm});
            skLineSegment(sketch, "E1486", {"start": v(16.9, 0.87) * mm, "end": v(16.84, 1.04) * mm});
            skLineSegment(sketch, "E1487", {"start": v(16.84, 1.04) * mm, "end": v(16.79, 1.2) * mm});
            skLineSegment(sketch, "E1488", {"start": v(16.79, 1.2) * mm, "end": v(16.74, 1.33) * mm});
            skLineSegment(sketch, "E1489", {"start": v(16.74, 1.33) * mm, "end": v(16.69, 1.47) * mm});
            skLineSegment(sketch, "E1490", {"start": v(16.69, 1.47) * mm, "end": v(16.64, 1.59) * mm});
            skLineSegment(sketch, "E1491", {"start": v(16.64, 1.59) * mm, "end": v(16.6, 1.7) * mm});
            skLineSegment(sketch, "E1492", {"start": v(16.6, 1.7) * mm, "end": v(16.55, 1.8) * mm});
            skLineSegment(sketch, "E1493", {"start": v(16.55, 1.8) * mm, "end": v(16.5, 1.9) * mm});
            skLineSegment(sketch, "E1494", {"start": v(16.5, 1.9) * mm, "end": v(16.47, 1.97) * mm});
            skLineSegment(sketch, "E1495", {"start": v(16.47, 1.97) * mm, "end": v(16.43, 2.04) * mm});
            skLineSegment(sketch, "E1496", {"start": v(16.43, 2.04) * mm, "end": v(16.4, 2.1) * mm});
            skLineSegment(sketch, "E1497", {"start": v(16.4, 2.1) * mm, "end": v(16.37, 2.15) * mm});
            skLineSegment(sketch, "E1498", {"start": v(16.37, 2.15) * mm, "end": v(16.35, 2.19) * mm});
            skLineSegment(sketch, "E1499", {"start": v(16.35, 2.19) * mm, "end": v(16.33, 2.22) * mm});
            skLineSegment(sketch, "E1500", {"start": v(16.33, 2.22) * mm, "end": v(16.32, 2.24) * mm});
            skLineSegment(sketch, "E1501", {"start": v(16.32, 2.24) * mm, "end": v(16.3, 2.25) * mm});
            skLineSegment(sketch, "E1502", {"start": v(16.3, 2.25) * mm, "end": v(15.13, 3.9) * mm});
            skLineSegment(sketch, "E1503", {"start": v(15.13, 3.9) * mm, "end": v(18.1, 6.37) * mm});
            skLineSegment(sketch, "E1504", {"start": v(18.1, 6.37) * mm, "end": v(19.51, 4.92) * mm});
            skLineSegment(sketch, "E1505", {"start": v(19.51, 4.92) * mm, "end": v(19.52, 4.9) * mm});
            skLineSegment(sketch, "E1506", {"start": v(19.52, 4.9) * mm, "end": v(19.54, 4.89) * mm});
            skLineSegment(sketch, "E1507", {"start": v(19.54, 4.89) * mm, "end": v(19.57, 4.87) * mm});
            skLineSegment(sketch, "E1508", {"start": v(19.57, 4.87) * mm, "end": v(19.6, 4.84) * mm});
            skLineSegment(sketch, "E1509", {"start": v(19.6, 4.84) * mm, "end": v(19.65, 4.8) * mm});
            skLineSegment(sketch, "E1510", {"start": v(19.65, 4.8) * mm, "end": v(19.7, 4.76) * mm});
            skLineSegment(sketch, "E1511", {"start": v(19.7, 4.76) * mm, "end": v(19.76, 4.7) * mm});
            skLineSegment(sketch, "E1512", {"start": v(19.76, 4.7) * mm, "end": v(19.83, 4.66) * mm});
            skLineSegment(sketch, "E1513", {"start": v(19.83, 4.66) * mm, "end": v(19.91, 4.6) * mm});
            skLineSegment(sketch, "E1514", {"start": v(19.91, 4.6) * mm, "end": v(20, 4.54) * mm});
            skLineSegment(sketch, "E1515", {"start": v(20, 4.54) * mm, "end": v(20.1, 4.47) * mm});
            skLineSegment(sketch, "E1516", {"start": v(20.1, 4.47) * mm, "end": v(20.22, 4.4) * mm});
            skLineSegment(sketch, "E1517", {"start": v(20.22, 4.4) * mm, "end": v(20.34, 4.33) * mm});
            skLineSegment(sketch, "E1518", {"start": v(20.34, 4.33) * mm, "end": v(20.47, 4.25) * mm});
            skLineSegment(sketch, "E1519", {"start": v(20.47, 4.25) * mm, "end": v(20.61, 4.17) * mm});
            skLineSegment(sketch, "E1520", {"start": v(20.61, 4.17) * mm, "end": v(20.76, 4.1) * mm});
            skLineSegment(sketch, "E1521", {"start": v(20.76, 4.1) * mm, "end": v(20.93, 4) * mm});
            skLineSegment(sketch, "E1522", {"start": v(20.93, 4) * mm, "end": v(21.1, 3.92) * mm});
            skLineSegment(sketch, "E1523", {"start": v(21.1, 3.92) * mm, "end": v(21.29, 3.84) * mm});
            skLineSegment(sketch, "E1524", {"start": v(21.29, 3.84) * mm, "end": v(21.49, 3.75) * mm});
            skLineSegment(sketch, "E1525", {"start": v(21.49, 3.75) * mm, "end": v(21.7, 3.67) * mm});
            skLineSegment(sketch, "E1526", {"start": v(21.7, 3.67) * mm, "end": v(21.92, 3.58) * mm});
            skLineSegment(sketch, "E1527", {"start": v(21.92, 3.58) * mm, "end": v(22.15, 3.5) * mm});
            skLineSegment(sketch, "E1528", {"start": v(22.15, 3.5) * mm, "end": v(22.4, 3.42) * mm});
            skLineSegment(sketch, "E1529", {"start": v(22.4, 3.42) * mm, "end": v(22.65, 3.33) * mm});
            skLineSegment(sketch, "E1530", {"start": v(22.65, 3.33) * mm, "end": v(22.92, 3.25) * mm});
            skLineSegment(sketch, "E1531", {"start": v(22.92, 3.25) * mm, "end": v(23.2, 3.18) * mm});
            skLineSegment(sketch, "E1532", {"start": v(23.2, 3.18) * mm, "end": v(23.49, 3.1) * mm});
            skLineSegment(sketch, "E1533", {"start": v(23.49, 3.1) * mm, "end": v(23.79, 3.03) * mm});
            skLineSegment(sketch, "E1534", {"start": v(23.79, 3.03) * mm, "end": v(24.1, 2.96) * mm});
            skLineSegment(sketch, "E1535", {"start": v(24.1, 2.96) * mm, "end": v(24.43, 2.9) * mm});
            skLineSegment(sketch, "E1536", {"start": v(24.43, 2.9) * mm, "end": v(24.69, 2.9) * mm});
            skLineSegment(sketch, "E1537", {"start": v(24.69, 2.9) * mm, "end": v(25.98, 4.44) * mm});
            skLineSegment(sketch, "E1538", {"start": v(25.98, 4.44) * mm, "end": v(25.95, 4.7) * mm});
            skLineSegment(sketch, "E1539", {"start": v(25.95, 4.7) * mm, "end": v(25.83, 5) * mm});
            skLineSegment(sketch, "E1540", {"start": v(25.83, 5) * mm, "end": v(25.71, 5.3) * mm});
            skLineSegment(sketch, "E1541", {"start": v(25.71, 5.3) * mm, "end": v(25.6, 5.6) * mm});
            skLineSegment(sketch, "E1542", {"start": v(25.6, 5.6) * mm, "end": v(25.47, 5.86) * mm});
            skLineSegment(sketch, "E1543", {"start": v(25.47, 5.86) * mm, "end": v(25.35, 6.13) * mm});
            skLineSegment(sketch, "E1544", {"start": v(25.35, 6.13) * mm, "end": v(25.23, 6.38) * mm});
            skLineSegment(sketch, "E1545", {"start": v(25.23, 6.38) * mm, "end": v(25.1, 6.62) * mm});
            skLineSegment(sketch, "E1546", {"start": v(25.1, 6.62) * mm, "end": v(24.98, 6.84) * mm});
            skLineSegment(sketch, "E1547", {"start": v(24.98, 6.84) * mm, "end": v(24.86, 7.06) * mm});
            skLineSegment(sketch, "E1548", {"start": v(24.86, 7.06) * mm, "end": v(24.74, 7.26) * mm});
            skLineSegment(sketch, "E1549", {"start": v(24.74, 7.26) * mm, "end": v(24.62, 7.45) * mm});
            skLineSegment(sketch, "E1550", {"start": v(24.62, 7.45) * mm, "end": v(24.5, 7.63) * mm});
            skLineSegment(sketch, "E1551", {"start": v(24.5, 7.63) * mm, "end": v(24.39, 7.8) * mm});
            skLineSegment(sketch, "E1552", {"start": v(24.39, 7.8) * mm, "end": v(24.28, 7.96) * mm});
            skLineSegment(sketch, "E1553", {"start": v(24.28, 7.96) * mm, "end": v(24.17, 8.11) * mm});
            skLineSegment(sketch, "E1554", {"start": v(24.17, 8.11) * mm, "end": v(24.06, 8.25) * mm});
            skLineSegment(sketch, "E1555", {"start": v(24.06, 8.25) * mm, "end": v(23.96, 8.38) * mm});
            skLineSegment(sketch, "E1556", {"start": v(23.96, 8.38) * mm, "end": v(23.87, 8.5) * mm});
            skLineSegment(sketch, "E1557", {"start": v(23.87, 8.5) * mm, "end": v(23.77, 8.6) * mm});
            skLineSegment(sketch, "E1558", {"start": v(23.77, 8.6) * mm, "end": v(23.69, 8.7) * mm});
            skLineSegment(sketch, "E1559", {"start": v(23.69, 8.7) * mm, "end": v(23.6, 8.79) * mm});
            skLineSegment(sketch, "E1560", {"start": v(23.6, 8.79) * mm, "end": v(23.53, 8.87) * mm});
            skLineSegment(sketch, "E1561", {"start": v(23.53, 8.87) * mm, "end": v(23.46, 8.94) * mm});
            skLineSegment(sketch, "E1562", {"start": v(23.46, 8.94) * mm, "end": v(23.4, 9) * mm});
            skLineSegment(sketch, "E1563", {"start": v(23.4, 9) * mm, "end": v(23.34, 9.05) * mm});
            skLineSegment(sketch, "E1564", {"start": v(23.34, 9.05) * mm, "end": v(23.29, 9.1) * mm});
            skLineSegment(sketch, "E1565", {"start": v(23.29, 9.1) * mm, "end": v(23.24, 9.13) * mm});
            skLineSegment(sketch, "E1566", {"start": v(23.24, 9.13) * mm, "end": v(23.2, 9.16) * mm});
            skLineSegment(sketch, "E1567", {"start": v(23.2, 9.16) * mm, "end": v(23.18, 9.19) * mm});
            skLineSegment(sketch, "E1568", {"start": v(23.18, 9.19) * mm, "end": v(23.16, 9.2) * mm});
            skLineSegment(sketch, "E1569", {"start": v(23.16, 9.2) * mm, "end": v(23.15, 9.2) * mm});
            skLineSegment(sketch, "E1570", {"start": v(23.15, 9.2) * mm, "end": v(21.48, 10.35) * mm});
            skLineSegment(sketch, "E1571", {"start": v(21.48, 10.35) * mm, "end": v(23.43, 13.7) * mm});
            skLineSegment(sketch, "E1572", {"start": v(23.43, 13.7) * mm, "end": v(25.25, 12.8) * mm});
            skLineSegment(sketch, "E1573", {"start": v(25.25, 12.8) * mm, "end": v(25.26, 12.8) * mm});
            skLineSegment(sketch, "E1574", {"start": v(25.26, 12.8) * mm, "end": v(25.28, 12.8) * mm});
            skLineSegment(sketch, "E1575", {"start": v(25.28, 12.8) * mm, "end": v(25.32, 12.78) * mm});
            skLineSegment(sketch, "E1576", {"start": v(25.32, 12.78) * mm, "end": v(25.36, 12.76) * mm});
            skLineSegment(sketch, "E1577", {"start": v(25.36, 12.76) * mm, "end": v(25.41, 12.74) * mm});
            skLineSegment(sketch, "E1578", {"start": v(25.41, 12.74) * mm, "end": v(25.48, 12.72) * mm});
            skLineSegment(sketch, "E1579", {"start": v(25.48, 12.72) * mm, "end": v(25.55, 12.7) * mm});
            skLineSegment(sketch, "E1580", {"start": v(25.55, 12.7) * mm, "end": v(25.64, 12.67) * mm});
            skLineSegment(sketch, "E1581", {"start": v(25.64, 12.67) * mm, "end": v(25.73, 12.65) * mm});
            skLineSegment(sketch, "E1582", {"start": v(25.73, 12.65) * mm, "end": v(25.84, 12.62) * mm});
            skLineSegment(sketch, "E1583", {"start": v(25.84, 12.62) * mm, "end": v(25.96, 12.6) * mm});
            skLineSegment(sketch, "E1584", {"start": v(25.96, 12.6) * mm, "end": v(26.08, 12.56) * mm});
            skLineSegment(sketch, "E1585", {"start": v(26.08, 12.56) * mm, "end": v(26.22, 12.54) * mm});
            skLineSegment(sketch, "E1586", {"start": v(26.22, 12.54) * mm, "end": v(26.37, 12.5) * mm});
            skLineSegment(sketch, "E1587", {"start": v(26.37, 12.5) * mm, "end": v(26.53, 12.48) * mm});
            skLineSegment(sketch, "E1588", {"start": v(26.53, 12.48) * mm, "end": v(26.7, 12.46) * mm});
            skLineSegment(sketch, "E1589", {"start": v(26.7, 12.46) * mm, "end": v(26.89, 12.44) * mm});
            skLineSegment(sketch, "E1590", {"start": v(26.89, 12.44) * mm, "end": v(27.08, 12.42) * mm});
            skLineSegment(sketch, "E1591", {"start": v(27.08, 12.42) * mm, "end": v(27.29, 12.4) * mm});
            skLineSegment(sketch, "E1592", {"start": v(27.29, 12.4) * mm, "end": v(27.5, 12.4) * mm});
            skLineSegment(sketch, "E1593", {"start": v(27.5, 12.4) * mm, "end": v(27.73, 12.38) * mm});
            skLineSegment(sketch, "E1594", {"start": v(27.73, 12.38) * mm, "end": v(27.96, 12.38) * mm});
            skLineSegment(sketch, "E1595", {"start": v(27.96, 12.38) * mm, "end": v(28.2, 12.38) * mm});
            skLineSegment(sketch, "E1596", {"start": v(28.2, 12.38) * mm, "end": v(28.47, 12.38) * mm});
            skLineSegment(sketch, "E1597", {"start": v(28.47, 12.38) * mm, "end": v(28.74, 12.4) * mm});
            skLineSegment(sketch, "E1598", {"start": v(28.74, 12.4) * mm, "end": v(29.01, 12.41) * mm});
            skLineSegment(sketch, "E1599", {"start": v(29.01, 12.41) * mm, "end": v(29.3, 12.43) * mm});
            skLineSegment(sketch, "E1600", {"start": v(29.3, 12.43) * mm, "end": v(29.6, 12.46) * mm});
            skLineSegment(sketch, "E1601", {"start": v(29.6, 12.46) * mm, "end": v(29.9, 12.5) * mm});
            skLineSegment(sketch, "E1602", {"start": v(29.9, 12.5) * mm, "end": v(30.23, 12.54) * mm});
            skLineSegment(sketch, "E1603", {"start": v(30.23, 12.54) * mm, "end": v(30.56, 12.6) * mm});
            skLineSegment(sketch, "E1604", {"start": v(30.56, 12.6) * mm, "end": v(30.8, 12.7) * mm});
            skLineSegment(sketch, "E1605", {"start": v(30.8, 12.7) * mm, "end": v(31.49, 14.57) * mm});
            skLineSegment(sketch, "E1606", {"start": v(31.49, 14.57) * mm, "end": v(31.37, 14.8) * mm});
            skLineSegment(sketch, "E1607", {"start": v(31.37, 14.8) * mm, "end": v(31.15, 15.05) * mm});
            skLineSegment(sketch, "E1608", {"start": v(31.15, 15.05) * mm, "end": v(30.94, 15.3) * mm});
            skLineSegment(sketch, "E1609", {"start": v(30.94, 15.3) * mm, "end": v(30.73, 15.52) * mm});
            skLineSegment(sketch, "E1610", {"start": v(30.73, 15.52) * mm, "end": v(30.52, 15.74) * mm});
            skLineSegment(sketch, "E1611", {"start": v(30.52, 15.74) * mm, "end": v(30.32, 15.94) * mm});
            skLineSegment(sketch, "E1612", {"start": v(30.32, 15.94) * mm, "end": v(30.12, 16.14) * mm});
            skLineSegment(sketch, "E1613", {"start": v(30.12, 16.14) * mm, "end": v(29.92, 16.32) * mm});
            skLineSegment(sketch, "E1614", {"start": v(29.92, 16.32) * mm, "end": v(29.73, 16.49) * mm});
            skLineSegment(sketch, "E1615", {"start": v(29.73, 16.49) * mm, "end": v(29.54, 16.65) * mm});
            skLineSegment(sketch, "E1616", {"start": v(29.54, 16.65) * mm, "end": v(29.36, 16.8) * mm});
            skLineSegment(sketch, "E1617", {"start": v(29.36, 16.8) * mm, "end": v(29.18, 16.94) * mm});
            skLineSegment(sketch, "E1618", {"start": v(29.18, 16.94) * mm, "end": v(29, 17.07) * mm});
            skLineSegment(sketch, "E1619", {"start": v(29, 17.07) * mm, "end": v(28.84, 17.2) * mm});
            skLineSegment(sketch, "E1620", {"start": v(28.84, 17.2) * mm, "end": v(28.68, 17.3) * mm});
            skLineSegment(sketch, "E1621", {"start": v(28.68, 17.3) * mm, "end": v(28.53, 17.4) * mm});
            skLineSegment(sketch, "E1622", {"start": v(28.53, 17.4) * mm, "end": v(28.38, 17.5) * mm});
            skLineSegment(sketch, "E1623", {"start": v(28.38, 17.5) * mm, "end": v(28.24, 17.58) * mm});
            skLineSegment(sketch, "E1624", {"start": v(28.24, 17.58) * mm, "end": v(28.11, 17.66) * mm});
            skLineSegment(sketch, "E1625", {"start": v(28.11, 17.66) * mm, "end": v(28, 17.73) * mm});
            skLineSegment(sketch, "E1626", {"start": v(28, 17.73) * mm, "end": v(27.88, 17.8) * mm});
            skLineSegment(sketch, "E1627", {"start": v(27.88, 17.8) * mm, "end": v(27.77, 17.85) * mm});
            skLineSegment(sketch, "E1628", {"start": v(27.77, 17.85) * mm, "end": v(27.67, 17.9) * mm});
            skLineSegment(sketch, "E1629", {"start": v(27.67, 17.9) * mm, "end": v(27.58, 17.94) * mm});
            skLineSegment(sketch, "E1630", {"start": v(27.58, 17.94) * mm, "end": v(27.5, 17.97) * mm});
            skLineSegment(sketch, "E1631", {"start": v(27.5, 17.97) * mm, "end": v(27.43, 18) * mm});
            skLineSegment(sketch, "E1632", {"start": v(27.43, 18) * mm, "end": v(27.36, 18.03) * mm});
            skLineSegment(sketch, "E1633", {"start": v(27.36, 18.03) * mm, "end": v(27.3, 18.05) * mm});
            skLineSegment(sketch, "E1634", {"start": v(27.3, 18.05) * mm, "end": v(27.27, 18.06) * mm});
            skLineSegment(sketch, "E1635", {"start": v(27.27, 18.06) * mm, "end": v(27.23, 18.07) * mm});
            skLineSegment(sketch, "E1636", {"start": v(27.23, 18.07) * mm, "end": v(27.2, 18.08) * mm});
            skLineSegment(sketch, "E1637", {"start": v(27.2, 18.08) * mm, "end": v(27.2, 18.09) * mm});
            skLineSegment(sketch, "E1638", {"start": v(27.2, 18.09) * mm, "end": v(25.24, 18.6) * mm});
            skLineSegment(sketch, "E1639", {"start": v(25.24, 18.6) * mm, "end": v(25.93, 22.4) * mm});
            skLineSegment(sketch, "E1640", {"start": v(1.98, 24.92) * mm, "end": v(0, 25.12) * mm});
            skLineSegment(sketch, "E1641", {"start": v(-0.2, 23.14) * mm, "end": v(0.2, 27.1) * mm});
            skCircle(sketch, "E1642", {"center": v(-2.5, -40.5) * mm, "radius": 9 * mm});
            skCircle(sketch, "E1643", {"center": v(-2.5, -40.5) * mm, "radius": 2.5 * mm});
            skLineSegment(sketch, "E1644.bottom", {"start": v(1.44, -42.9) * mm, "end": v(3.94, -42.9) * mm});
            skLineSegment(sketch, "E1644.top", {"start": v(1.44, -37.4) * mm, "end": v(3.94, -37.4) * mm});
            skLineSegment(sketch, "E1644.left", {"start": v(1.44, -42.9) * mm, "end": v(1.44, -37.4) * mm});
            skLineSegment(sketch, "E1644.right", {"start": v(3.94, -42.9) * mm, "end": v(3.94, -37.4) * mm});
            skLineSegment(sketch, "E1645.MirrorCS", {"start": v(3.98, 27.89) * mm, "end": v(6.48, 27.89) * mm});
            skLineSegment(sketch, "E1646.MirrorCS", {"start": v(3.98, 27.89) * mm, "end": v(3.98, 22.39) * mm});
            skLineSegment(sketch, "E1647.MirrorCS", {"start": v(3.98, 22.39) * mm, "end": v(6.48, 22.39) * mm});
            skLineSegment(sketch, "E1648.MirrorCS", {"start": v(6.48, 27.89) * mm, "end": v(6.48, 22.39) * mm});
            skCircle(sketch, "E1649", {"center": v(0, 25.12) * mm, "radius": 2.5 * mm});
            skCircle(sketch, "E1650", {"center": v(0, 25.12) * mm, "radius": 9 * mm});
            skSolve(sketch);
        }
        {
            var Q0;
            Q0=makeQuery(id+"F0.imprint","IMPRINT",FACE,{"disambiguationData":[TD([[makeQuery(id+"F0.imprint","IMPRINT",EDGE,{"derivedFrom":sQuery(id+"F0.wireOp",EDGE,"E416")}),1.0]])]});
            var Q1;
            Q1=makeQuery(id+"F0.imprint","IMPRINT",FACE,{"disambiguationData":[TD([[makeQuery(id+"F0.imprint","IMPRINT",EDGE,{"derivedFrom":sQuery(id+"F0.wireOp",EDGE,"E0")}),1.0]])]});
            extrude(context, id + "F1", {"entities" : qUnion([Q0, Q1]), "depth" : 10 * mm});
        }
        {
            var Q0;
            Q0=makeQuery(id+"F0.imprint","IMPRINT",FACE,{"disambiguationData":[TD([[makeQuery(id+"F0.imprint","IMPRINT",EDGE,{"derivedFrom":sQuery(id+"F0.wireOp",EDGE,"E1645.MirrorCS")}),1.0]])]});
            var Q1;
            Q1=makeQuery(id+"F0.imprint","IMPRINT",FACE,{"disambiguationData":[TD([[makeQuery(id+"F0.imprint","IMPRINT",EDGE,{"derivedFrom":sQuery(id+"F0.wireOp",EDGE,"E1642")}),1.0]])]});
            extrude(context, id + "F2", {"entities" : qUnion([Q0, Q1]), "operationType" : NewBodyOperationType.ADD, "depth" : 18 * mm});
        }
    });
